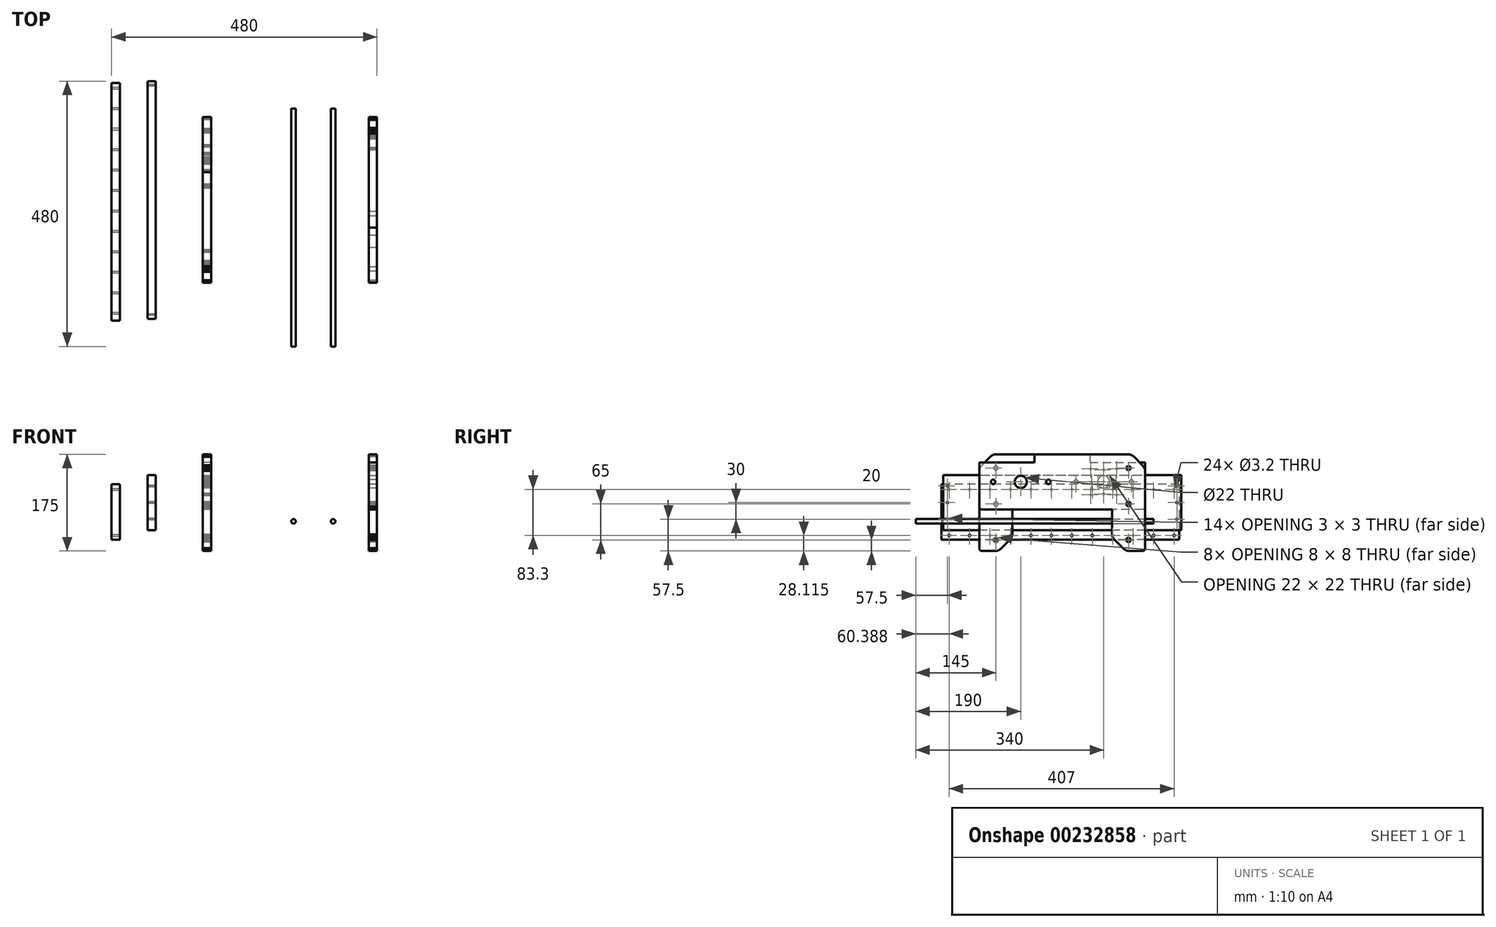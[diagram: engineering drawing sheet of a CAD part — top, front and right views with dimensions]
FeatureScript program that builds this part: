
annotation { "Feature Type Name" : "Feature", "Feature Type Description" : "" }
export const myFeature = defineFeature(function(context is Context, id is Id, definition is map)
    precondition{}
    {
        {
            var Q0;
            Q0=qCreatedBy(makeId("Right.planeOp"),FACE);
            var sketch = newSketch(context, id + "F0", { "sketchPlane" : qUnion([Q0])});
            skLineSegment(sketch, "E0", {"start": v(-140, 97.5) * mm, "end": v(-125, 97.5) * mm});
            skLineSegment(sketch, "E1", {"start": v(-125, 97.5) * mm, "end": v(-122.96, 97.12) * mm});
            skLineSegment(sketch, "E2", {"start": v(-122.96, 97.12) * mm, "end": v(-120.94, 96.66) * mm});
            skLineSegment(sketch, "E3", {"start": v(-120.94, 96.66) * mm, "end": v(-118.94, 96.1) * mm});
            skLineSegment(sketch, "E4", {"start": v(-118.94, 96.1) * mm, "end": v(-116.96, 95.47) * mm});
            skLineSegment(sketch, "E5", {"start": v(-116.96, 95.47) * mm, "end": v(-115.02, 94.75) * mm});
            skLineSegment(sketch, "E6", {"start": v(-115.02, 94.75) * mm, "end": v(-113.1, 93.95) * mm});
            skLineSegment(sketch, "E7", {"start": v(-113.1, 93.95) * mm, "end": v(-111.23, 93.07) * mm});
            skLineSegment(sketch, "E8", {"start": v(-111.23, 93.07) * mm, "end": v(-109.4, 92.1) * mm});
            skLineSegment(sketch, "E9", {"start": v(-109.4, 92.1) * mm, "end": v(-107.6, 91.07) * mm});
            skLineSegment(sketch, "E10", {"start": v(-107.6, 91.07) * mm, "end": v(-105.85, 89.95) * mm});
            skLineSegment(sketch, "E11", {"start": v(-105.85, 89.95) * mm, "end": v(-104.15, 88.76) * mm});
            skLineSegment(sketch, "E12", {"start": v(-104.15, 88.76) * mm, "end": v(-102.5, 87.5) * mm});
            skLineSegment(sketch, "E13", {"start": v(-102.5, 87.5) * mm, "end": v(-90, 77.5) * mm});
            skLineSegment(sketch, "E14", {"start": v(-90, 77.5) * mm, "end": v(50, 77.5) * mm});
            skLineSegment(sketch, "E15", {"start": v(50, 77.5) * mm, "end": v(50, 62.5) * mm});
            skLineSegment(sketch, "E16", {"start": v(50, 62.5) * mm, "end": v(150, 62.5) * mm});
            skLineSegment(sketch, "E17", {"start": v(150, 62.5) * mm, "end": v(150, -17.5) * mm});
            skLineSegment(sketch, "E18", {"start": v(150, -17.5) * mm, "end": v(149.96, -18.15) * mm});
            skLineSegment(sketch, "E19", {"start": v(149.96, -18.15) * mm, "end": v(149.83, -18.8) * mm});
            skLineSegment(sketch, "E20", {"start": v(149.83, -18.8) * mm, "end": v(149.62, -19.41) * mm});
            skLineSegment(sketch, "E21", {"start": v(149.62, -19.41) * mm, "end": v(149.33, -20) * mm});
            skLineSegment(sketch, "E22", {"start": v(149.33, -20) * mm, "end": v(148.97, -20.54) * mm});
            skLineSegment(sketch, "E23", {"start": v(148.97, -20.54) * mm, "end": v(148.54, -21.04) * mm});
            skLineSegment(sketch, "E24", {"start": v(148.54, -21.04) * mm, "end": v(148.04, -21.47) * mm});
            skLineSegment(sketch, "E25", {"start": v(148.04, -21.47) * mm, "end": v(147.5, -21.83) * mm});
            skLineSegment(sketch, "E26", {"start": v(147.5, -21.83) * mm, "end": v(146.91, -22.12) * mm});
            skLineSegment(sketch, "E27", {"start": v(146.91, -22.12) * mm, "end": v(146.3, -22.33) * mm});
            skLineSegment(sketch, "E28", {"start": v(146.3, -22.33) * mm, "end": v(145.65, -22.46) * mm});
            skLineSegment(sketch, "E29", {"start": v(145.65, -22.46) * mm, "end": v(145, -22.5) * mm});
            skLineSegment(sketch, "E30", {"start": v(145, -22.5) * mm, "end": v(-90, -22.5) * mm});
            skLineSegment(sketch, "E31", {"start": v(-90, -22.5) * mm, "end": v(-90, -67.5) * mm});
            skLineSegment(sketch, "E32", {"start": v(-90, -67.5) * mm, "end": v(-90.16, -68.43) * mm});
            skLineSegment(sketch, "E33", {"start": v(-90.16, -68.43) * mm, "end": v(-90.37, -69.36) * mm});
            skLineSegment(sketch, "E34", {"start": v(-90.37, -69.36) * mm, "end": v(-90.63, -70.27) * mm});
            skLineSegment(sketch, "E35", {"start": v(-90.63, -70.27) * mm, "end": v(-90.93, -71.17) * mm});
            skLineSegment(sketch, "E36", {"start": v(-90.93, -71.17) * mm, "end": v(-91.29, -72.05) * mm});
            skLineSegment(sketch, "E37", {"start": v(-91.29, -72.05) * mm, "end": v(-91.69, -72.9) * mm});
            skLineSegment(sketch, "E38", {"start": v(-91.69, -72.9) * mm, "end": v(-92.14, -73.74) * mm});
            skLineSegment(sketch, "E39", {"start": v(-92.14, -73.74) * mm, "end": v(-92.63, -74.55) * mm});
            skLineSegment(sketch, "E40", {"start": v(-92.63, -74.55) * mm, "end": v(-93.16, -75.34) * mm});
            skLineSegment(sketch, "E41", {"start": v(-93.16, -75.34) * mm, "end": v(-93.73, -76.1) * mm});
            skLineSegment(sketch, "E42", {"start": v(-93.73, -76.1) * mm, "end": v(-94.35, -76.81) * mm});
            skLineSegment(sketch, "E43", {"start": v(-94.35, -76.81) * mm, "end": v(-95, -77.5) * mm});
            skLineSegment(sketch, "E44", {"start": v(-95, -77.5) * mm, "end": v(-110, -92.5) * mm});
            skLineSegment(sketch, "E45", {"start": v(-110, -92.5) * mm, "end": v(-110.69, -93.15) * mm});
            skLineSegment(sketch, "E46", {"start": v(-110.69, -93.15) * mm, "end": v(-111.4, -93.77) * mm});
            skLineSegment(sketch, "E47", {"start": v(-111.4, -93.77) * mm, "end": v(-112.16, -94.34) * mm});
            skLineSegment(sketch, "E48", {"start": v(-112.16, -94.34) * mm, "end": v(-112.95, -94.87) * mm});
            skLineSegment(sketch, "E49", {"start": v(-112.95, -94.87) * mm, "end": v(-113.76, -95.36) * mm});
            skLineSegment(sketch, "E50", {"start": v(-113.76, -95.36) * mm, "end": v(-114.6, -95.81) * mm});
            skLineSegment(sketch, "E51", {"start": v(-114.6, -95.81) * mm, "end": v(-115.45, -96.21) * mm});
            skLineSegment(sketch, "E52", {"start": v(-115.45, -96.21) * mm, "end": v(-116.33, -96.57) * mm});
            skLineSegment(sketch, "E53", {"start": v(-116.33, -96.57) * mm, "end": v(-117.23, -96.87) * mm});
            skLineSegment(sketch, "E54", {"start": v(-117.23, -96.87) * mm, "end": v(-118.14, -97.13) * mm});
            skLineSegment(sketch, "E55", {"start": v(-118.14, -97.13) * mm, "end": v(-119.07, -97.34) * mm});
            skLineSegment(sketch, "E56", {"start": v(-119.07, -97.34) * mm, "end": v(-120, -97.5) * mm});
            skLineSegment(sketch, "E57", {"start": v(-120, -97.5) * mm, "end": v(-145, -97.5) * mm});
            skLineSegment(sketch, "E58", {"start": v(-145, -97.5) * mm, "end": v(-145.65, -97.46) * mm});
            skLineSegment(sketch, "E59", {"start": v(-145.65, -97.46) * mm, "end": v(-146.3, -97.33) * mm});
            skLineSegment(sketch, "E60", {"start": v(-146.3, -97.33) * mm, "end": v(-146.91, -97.12) * mm});
            skLineSegment(sketch, "E61", {"start": v(-146.91, -97.12) * mm, "end": v(-147.5, -96.83) * mm});
            skLineSegment(sketch, "E62", {"start": v(-147.5, -96.83) * mm, "end": v(-148.04, -96.47) * mm});
            skLineSegment(sketch, "E63", {"start": v(-148.04, -96.47) * mm, "end": v(-148.54, -96.04) * mm});
            skLineSegment(sketch, "E64", {"start": v(-148.54, -96.04) * mm, "end": v(-148.97, -95.54) * mm});
            skLineSegment(sketch, "E65", {"start": v(-148.97, -95.54) * mm, "end": v(-149.33, -95) * mm});
            skLineSegment(sketch, "E66", {"start": v(-149.33, -95) * mm, "end": v(-149.62, -94.41) * mm});
            skLineSegment(sketch, "E67", {"start": v(-149.62, -94.41) * mm, "end": v(-149.83, -93.8) * mm});
            skLineSegment(sketch, "E68", {"start": v(-149.83, -93.8) * mm, "end": v(-149.96, -93.15) * mm});
            skLineSegment(sketch, "E69", {"start": v(-149.96, -93.15) * mm, "end": v(-150, -92.5) * mm});
            skLineSegment(sketch, "E70", {"start": v(-150, -92.5) * mm, "end": v(-150, 87.5) * mm});
            skLineSegment(sketch, "E71", {"start": v(-150, 87.5) * mm, "end": v(-149.91, 88.8) * mm});
            skLineSegment(sketch, "E72", {"start": v(-149.91, 88.8) * mm, "end": v(-149.66, 90.09) * mm});
            skLineSegment(sketch, "E73", {"start": v(-149.66, 90.09) * mm, "end": v(-149.24, 91.33) * mm});
            skLineSegment(sketch, "E74", {"start": v(-149.24, 91.33) * mm, "end": v(-148.66, 92.5) * mm});
            skLineSegment(sketch, "E75", {"start": v(-148.66, 92.5) * mm, "end": v(-147.93, 93.59) * mm});
            skLineSegment(sketch, "E76", {"start": v(-147.93, 93.59) * mm, "end": v(-147.07, 94.57) * mm});
            skLineSegment(sketch, "E77", {"start": v(-147.07, 94.57) * mm, "end": v(-146.09, 95.43) * mm});
            skLineSegment(sketch, "E78", {"start": v(-146.09, 95.43) * mm, "end": v(-145, 96.16) * mm});
            skLineSegment(sketch, "E79", {"start": v(-145, 96.16) * mm, "end": v(-143.83, 96.74) * mm});
            skLineSegment(sketch, "E80", {"start": v(-143.83, 96.74) * mm, "end": v(-142.59, 97.16) * mm});
            skLineSegment(sketch, "E81", {"start": v(-142.59, 97.16) * mm, "end": v(-141.3, 97.41) * mm});
            skLineSegment(sketch, "E82", {"start": v(-141.3, 97.41) * mm, "end": v(-140, 97.5) * mm});
            skLineSegment(sketch, "E83", {"start": v(-122.83, -80.33) * mm, "end": v(-122, -80.96) * mm});
            skLineSegment(sketch, "E84", {"start": v(-122, -80.96) * mm, "end": v(-121.04, -81.36) * mm});
            skLineSegment(sketch, "E85", {"start": v(-121.04, -81.36) * mm, "end": v(-120, -81.5) * mm});
            skLineSegment(sketch, "E86", {"start": v(-120, -81.5) * mm, "end": v(-118.96, -81.36) * mm});
            skLineSegment(sketch, "E87", {"start": v(-118.96, -81.36) * mm, "end": v(-118, -80.96) * mm});
            skLineSegment(sketch, "E88", {"start": v(-118, -80.96) * mm, "end": v(-117.17, -80.33) * mm});
            skLineSegment(sketch, "E89", {"start": v(-117.17, -80.33) * mm, "end": v(-116.54, -79.5) * mm});
            skLineSegment(sketch, "E90", {"start": v(-116.54, -79.5) * mm, "end": v(-116.14, -78.54) * mm});
            skLineSegment(sketch, "E91", {"start": v(-116.14, -78.54) * mm, "end": v(-116, -77.5) * mm});
            skLineSegment(sketch, "E92", {"start": v(-116, -77.5) * mm, "end": v(-116.14, -76.46) * mm});
            skLineSegment(sketch, "E93", {"start": v(-116.14, -76.46) * mm, "end": v(-116.54, -75.5) * mm});
            skLineSegment(sketch, "E94", {"start": v(-116.54, -75.5) * mm, "end": v(-117.17, -74.67) * mm});
            skLineSegment(sketch, "E95", {"start": v(-117.17, -74.67) * mm, "end": v(-118, -74.04) * mm});
            skLineSegment(sketch, "E96", {"start": v(-118, -74.04) * mm, "end": v(-118.96, -73.64) * mm});
            skLineSegment(sketch, "E97", {"start": v(-118.96, -73.64) * mm, "end": v(-120, -73.5) * mm});
            skLineSegment(sketch, "E98", {"start": v(-120, -73.5) * mm, "end": v(-121.04, -73.64) * mm});
            skLineSegment(sketch, "E99", {"start": v(-121.04, -73.64) * mm, "end": v(-122, -74.04) * mm});
            skLineSegment(sketch, "E100", {"start": v(-122, -74.04) * mm, "end": v(-122.83, -74.67) * mm});
            skLineSegment(sketch, "E101", {"start": v(-122.83, -74.67) * mm, "end": v(-123.46, -75.5) * mm});
            skLineSegment(sketch, "E102", {"start": v(-123.46, -75.5) * mm, "end": v(-123.86, -76.46) * mm});
            skLineSegment(sketch, "E103", {"start": v(-123.86, -76.46) * mm, "end": v(-124, -77.5) * mm});
            skLineSegment(sketch, "E104", {"start": v(-124, -77.5) * mm, "end": v(-123.86, -78.54) * mm});
            skLineSegment(sketch, "E105", {"start": v(-123.86, -78.54) * mm, "end": v(-123.46, -79.5) * mm});
            skLineSegment(sketch, "E106", {"start": v(-123.46, -79.5) * mm, "end": v(-122.83, -80.33) * mm});
            skLineSegment(sketch, "E107", {"start": v(-117.17, -9.67) * mm, "end": v(-118, -9.04) * mm});
            skLineSegment(sketch, "E108", {"start": v(-118, -9.04) * mm, "end": v(-118.96, -8.64) * mm});
            skLineSegment(sketch, "E109", {"start": v(-118.96, -8.64) * mm, "end": v(-120, -8.5) * mm});
            skLineSegment(sketch, "E110", {"start": v(-120, -8.5) * mm, "end": v(-121.04, -8.64) * mm});
            skLineSegment(sketch, "E111", {"start": v(-121.04, -8.64) * mm, "end": v(-122, -9.04) * mm});
            skLineSegment(sketch, "E112", {"start": v(-122, -9.04) * mm, "end": v(-122.83, -9.67) * mm});
            skLineSegment(sketch, "E113", {"start": v(-122.83, -9.67) * mm, "end": v(-123.46, -10.5) * mm});
            skLineSegment(sketch, "E114", {"start": v(-123.46, -10.5) * mm, "end": v(-123.86, -11.46) * mm});
            skLineSegment(sketch, "E115", {"start": v(-123.86, -11.46) * mm, "end": v(-124, -12.5) * mm});
            skLineSegment(sketch, "E116", {"start": v(-124, -12.5) * mm, "end": v(-123.86, -13.54) * mm});
            skLineSegment(sketch, "E117", {"start": v(-123.86, -13.54) * mm, "end": v(-123.46, -14.5) * mm});
            skLineSegment(sketch, "E118", {"start": v(-123.46, -14.5) * mm, "end": v(-122.83, -15.33) * mm});
            skLineSegment(sketch, "E119", {"start": v(-122.83, -15.33) * mm, "end": v(-122, -15.96) * mm});
            skLineSegment(sketch, "E120", {"start": v(-122, -15.96) * mm, "end": v(-121.04, -16.36) * mm});
            skLineSegment(sketch, "E121", {"start": v(-121.04, -16.36) * mm, "end": v(-120, -16.5) * mm});
            skLineSegment(sketch, "E122", {"start": v(-120, -16.5) * mm, "end": v(-118.96, -16.36) * mm});
            skLineSegment(sketch, "E123", {"start": v(-118.96, -16.36) * mm, "end": v(-118, -15.96) * mm});
            skLineSegment(sketch, "E124", {"start": v(-118, -15.96) * mm, "end": v(-117.17, -15.33) * mm});
            skLineSegment(sketch, "E125", {"start": v(-117.17, -15.33) * mm, "end": v(-116.54, -14.5) * mm});
            skLineSegment(sketch, "E126", {"start": v(-116.54, -14.5) * mm, "end": v(-116.14, -13.54) * mm});
            skLineSegment(sketch, "E127", {"start": v(-116.14, -13.54) * mm, "end": v(-116, -12.5) * mm});
            skLineSegment(sketch, "E128", {"start": v(-116, -12.5) * mm, "end": v(-116.14, -11.46) * mm});
            skLineSegment(sketch, "E129", {"start": v(-116.14, -11.46) * mm, "end": v(-116.54, -10.5) * mm});
            skLineSegment(sketch, "E130", {"start": v(-116.54, -10.5) * mm, "end": v(-117.17, -9.67) * mm});
            skLineSegment(sketch, "E131", {"start": v(-118, 49.04) * mm, "end": v(-117.17, 49.67) * mm});
            skLineSegment(sketch, "E132", {"start": v(-117.17, 49.67) * mm, "end": v(-116.54, 50.5) * mm});
            skLineSegment(sketch, "E133", {"start": v(-116.54, 50.5) * mm, "end": v(-116.14, 51.46) * mm});
            skLineSegment(sketch, "E134", {"start": v(-116.14, 51.46) * mm, "end": v(-116, 52.5) * mm});
            skLineSegment(sketch, "E135", {"start": v(-116, 52.5) * mm, "end": v(-116.14, 53.54) * mm});
            skLineSegment(sketch, "E136", {"start": v(-116.14, 53.54) * mm, "end": v(-116.54, 54.5) * mm});
            skLineSegment(sketch, "E137", {"start": v(-116.54, 54.5) * mm, "end": v(-117.17, 55.33) * mm});
            skLineSegment(sketch, "E138", {"start": v(-117.17, 55.33) * mm, "end": v(-118, 55.96) * mm});
            skLineSegment(sketch, "E139", {"start": v(-118, 55.96) * mm, "end": v(-118.96, 56.36) * mm});
            skLineSegment(sketch, "E140", {"start": v(-118.96, 56.36) * mm, "end": v(-120, 56.5) * mm});
            skLineSegment(sketch, "E141", {"start": v(-120, 56.5) * mm, "end": v(-121.04, 56.36) * mm});
            skLineSegment(sketch, "E142", {"start": v(-121.04, 56.36) * mm, "end": v(-122, 55.96) * mm});
            skLineSegment(sketch, "E143", {"start": v(-122, 55.96) * mm, "end": v(-122.83, 55.33) * mm});
            skLineSegment(sketch, "E144", {"start": v(-122.83, 55.33) * mm, "end": v(-123.46, 54.5) * mm});
            skLineSegment(sketch, "E145", {"start": v(-123.46, 54.5) * mm, "end": v(-123.86, 53.54) * mm});
            skLineSegment(sketch, "E146", {"start": v(-123.86, 53.54) * mm, "end": v(-124, 52.5) * mm});
            skLineSegment(sketch, "E147", {"start": v(-124, 52.5) * mm, "end": v(-123.86, 51.46) * mm});
            skLineSegment(sketch, "E148", {"start": v(-123.86, 51.46) * mm, "end": v(-123.46, 50.5) * mm});
            skLineSegment(sketch, "E149", {"start": v(-123.46, 50.5) * mm, "end": v(-122.83, 49.67) * mm});
            skLineSegment(sketch, "E150", {"start": v(-122.83, 49.67) * mm, "end": v(-122, 49.04) * mm});
            skLineSegment(sketch, "E151", {"start": v(-122, 49.04) * mm, "end": v(-121.04, 48.64) * mm});
            skLineSegment(sketch, "E152", {"start": v(-121.04, 48.64) * mm, "end": v(-120, 48.5) * mm});
            skLineSegment(sketch, "E153", {"start": v(-120, 48.5) * mm, "end": v(-118.96, 48.64) * mm});
            skLineSegment(sketch, "E154", {"start": v(-118.96, 48.64) * mm, "end": v(-118, 49.04) * mm});
            skLineSegment(sketch, "E155", {"start": v(72.15, 38.13) * mm, "end": v(69.5, 37.03) * mm});
            skLineSegment(sketch, "E156", {"start": v(69.5, 37.03) * mm, "end": v(67.22, 35.28) * mm});
            skLineSegment(sketch, "E157", {"start": v(67.22, 35.28) * mm, "end": v(65.47, 33) * mm});
            skLineSegment(sketch, "E158", {"start": v(65.47, 33) * mm, "end": v(64.37, 30.35) * mm});
            skLineSegment(sketch, "E159", {"start": v(64.37, 30.35) * mm, "end": v(64, 27.5) * mm});
            skLineSegment(sketch, "E160", {"start": v(64, 27.5) * mm, "end": v(64.37, 24.65) * mm});
            skLineSegment(sketch, "E161", {"start": v(64.37, 24.65) * mm, "end": v(65.47, 22) * mm});
            skLineSegment(sketch, "E162", {"start": v(65.47, 22) * mm, "end": v(67.22, 19.72) * mm});
            skLineSegment(sketch, "E163", {"start": v(67.22, 19.72) * mm, "end": v(69.5, 17.97) * mm});
            skLineSegment(sketch, "E164", {"start": v(69.5, 17.97) * mm, "end": v(72.15, 16.87) * mm});
            skLineSegment(sketch, "E165", {"start": v(72.15, 16.87) * mm, "end": v(75, 16.5) * mm});
            skLineSegment(sketch, "E166", {"start": v(75, 16.5) * mm, "end": v(77.85, 16.87) * mm});
            skLineSegment(sketch, "E167", {"start": v(77.85, 16.87) * mm, "end": v(80.5, 17.97) * mm});
            skLineSegment(sketch, "E168", {"start": v(80.5, 17.97) * mm, "end": v(82.78, 19.72) * mm});
            skLineSegment(sketch, "E169", {"start": v(82.78, 19.72) * mm, "end": v(84.53, 22) * mm});
            skLineSegment(sketch, "E170", {"start": v(84.53, 22) * mm, "end": v(85.63, 24.65) * mm});
            skLineSegment(sketch, "E171", {"start": v(85.63, 24.65) * mm, "end": v(86, 27.5) * mm});
            skLineSegment(sketch, "E172", {"start": v(86, 27.5) * mm, "end": v(85.63, 30.35) * mm});
            skLineSegment(sketch, "E173", {"start": v(85.63, 30.35) * mm, "end": v(84.53, 33) * mm});
            skLineSegment(sketch, "E174", {"start": v(84.53, 33) * mm, "end": v(82.78, 35.28) * mm});
            skLineSegment(sketch, "E175", {"start": v(82.78, 35.28) * mm, "end": v(80.5, 37.03) * mm});
            skLineSegment(sketch, "E176", {"start": v(80.5, 37.03) * mm, "end": v(77.85, 38.13) * mm});
            skLineSegment(sketch, "E177", {"start": v(77.85, 38.13) * mm, "end": v(75, 38.5) * mm});
            skLineSegment(sketch, "E178", {"start": v(75, 38.5) * mm, "end": v(72.15, 38.13) * mm});
            skLineSegment(sketch, "E179", {"start": v(97.8, 5.25) * mm, "end": v(97.49, 5.01) * mm});
            skLineSegment(sketch, "E180", {"start": v(97.49, 5.01) * mm, "end": v(97.25, 4.7) * mm});
            skLineSegment(sketch, "E181", {"start": v(97.25, 4.7) * mm, "end": v(97.1, 4.34) * mm});
            skLineSegment(sketch, "E182", {"start": v(97.1, 4.34) * mm, "end": v(97.05, 3.95) * mm});
            skLineSegment(sketch, "E183", {"start": v(97.05, 3.95) * mm, "end": v(97.1, 3.56) * mm});
            skLineSegment(sketch, "E184", {"start": v(97.1, 3.56) * mm, "end": v(97.25, 3.2) * mm});
            skLineSegment(sketch, "E185", {"start": v(97.25, 3.2) * mm, "end": v(97.49, 2.89) * mm});
            skLineSegment(sketch, "E186", {"start": v(97.49, 2.89) * mm, "end": v(97.8, 2.65) * mm});
            skLineSegment(sketch, "E187", {"start": v(97.8, 2.65) * mm, "end": v(98.16, 2.5) * mm});
            skLineSegment(sketch, "E188", {"start": v(98.16, 2.5) * mm, "end": v(98.55, 2.45) * mm});
            skLineSegment(sketch, "E189", {"start": v(98.55, 2.45) * mm, "end": v(98.94, 2.5) * mm});
            skLineSegment(sketch, "E190", {"start": v(98.94, 2.5) * mm, "end": v(99.3, 2.65) * mm});
            skLineSegment(sketch, "E191", {"start": v(99.3, 2.65) * mm, "end": v(99.61, 2.89) * mm});
            skLineSegment(sketch, "E192", {"start": v(99.61, 2.89) * mm, "end": v(99.85, 3.2) * mm});
            skLineSegment(sketch, "E193", {"start": v(99.85, 3.2) * mm, "end": v(100, 3.56) * mm});
            skLineSegment(sketch, "E194", {"start": v(100, 3.56) * mm, "end": v(100.05, 3.95) * mm});
            skLineSegment(sketch, "E195", {"start": v(100.05, 3.95) * mm, "end": v(100, 4.34) * mm});
            skLineSegment(sketch, "E196", {"start": v(100, 4.34) * mm, "end": v(99.85, 4.7) * mm});
            skLineSegment(sketch, "E197", {"start": v(99.85, 4.7) * mm, "end": v(99.61, 5.01) * mm});
            skLineSegment(sketch, "E198", {"start": v(99.61, 5.01) * mm, "end": v(99.3, 5.25) * mm});
            skLineSegment(sketch, "E199", {"start": v(99.3, 5.25) * mm, "end": v(98.94, 5.4) * mm});
            skLineSegment(sketch, "E200", {"start": v(98.94, 5.4) * mm, "end": v(98.55, 5.45) * mm});
            skLineSegment(sketch, "E201", {"start": v(98.55, 5.45) * mm, "end": v(98.16, 5.4) * mm});
            skLineSegment(sketch, "E202", {"start": v(98.16, 5.4) * mm, "end": v(97.8, 5.25) * mm});
            skLineSegment(sketch, "E203", {"start": v(51.45, 5.45) * mm, "end": v(51.06, 5.4) * mm});
            skLineSegment(sketch, "E204", {"start": v(51.06, 5.4) * mm, "end": v(50.7, 5.25) * mm});
            skLineSegment(sketch, "E205", {"start": v(50.7, 5.25) * mm, "end": v(50.39, 5.01) * mm});
            skLineSegment(sketch, "E206", {"start": v(50.39, 5.01) * mm, "end": v(50.15, 4.7) * mm});
            skLineSegment(sketch, "E207", {"start": v(50.15, 4.7) * mm, "end": v(50, 4.34) * mm});
            skLineSegment(sketch, "E208", {"start": v(50, 4.34) * mm, "end": v(49.95, 3.95) * mm});
            skLineSegment(sketch, "E209", {"start": v(49.95, 3.95) * mm, "end": v(50, 3.56) * mm});
            skLineSegment(sketch, "E210", {"start": v(50, 3.56) * mm, "end": v(50.15, 3.2) * mm});
            skLineSegment(sketch, "E211", {"start": v(50.15, 3.2) * mm, "end": v(50.39, 2.89) * mm});
            skLineSegment(sketch, "E212", {"start": v(50.39, 2.89) * mm, "end": v(50.7, 2.65) * mm});
            skLineSegment(sketch, "E213", {"start": v(50.7, 2.65) * mm, "end": v(51.06, 2.5) * mm});
            skLineSegment(sketch, "E214", {"start": v(51.06, 2.5) * mm, "end": v(51.45, 2.45) * mm});
            skLineSegment(sketch, "E215", {"start": v(51.45, 2.45) * mm, "end": v(51.84, 2.5) * mm});
            skLineSegment(sketch, "E216", {"start": v(51.84, 2.5) * mm, "end": v(52.2, 2.65) * mm});
            skLineSegment(sketch, "E217", {"start": v(52.2, 2.65) * mm, "end": v(52.51, 2.89) * mm});
            skLineSegment(sketch, "E218", {"start": v(52.51, 2.89) * mm, "end": v(52.75, 3.2) * mm});
            skLineSegment(sketch, "E219", {"start": v(52.75, 3.2) * mm, "end": v(52.9, 3.56) * mm});
            skLineSegment(sketch, "E220", {"start": v(52.9, 3.56) * mm, "end": v(52.95, 3.95) * mm});
            skLineSegment(sketch, "E221", {"start": v(52.95, 3.95) * mm, "end": v(52.9, 4.34) * mm});
            skLineSegment(sketch, "E222", {"start": v(52.9, 4.34) * mm, "end": v(52.75, 4.7) * mm});
            skLineSegment(sketch, "E223", {"start": v(52.75, 4.7) * mm, "end": v(52.51, 5.01) * mm});
            skLineSegment(sketch, "E224", {"start": v(52.51, 5.01) * mm, "end": v(52.2, 5.25) * mm});
            skLineSegment(sketch, "E225", {"start": v(52.2, 5.25) * mm, "end": v(51.84, 5.4) * mm});
            skLineSegment(sketch, "E226", {"start": v(51.84, 5.4) * mm, "end": v(51.45, 5.45) * mm});
            skLineSegment(sketch, "E227", {"start": v(50, 51.44) * mm, "end": v(49.95, 51.05) * mm});
            skLineSegment(sketch, "E228", {"start": v(49.95, 51.05) * mm, "end": v(50, 50.66) * mm});
            skLineSegment(sketch, "E229", {"start": v(50, 50.66) * mm, "end": v(50.15, 50.3) * mm});
            skLineSegment(sketch, "E230", {"start": v(50.15, 50.3) * mm, "end": v(50.39, 49.99) * mm});
            skLineSegment(sketch, "E231", {"start": v(50.39, 49.99) * mm, "end": v(50.7, 49.75) * mm});
            skLineSegment(sketch, "E232", {"start": v(50.7, 49.75) * mm, "end": v(51.06, 49.6) * mm});
            skLineSegment(sketch, "E233", {"start": v(51.06, 49.6) * mm, "end": v(51.45, 49.55) * mm});
            skLineSegment(sketch, "E234", {"start": v(51.45, 49.55) * mm, "end": v(51.84, 49.6) * mm});
            skLineSegment(sketch, "E235", {"start": v(51.84, 49.6) * mm, "end": v(52.2, 49.75) * mm});
            skLineSegment(sketch, "E236", {"start": v(52.2, 49.75) * mm, "end": v(52.51, 49.99) * mm});
            skLineSegment(sketch, "E237", {"start": v(52.51, 49.99) * mm, "end": v(52.75, 50.3) * mm});
            skLineSegment(sketch, "E238", {"start": v(52.75, 50.3) * mm, "end": v(52.9, 50.66) * mm});
            skLineSegment(sketch, "E239", {"start": v(52.9, 50.66) * mm, "end": v(52.95, 51.05) * mm});
            skLineSegment(sketch, "E240", {"start": v(52.95, 51.05) * mm, "end": v(52.9, 51.44) * mm});
            skLineSegment(sketch, "E241", {"start": v(52.9, 51.44) * mm, "end": v(52.75, 51.8) * mm});
            skLineSegment(sketch, "E242", {"start": v(52.75, 51.8) * mm, "end": v(52.51, 52.11) * mm});
            skLineSegment(sketch, "E243", {"start": v(52.51, 52.11) * mm, "end": v(52.2, 52.35) * mm});
            skLineSegment(sketch, "E244", {"start": v(52.2, 52.35) * mm, "end": v(51.84, 52.5) * mm});
            skLineSegment(sketch, "E245", {"start": v(51.84, 52.5) * mm, "end": v(51.45, 52.55) * mm});
            skLineSegment(sketch, "E246", {"start": v(51.45, 52.55) * mm, "end": v(51.06, 52.5) * mm});
            skLineSegment(sketch, "E247", {"start": v(51.06, 52.5) * mm, "end": v(50.7, 52.35) * mm});
            skLineSegment(sketch, "E248", {"start": v(50.7, 52.35) * mm, "end": v(50.39, 52.11) * mm});
            skLineSegment(sketch, "E249", {"start": v(50.39, 52.11) * mm, "end": v(50.15, 51.8) * mm});
            skLineSegment(sketch, "E250", {"start": v(50.15, 51.8) * mm, "end": v(50, 51.44) * mm});
            skLineSegment(sketch, "E251", {"start": v(98.16, 49.6) * mm, "end": v(98.55, 49.55) * mm});
            skLineSegment(sketch, "E252", {"start": v(98.55, 49.55) * mm, "end": v(98.94, 49.6) * mm});
            skLineSegment(sketch, "E253", {"start": v(98.94, 49.6) * mm, "end": v(99.3, 49.75) * mm});
            skLineSegment(sketch, "E254", {"start": v(99.3, 49.75) * mm, "end": v(99.61, 49.99) * mm});
            skLineSegment(sketch, "E255", {"start": v(99.61, 49.99) * mm, "end": v(99.85, 50.3) * mm});
            skLineSegment(sketch, "E256", {"start": v(99.85, 50.3) * mm, "end": v(100, 50.66) * mm});
            skLineSegment(sketch, "E257", {"start": v(100, 50.66) * mm, "end": v(100.05, 51.05) * mm});
            skLineSegment(sketch, "E258", {"start": v(100.05, 51.05) * mm, "end": v(100, 51.44) * mm});
            skLineSegment(sketch, "E259", {"start": v(100, 51.44) * mm, "end": v(99.85, 51.8) * mm});
            skLineSegment(sketch, "E260", {"start": v(99.85, 51.8) * mm, "end": v(99.61, 52.11) * mm});
            skLineSegment(sketch, "E261", {"start": v(99.61, 52.11) * mm, "end": v(99.3, 52.35) * mm});
            skLineSegment(sketch, "E262", {"start": v(99.3, 52.35) * mm, "end": v(98.94, 52.5) * mm});
            skLineSegment(sketch, "E263", {"start": v(98.94, 52.5) * mm, "end": v(98.55, 52.55) * mm});
            skLineSegment(sketch, "E264", {"start": v(98.55, 52.55) * mm, "end": v(98.16, 52.5) * mm});
            skLineSegment(sketch, "E265", {"start": v(98.16, 52.5) * mm, "end": v(97.8, 52.35) * mm});
            skLineSegment(sketch, "E266", {"start": v(97.8, 52.35) * mm, "end": v(97.49, 52.11) * mm});
            skLineSegment(sketch, "E267", {"start": v(97.49, 52.11) * mm, "end": v(97.25, 51.8) * mm});
            skLineSegment(sketch, "E268", {"start": v(97.25, 51.8) * mm, "end": v(97.1, 51.44) * mm});
            skLineSegment(sketch, "E269", {"start": v(97.1, 51.44) * mm, "end": v(97.05, 51.05) * mm});
            skLineSegment(sketch, "E270", {"start": v(97.05, 51.05) * mm, "end": v(97.1, 50.66) * mm});
            skLineSegment(sketch, "E271", {"start": v(97.1, 50.66) * mm, "end": v(97.25, 50.3) * mm});
            skLineSegment(sketch, "E272", {"start": v(97.25, 50.3) * mm, "end": v(97.49, 49.99) * mm});
            skLineSegment(sketch, "E273", {"start": v(97.49, 49.99) * mm, "end": v(97.8, 49.75) * mm});
            skLineSegment(sketch, "E274", {"start": v(97.8, 49.75) * mm, "end": v(98.16, 49.6) * mm});
            skLineSegment(sketch, "E275", {"start": v(51.63, 27.89) * mm, "end": v(51.58, 27.5) * mm});
            skLineSegment(sketch, "E276", {"start": v(51.58, 27.5) * mm, "end": v(51.63, 27.11) * mm});
            skLineSegment(sketch, "E277", {"start": v(51.63, 27.11) * mm, "end": v(51.78, 26.75) * mm});
            skLineSegment(sketch, "E278", {"start": v(51.78, 26.75) * mm, "end": v(52.02, 26.44) * mm});
            skLineSegment(sketch, "E279", {"start": v(52.02, 26.44) * mm, "end": v(52.33, 26.2) * mm});
            skLineSegment(sketch, "E280", {"start": v(52.33, 26.2) * mm, "end": v(52.7, 26.05) * mm});
            skLineSegment(sketch, "E281", {"start": v(52.7, 26.05) * mm, "end": v(53.08, 26) * mm});
            skLineSegment(sketch, "E282", {"start": v(53.08, 26) * mm, "end": v(53.47, 26.05) * mm});
            skLineSegment(sketch, "E283", {"start": v(53.47, 26.05) * mm, "end": v(53.83, 26.2) * mm});
            skLineSegment(sketch, "E284", {"start": v(53.83, 26.2) * mm, "end": v(54.14, 26.44) * mm});
            skLineSegment(sketch, "E285", {"start": v(54.14, 26.44) * mm, "end": v(54.38, 26.75) * mm});
            skLineSegment(sketch, "E286", {"start": v(54.38, 26.75) * mm, "end": v(54.53, 27.11) * mm});
            skLineSegment(sketch, "E287", {"start": v(54.53, 27.11) * mm, "end": v(54.58, 27.5) * mm});
            skLineSegment(sketch, "E288", {"start": v(54.58, 27.5) * mm, "end": v(54.53, 27.89) * mm});
            skLineSegment(sketch, "E289", {"start": v(54.53, 27.89) * mm, "end": v(54.38, 28.25) * mm});
            skLineSegment(sketch, "E290", {"start": v(54.38, 28.25) * mm, "end": v(54.14, 28.56) * mm});
            skLineSegment(sketch, "E291", {"start": v(54.14, 28.56) * mm, "end": v(53.83, 28.8) * mm});
            skLineSegment(sketch, "E292", {"start": v(53.83, 28.8) * mm, "end": v(53.47, 28.95) * mm});
            skLineSegment(sketch, "E293", {"start": v(53.47, 28.95) * mm, "end": v(53.08, 29) * mm});
            skLineSegment(sketch, "E294", {"start": v(53.08, 29) * mm, "end": v(52.7, 28.95) * mm});
            skLineSegment(sketch, "E295", {"start": v(52.7, 28.95) * mm, "end": v(52.33, 28.8) * mm});
            skLineSegment(sketch, "E296", {"start": v(52.33, 28.8) * mm, "end": v(52.02, 28.56) * mm});
            skLineSegment(sketch, "E297", {"start": v(52.02, 28.56) * mm, "end": v(51.78, 28.25) * mm});
            skLineSegment(sketch, "E298", {"start": v(51.78, 28.25) * mm, "end": v(51.63, 27.89) * mm});
            skLineSegment(sketch, "E299", {"start": v(73.94, 4.52) * mm, "end": v(74.25, 4.28) * mm});
            skLineSegment(sketch, "E300", {"start": v(74.25, 4.28) * mm, "end": v(74.61, 4.13) * mm});
            skLineSegment(sketch, "E301", {"start": v(74.61, 4.13) * mm, "end": v(75, 4.08) * mm});
            skLineSegment(sketch, "E302", {"start": v(75, 4.08) * mm, "end": v(75.39, 4.13) * mm});
            skLineSegment(sketch, "E303", {"start": v(75.39, 4.13) * mm, "end": v(75.75, 4.28) * mm});
            skLineSegment(sketch, "E304", {"start": v(75.75, 4.28) * mm, "end": v(76.06, 4.52) * mm});
            skLineSegment(sketch, "E305", {"start": v(76.06, 4.52) * mm, "end": v(76.3, 4.83) * mm});
            skLineSegment(sketch, "E306", {"start": v(76.3, 4.83) * mm, "end": v(76.45, 5.2) * mm});
            skLineSegment(sketch, "E307", {"start": v(76.45, 5.2) * mm, "end": v(76.5, 5.58) * mm});
            skLineSegment(sketch, "E308", {"start": v(76.5, 5.58) * mm, "end": v(76.45, 5.97) * mm});
            skLineSegment(sketch, "E309", {"start": v(76.45, 5.97) * mm, "end": v(76.3, 6.33) * mm});
            skLineSegment(sketch, "E310", {"start": v(76.3, 6.33) * mm, "end": v(76.06, 6.64) * mm});
            skLineSegment(sketch, "E311", {"start": v(76.06, 6.64) * mm, "end": v(75.75, 6.88) * mm});
            skLineSegment(sketch, "E312", {"start": v(75.75, 6.88) * mm, "end": v(75.39, 7.03) * mm});
            skLineSegment(sketch, "E313", {"start": v(75.39, 7.03) * mm, "end": v(75, 7.08) * mm});
            skLineSegment(sketch, "E314", {"start": v(75, 7.08) * mm, "end": v(74.61, 7.03) * mm});
            skLineSegment(sketch, "E315", {"start": v(74.61, 7.03) * mm, "end": v(74.25, 6.88) * mm});
            skLineSegment(sketch, "E316", {"start": v(74.25, 6.88) * mm, "end": v(73.94, 6.64) * mm});
            skLineSegment(sketch, "E317", {"start": v(73.94, 6.64) * mm, "end": v(73.7, 6.33) * mm});
            skLineSegment(sketch, "E318", {"start": v(73.7, 6.33) * mm, "end": v(73.55, 5.97) * mm});
            skLineSegment(sketch, "E319", {"start": v(73.55, 5.97) * mm, "end": v(73.5, 5.58) * mm});
            skLineSegment(sketch, "E320", {"start": v(73.5, 5.58) * mm, "end": v(73.55, 5.2) * mm});
            skLineSegment(sketch, "E321", {"start": v(73.55, 5.2) * mm, "end": v(73.7, 4.83) * mm});
            skLineSegment(sketch, "E322", {"start": v(73.7, 4.83) * mm, "end": v(73.94, 4.52) * mm});
            skLineSegment(sketch, "E323", {"start": v(96.53, 28.95) * mm, "end": v(96.17, 28.8) * mm});
            skLineSegment(sketch, "E324", {"start": v(96.17, 28.8) * mm, "end": v(95.86, 28.56) * mm});
            skLineSegment(sketch, "E325", {"start": v(95.86, 28.56) * mm, "end": v(95.62, 28.25) * mm});
            skLineSegment(sketch, "E326", {"start": v(95.62, 28.25) * mm, "end": v(95.47, 27.89) * mm});
            skLineSegment(sketch, "E327", {"start": v(95.47, 27.89) * mm, "end": v(95.42, 27.5) * mm});
            skLineSegment(sketch, "E328", {"start": v(95.42, 27.5) * mm, "end": v(95.47, 27.11) * mm});
            skLineSegment(sketch, "E329", {"start": v(95.47, 27.11) * mm, "end": v(95.62, 26.75) * mm});
            skLineSegment(sketch, "E330", {"start": v(95.62, 26.75) * mm, "end": v(95.86, 26.44) * mm});
            skLineSegment(sketch, "E331", {"start": v(95.86, 26.44) * mm, "end": v(96.17, 26.2) * mm});
            skLineSegment(sketch, "E332", {"start": v(96.17, 26.2) * mm, "end": v(96.53, 26.05) * mm});
            skLineSegment(sketch, "E333", {"start": v(96.53, 26.05) * mm, "end": v(96.92, 26) * mm});
            skLineSegment(sketch, "E334", {"start": v(96.92, 26) * mm, "end": v(97.3, 26.05) * mm});
            skLineSegment(sketch, "E335", {"start": v(97.3, 26.05) * mm, "end": v(97.67, 26.2) * mm});
            skLineSegment(sketch, "E336", {"start": v(97.67, 26.2) * mm, "end": v(97.98, 26.44) * mm});
            skLineSegment(sketch, "E337", {"start": v(97.98, 26.44) * mm, "end": v(98.22, 26.75) * mm});
            skLineSegment(sketch, "E338", {"start": v(98.22, 26.75) * mm, "end": v(98.37, 27.11) * mm});
            skLineSegment(sketch, "E339", {"start": v(98.37, 27.11) * mm, "end": v(98.42, 27.5) * mm});
            skLineSegment(sketch, "E340", {"start": v(98.42, 27.5) * mm, "end": v(98.37, 27.89) * mm});
            skLineSegment(sketch, "E341", {"start": v(98.37, 27.89) * mm, "end": v(98.22, 28.25) * mm});
            skLineSegment(sketch, "E342", {"start": v(98.22, 28.25) * mm, "end": v(97.98, 28.56) * mm});
            skLineSegment(sketch, "E343", {"start": v(97.98, 28.56) * mm, "end": v(97.67, 28.8) * mm});
            skLineSegment(sketch, "E344", {"start": v(97.67, 28.8) * mm, "end": v(97.3, 28.95) * mm});
            skLineSegment(sketch, "E345", {"start": v(97.3, 28.95) * mm, "end": v(96.92, 29) * mm});
            skLineSegment(sketch, "E346", {"start": v(96.92, 29) * mm, "end": v(96.53, 28.95) * mm});
            skLineSegment(sketch, "E347", {"start": v(74.61, 50.87) * mm, "end": v(74.25, 50.72) * mm});
            skLineSegment(sketch, "E348", {"start": v(74.25, 50.72) * mm, "end": v(73.94, 50.48) * mm});
            skLineSegment(sketch, "E349", {"start": v(73.94, 50.48) * mm, "end": v(73.7, 50.17) * mm});
            skLineSegment(sketch, "E350", {"start": v(73.7, 50.17) * mm, "end": v(73.55, 49.8) * mm});
            skLineSegment(sketch, "E351", {"start": v(73.55, 49.8) * mm, "end": v(73.5, 49.42) * mm});
            skLineSegment(sketch, "E352", {"start": v(73.5, 49.42) * mm, "end": v(73.55, 49.03) * mm});
            skLineSegment(sketch, "E353", {"start": v(73.55, 49.03) * mm, "end": v(73.7, 48.67) * mm});
            skLineSegment(sketch, "E354", {"start": v(73.7, 48.67) * mm, "end": v(73.94, 48.36) * mm});
            skLineSegment(sketch, "E355", {"start": v(73.94, 48.36) * mm, "end": v(74.25, 48.12) * mm});
            skLineSegment(sketch, "E356", {"start": v(74.25, 48.12) * mm, "end": v(74.61, 47.97) * mm});
            skLineSegment(sketch, "E357", {"start": v(74.61, 47.97) * mm, "end": v(75, 47.92) * mm});
            skLineSegment(sketch, "E358", {"start": v(75, 47.92) * mm, "end": v(75.39, 47.97) * mm});
            skLineSegment(sketch, "E359", {"start": v(75.39, 47.97) * mm, "end": v(75.75, 48.12) * mm});
            skLineSegment(sketch, "E360", {"start": v(75.75, 48.12) * mm, "end": v(76.06, 48.36) * mm});
            skLineSegment(sketch, "E361", {"start": v(76.06, 48.36) * mm, "end": v(76.3, 48.67) * mm});
            skLineSegment(sketch, "E362", {"start": v(76.3, 48.67) * mm, "end": v(76.45, 49.03) * mm});
            skLineSegment(sketch, "E363", {"start": v(76.45, 49.03) * mm, "end": v(76.5, 49.42) * mm});
            skLineSegment(sketch, "E364", {"start": v(76.5, 49.42) * mm, "end": v(76.45, 49.8) * mm});
            skLineSegment(sketch, "E365", {"start": v(76.45, 49.8) * mm, "end": v(76.3, 50.17) * mm});
            skLineSegment(sketch, "E366", {"start": v(76.3, 50.17) * mm, "end": v(76.06, 50.48) * mm});
            skLineSegment(sketch, "E367", {"start": v(76.06, 50.48) * mm, "end": v(75.75, 50.72) * mm});
            skLineSegment(sketch, "E368", {"start": v(75.75, 50.72) * mm, "end": v(75.39, 50.87) * mm});
            skLineSegment(sketch, "E369", {"start": v(75.39, 50.87) * mm, "end": v(75, 50.92) * mm});
            skLineSegment(sketch, "E370", {"start": v(75, 50.92) * mm, "end": v(74.61, 50.87) * mm});
            skLineSegment(sketch, "E371", {"start": v(127, 30.96) * mm, "end": v(126.04, 31.36) * mm});
            skLineSegment(sketch, "E372", {"start": v(126.04, 31.36) * mm, "end": v(125, 31.5) * mm});
            skLineSegment(sketch, "E373", {"start": v(125, 31.5) * mm, "end": v(123.96, 31.36) * mm});
            skLineSegment(sketch, "E374", {"start": v(123.96, 31.36) * mm, "end": v(123, 30.96) * mm});
            skLineSegment(sketch, "E375", {"start": v(123, 30.96) * mm, "end": v(122.17, 30.33) * mm});
            skLineSegment(sketch, "E376", {"start": v(122.17, 30.33) * mm, "end": v(121.54, 29.5) * mm});
            skLineSegment(sketch, "E377", {"start": v(121.54, 29.5) * mm, "end": v(121.14, 28.54) * mm});
            skLineSegment(sketch, "E378", {"start": v(121.14, 28.54) * mm, "end": v(121, 27.5) * mm});
            skLineSegment(sketch, "E379", {"start": v(121, 27.5) * mm, "end": v(121.14, 26.46) * mm});
            skLineSegment(sketch, "E380", {"start": v(121.14, 26.46) * mm, "end": v(121.54, 25.5) * mm});
            skLineSegment(sketch, "E381", {"start": v(121.54, 25.5) * mm, "end": v(122.17, 24.67) * mm});
            skLineSegment(sketch, "E382", {"start": v(122.17, 24.67) * mm, "end": v(123, 24.04) * mm});
            skLineSegment(sketch, "E383", {"start": v(123, 24.04) * mm, "end": v(123.96, 23.64) * mm});
            skLineSegment(sketch, "E384", {"start": v(123.96, 23.64) * mm, "end": v(125, 23.5) * mm});
            skLineSegment(sketch, "E385", {"start": v(125, 23.5) * mm, "end": v(126.04, 23.64) * mm});
            skLineSegment(sketch, "E386", {"start": v(126.04, 23.64) * mm, "end": v(127, 24.04) * mm});
            skLineSegment(sketch, "E387", {"start": v(127, 24.04) * mm, "end": v(127.83, 24.67) * mm});
            skLineSegment(sketch, "E388", {"start": v(127.83, 24.67) * mm, "end": v(128.46, 25.5) * mm});
            skLineSegment(sketch, "E389", {"start": v(128.46, 25.5) * mm, "end": v(128.86, 26.46) * mm});
            skLineSegment(sketch, "E390", {"start": v(128.86, 26.46) * mm, "end": v(129, 27.5) * mm});
            skLineSegment(sketch, "E391", {"start": v(129, 27.5) * mm, "end": v(128.86, 28.54) * mm});
            skLineSegment(sketch, "E392", {"start": v(128.86, 28.54) * mm, "end": v(128.46, 29.5) * mm});
            skLineSegment(sketch, "E393", {"start": v(128.46, 29.5) * mm, "end": v(127.83, 30.33) * mm});
            skLineSegment(sketch, "E394", {"start": v(127.83, 30.33) * mm, "end": v(127, 30.96) * mm});
            skLineSegment(sketch, "E395", {"start": v(28.86, 28.54) * mm, "end": v(28.46, 29.5) * mm});
            skLineSegment(sketch, "E396", {"start": v(28.46, 29.5) * mm, "end": v(27.83, 30.33) * mm});
            skLineSegment(sketch, "E397", {"start": v(27.83, 30.33) * mm, "end": v(27, 30.96) * mm});
            skLineSegment(sketch, "E398", {"start": v(27, 30.96) * mm, "end": v(26.04, 31.36) * mm});
            skLineSegment(sketch, "E399", {"start": v(26.04, 31.36) * mm, "end": v(25, 31.5) * mm});
            skLineSegment(sketch, "E400", {"start": v(25, 31.5) * mm, "end": v(23.96, 31.36) * mm});
            skLineSegment(sketch, "E401", {"start": v(23.96, 31.36) * mm, "end": v(23, 30.96) * mm});
            skLineSegment(sketch, "E402", {"start": v(23, 30.96) * mm, "end": v(22.17, 30.33) * mm});
            skLineSegment(sketch, "E403", {"start": v(22.17, 30.33) * mm, "end": v(21.54, 29.5) * mm});
            skLineSegment(sketch, "E404", {"start": v(21.54, 29.5) * mm, "end": v(21.14, 28.54) * mm});
            skLineSegment(sketch, "E405", {"start": v(21.14, 28.54) * mm, "end": v(21, 27.5) * mm});
            skLineSegment(sketch, "E406", {"start": v(21, 27.5) * mm, "end": v(21.14, 26.46) * mm});
            skLineSegment(sketch, "E407", {"start": v(21.14, 26.46) * mm, "end": v(21.54, 25.5) * mm});
            skLineSegment(sketch, "E408", {"start": v(21.54, 25.5) * mm, "end": v(22.17, 24.67) * mm});
            skLineSegment(sketch, "E409", {"start": v(22.17, 24.67) * mm, "end": v(23, 24.04) * mm});
            skLineSegment(sketch, "E410", {"start": v(23, 24.04) * mm, "end": v(23.96, 23.64) * mm});
            skLineSegment(sketch, "E411", {"start": v(23.96, 23.64) * mm, "end": v(25, 23.5) * mm});
            skLineSegment(sketch, "E412", {"start": v(25, 23.5) * mm, "end": v(26.04, 23.64) * mm});
            skLineSegment(sketch, "E413", {"start": v(26.04, 23.64) * mm, "end": v(27, 24.04) * mm});
            skLineSegment(sketch, "E414", {"start": v(27, 24.04) * mm, "end": v(27.83, 24.67) * mm});
            skLineSegment(sketch, "E415", {"start": v(27.83, 24.67) * mm, "end": v(28.46, 25.5) * mm});
            skLineSegment(sketch, "E416", {"start": v(28.46, 25.5) * mm, "end": v(28.86, 26.46) * mm});
            skLineSegment(sketch, "E417", {"start": v(28.86, 26.46) * mm, "end": v(29, 27.5) * mm});
            skLineSegment(sketch, "E418", {"start": v(29, 27.5) * mm, "end": v(28.86, 28.54) * mm});
            skSolve(sketch);
        }
        {
            var Q0;
            Q0=qCreatedBy(makeId("Right.planeOp"),FACE);
            cPlane(context, id + "F1", {"entities" : qUnion([Q0]), "cplaneType" : CPlaneType.OFFSET, "offset" : 100 * mm, "width" : 150 * mm, "height" : 150 * mm});
        }
        {
            var Q0;
            Q0=qCreatedBy(id+"F1.planeOp",FACE);
            var sketch = newSketch(context, id + "F2", { "sketchPlane" : qUnion([Q0])});
            skLineSegment(sketch, "E419", {"start": v(90, -12.5) * mm, "end": v(-145, -12.5) * mm});
            skLineSegment(sketch, "E420", {"start": v(-145, -12.5) * mm, "end": v(-145.65, -12.46) * mm});
            skLineSegment(sketch, "E421", {"start": v(-145.65, -12.46) * mm, "end": v(-146.3, -12.33) * mm});
            skLineSegment(sketch, "E422", {"start": v(-146.3, -12.33) * mm, "end": v(-146.91, -12.12) * mm});
            skLineSegment(sketch, "E423", {"start": v(-146.91, -12.12) * mm, "end": v(-147.5, -11.83) * mm});
            skLineSegment(sketch, "E424", {"start": v(-147.5, -11.83) * mm, "end": v(-148.04, -11.47) * mm});
            skLineSegment(sketch, "E425", {"start": v(-148.04, -11.47) * mm, "end": v(-148.54, -11.04) * mm});
            skLineSegment(sketch, "E426", {"start": v(-148.54, -11.04) * mm, "end": v(-148.97, -10.54) * mm});
            skLineSegment(sketch, "E427", {"start": v(-148.97, -10.54) * mm, "end": v(-149.33, -10) * mm});
            skLineSegment(sketch, "E428", {"start": v(-149.33, -10) * mm, "end": v(-149.62, -9.41) * mm});
            skLineSegment(sketch, "E429", {"start": v(-149.62, -9.41) * mm, "end": v(-149.83, -8.8) * mm});
            skLineSegment(sketch, "E430", {"start": v(-149.83, -8.8) * mm, "end": v(-149.96, -8.15) * mm});
            skLineSegment(sketch, "E431", {"start": v(-149.96, -8.15) * mm, "end": v(-150, -7.5) * mm});
            skLineSegment(sketch, "E432", {"start": v(-150, -7.5) * mm, "end": v(-150, 72.5) * mm});
            skLineSegment(sketch, "E433", {"start": v(-150, 72.5) * mm, "end": v(-50, 72.5) * mm});
            skLineSegment(sketch, "E434", {"start": v(-50, 72.5) * mm, "end": v(-50, 87.5) * mm});
            skLineSegment(sketch, "E435", {"start": v(-50, 87.5) * mm, "end": v(120, 87.5) * mm});
            skLineSegment(sketch, "E436", {"start": v(120, 87.5) * mm, "end": v(120.93, 87.34) * mm});
            skLineSegment(sketch, "E437", {"start": v(120.93, 87.34) * mm, "end": v(121.86, 87.13) * mm});
            skLineSegment(sketch, "E438", {"start": v(121.86, 87.13) * mm, "end": v(122.77, 86.87) * mm});
            skLineSegment(sketch, "E439", {"start": v(122.77, 86.87) * mm, "end": v(123.67, 86.57) * mm});
            skLineSegment(sketch, "E440", {"start": v(123.67, 86.57) * mm, "end": v(124.55, 86.21) * mm});
            skLineSegment(sketch, "E441", {"start": v(124.55, 86.21) * mm, "end": v(125.4, 85.81) * mm});
            skLineSegment(sketch, "E442", {"start": v(125.4, 85.81) * mm, "end": v(126.24, 85.36) * mm});
            skLineSegment(sketch, "E443", {"start": v(126.24, 85.36) * mm, "end": v(127.05, 84.87) * mm});
            skLineSegment(sketch, "E444", {"start": v(127.05, 84.87) * mm, "end": v(127.84, 84.34) * mm});
            skLineSegment(sketch, "E445", {"start": v(127.84, 84.34) * mm, "end": v(128.6, 83.77) * mm});
            skLineSegment(sketch, "E446", {"start": v(128.6, 83.77) * mm, "end": v(129.31, 83.15) * mm});
            skLineSegment(sketch, "E447", {"start": v(129.31, 83.15) * mm, "end": v(130, 82.5) * mm});
            skLineSegment(sketch, "E448", {"start": v(130, 82.5) * mm, "end": v(145, 67.5) * mm});
            skLineSegment(sketch, "E449", {"start": v(145, 67.5) * mm, "end": v(145.65, 66.81) * mm});
            skLineSegment(sketch, "E450", {"start": v(145.65, 66.81) * mm, "end": v(146.27, 66.1) * mm});
            skLineSegment(sketch, "E451", {"start": v(146.27, 66.1) * mm, "end": v(146.84, 65.34) * mm});
            skLineSegment(sketch, "E452", {"start": v(146.84, 65.34) * mm, "end": v(147.37, 64.55) * mm});
            skLineSegment(sketch, "E453", {"start": v(147.37, 64.55) * mm, "end": v(147.86, 63.74) * mm});
            skLineSegment(sketch, "E454", {"start": v(147.86, 63.74) * mm, "end": v(148.31, 62.9) * mm});
            skLineSegment(sketch, "E455", {"start": v(148.31, 62.9) * mm, "end": v(148.71, 62.05) * mm});
            skLineSegment(sketch, "E456", {"start": v(148.71, 62.05) * mm, "end": v(149.07, 61.17) * mm});
            skLineSegment(sketch, "E457", {"start": v(149.07, 61.17) * mm, "end": v(149.37, 60.27) * mm});
            skLineSegment(sketch, "E458", {"start": v(149.37, 60.27) * mm, "end": v(149.63, 59.36) * mm});
            skLineSegment(sketch, "E459", {"start": v(149.63, 59.36) * mm, "end": v(149.84, 58.43) * mm});
            skLineSegment(sketch, "E460", {"start": v(149.84, 58.43) * mm, "end": v(150, 57.5) * mm});
            skLineSegment(sketch, "E461", {"start": v(150, 57.5) * mm, "end": v(150, -82.5) * mm});
            skLineSegment(sketch, "E462", {"start": v(150, -82.5) * mm, "end": v(149.96, -83.15) * mm});
            skLineSegment(sketch, "E463", {"start": v(149.96, -83.15) * mm, "end": v(149.83, -83.8) * mm});
            skLineSegment(sketch, "E464", {"start": v(149.83, -83.8) * mm, "end": v(149.62, -84.41) * mm});
            skLineSegment(sketch, "E465", {"start": v(149.62, -84.41) * mm, "end": v(149.33, -85) * mm});
            skLineSegment(sketch, "E466", {"start": v(149.33, -85) * mm, "end": v(148.97, -85.54) * mm});
            skLineSegment(sketch, "E467", {"start": v(148.97, -85.54) * mm, "end": v(148.54, -86.04) * mm});
            skLineSegment(sketch, "E468", {"start": v(148.54, -86.04) * mm, "end": v(148.04, -86.47) * mm});
            skLineSegment(sketch, "E469", {"start": v(148.04, -86.47) * mm, "end": v(147.5, -86.83) * mm});
            skLineSegment(sketch, "E470", {"start": v(147.5, -86.83) * mm, "end": v(146.91, -87.12) * mm});
            skLineSegment(sketch, "E471", {"start": v(146.91, -87.12) * mm, "end": v(146.3, -87.33) * mm});
            skLineSegment(sketch, "E472", {"start": v(146.3, -87.33) * mm, "end": v(145.65, -87.46) * mm});
            skLineSegment(sketch, "E473", {"start": v(145.65, -87.46) * mm, "end": v(145, -87.5) * mm});
            skLineSegment(sketch, "E474", {"start": v(145, -87.5) * mm, "end": v(120, -87.5) * mm});
            skLineSegment(sketch, "E475", {"start": v(120, -87.5) * mm, "end": v(119.07, -87.34) * mm});
            skLineSegment(sketch, "E476", {"start": v(119.07, -87.34) * mm, "end": v(118.14, -87.13) * mm});
            skLineSegment(sketch, "E477", {"start": v(118.14, -87.13) * mm, "end": v(117.23, -86.87) * mm});
            skLineSegment(sketch, "E478", {"start": v(117.23, -86.87) * mm, "end": v(116.33, -86.57) * mm});
            skLineSegment(sketch, "E479", {"start": v(116.33, -86.57) * mm, "end": v(115.45, -86.21) * mm});
            skLineSegment(sketch, "E480", {"start": v(115.45, -86.21) * mm, "end": v(114.6, -85.81) * mm});
            skLineSegment(sketch, "E481", {"start": v(114.6, -85.81) * mm, "end": v(113.76, -85.36) * mm});
            skLineSegment(sketch, "E482", {"start": v(113.76, -85.36) * mm, "end": v(112.95, -84.87) * mm});
            skLineSegment(sketch, "E483", {"start": v(112.95, -84.87) * mm, "end": v(112.16, -84.34) * mm});
            skLineSegment(sketch, "E484", {"start": v(112.16, -84.34) * mm, "end": v(111.4, -83.77) * mm});
            skLineSegment(sketch, "E485", {"start": v(111.4, -83.77) * mm, "end": v(110.69, -83.15) * mm});
            skLineSegment(sketch, "E486", {"start": v(110.69, -83.15) * mm, "end": v(110, -82.5) * mm});
            skLineSegment(sketch, "E487", {"start": v(110, -82.5) * mm, "end": v(95, -67.5) * mm});
            skLineSegment(sketch, "E488", {"start": v(95, -67.5) * mm, "end": v(94.35, -66.81) * mm});
            skLineSegment(sketch, "E489", {"start": v(94.35, -66.81) * mm, "end": v(93.73, -66.1) * mm});
            skLineSegment(sketch, "E490", {"start": v(93.73, -66.1) * mm, "end": v(93.16, -65.34) * mm});
            skLineSegment(sketch, "E491", {"start": v(93.16, -65.34) * mm, "end": v(92.63, -64.55) * mm});
            skLineSegment(sketch, "E492", {"start": v(92.63, -64.55) * mm, "end": v(92.14, -63.74) * mm});
            skLineSegment(sketch, "E493", {"start": v(92.14, -63.74) * mm, "end": v(91.69, -62.9) * mm});
            skLineSegment(sketch, "E494", {"start": v(91.69, -62.9) * mm, "end": v(91.29, -62.05) * mm});
            skLineSegment(sketch, "E495", {"start": v(91.29, -62.05) * mm, "end": v(90.93, -61.17) * mm});
            skLineSegment(sketch, "E496", {"start": v(90.93, -61.17) * mm, "end": v(90.63, -60.27) * mm});
            skLineSegment(sketch, "E497", {"start": v(90.63, -60.27) * mm, "end": v(90.37, -59.36) * mm});
            skLineSegment(sketch, "E498", {"start": v(90.37, -59.36) * mm, "end": v(90.16, -58.43) * mm});
            skLineSegment(sketch, "E499", {"start": v(90.16, -58.43) * mm, "end": v(90, -57.5) * mm});
            skLineSegment(sketch, "E500", {"start": v(90, -57.5) * mm, "end": v(90, -12.5) * mm});
            skLineSegment(sketch, "E501", {"start": v(118, 0.96) * mm, "end": v(117.17, 0.33) * mm});
            skLineSegment(sketch, "E502", {"start": v(117.17, 0.33) * mm, "end": v(116.54, -0.5) * mm});
            skLineSegment(sketch, "E503", {"start": v(116.54, -0.5) * mm, "end": v(116.14, -1.46) * mm});
            skLineSegment(sketch, "E504", {"start": v(116.14, -1.46) * mm, "end": v(116, -2.5) * mm});
            skLineSegment(sketch, "E505", {"start": v(116, -2.5) * mm, "end": v(116.14, -3.54) * mm});
            skLineSegment(sketch, "E506", {"start": v(116.14, -3.54) * mm, "end": v(116.54, -4.5) * mm});
            skLineSegment(sketch, "E507", {"start": v(116.54, -4.5) * mm, "end": v(117.17, -5.33) * mm});
            skLineSegment(sketch, "E508", {"start": v(117.17, -5.33) * mm, "end": v(118, -5.96) * mm});
            skLineSegment(sketch, "E509", {"start": v(118, -5.96) * mm, "end": v(118.96, -6.36) * mm});
            skLineSegment(sketch, "E510", {"start": v(118.96, -6.36) * mm, "end": v(120, -6.5) * mm});
            skLineSegment(sketch, "E511", {"start": v(120, -6.5) * mm, "end": v(121.04, -6.36) * mm});
            skLineSegment(sketch, "E512", {"start": v(121.04, -6.36) * mm, "end": v(122, -5.96) * mm});
            skLineSegment(sketch, "E513", {"start": v(122, -5.96) * mm, "end": v(122.83, -5.33) * mm});
            skLineSegment(sketch, "E514", {"start": v(122.83, -5.33) * mm, "end": v(123.46, -4.5) * mm});
            skLineSegment(sketch, "E515", {"start": v(123.46, -4.5) * mm, "end": v(123.86, -3.54) * mm});
            skLineSegment(sketch, "E516", {"start": v(123.86, -3.54) * mm, "end": v(124, -2.5) * mm});
            skLineSegment(sketch, "E517", {"start": v(124, -2.5) * mm, "end": v(123.86, -1.46) * mm});
            skLineSegment(sketch, "E518", {"start": v(123.86, -1.46) * mm, "end": v(123.46, -0.5) * mm});
            skLineSegment(sketch, "E519", {"start": v(123.46, -0.5) * mm, "end": v(122.83, 0.33) * mm});
            skLineSegment(sketch, "E520", {"start": v(122.83, 0.33) * mm, "end": v(122, 0.96) * mm});
            skLineSegment(sketch, "E521", {"start": v(122, 0.96) * mm, "end": v(121.04, 1.36) * mm});
            skLineSegment(sketch, "E522", {"start": v(121.04, 1.36) * mm, "end": v(120, 1.5) * mm});
            skLineSegment(sketch, "E523", {"start": v(120, 1.5) * mm, "end": v(118.96, 1.36) * mm});
            skLineSegment(sketch, "E524", {"start": v(118.96, 1.36) * mm, "end": v(118, 0.96) * mm});
            skLineSegment(sketch, "E525", {"start": v(122, -70.96) * mm, "end": v(122.83, -70.33) * mm});
            skLineSegment(sketch, "E526", {"start": v(122.83, -70.33) * mm, "end": v(123.46, -69.5) * mm});
            skLineSegment(sketch, "E527", {"start": v(123.46, -69.5) * mm, "end": v(123.86, -68.54) * mm});
            skLineSegment(sketch, "E528", {"start": v(123.86, -68.54) * mm, "end": v(124, -67.5) * mm});
            skLineSegment(sketch, "E529", {"start": v(124, -67.5) * mm, "end": v(123.86, -66.46) * mm});
            skLineSegment(sketch, "E530", {"start": v(123.86, -66.46) * mm, "end": v(123.46, -65.5) * mm});
            skLineSegment(sketch, "E531", {"start": v(123.46, -65.5) * mm, "end": v(122.83, -64.67) * mm});
            skLineSegment(sketch, "E532", {"start": v(122.83, -64.67) * mm, "end": v(122, -64.04) * mm});
            skLineSegment(sketch, "E533", {"start": v(122, -64.04) * mm, "end": v(121.04, -63.64) * mm});
            skLineSegment(sketch, "E534", {"start": v(121.04, -63.64) * mm, "end": v(120, -63.5) * mm});
            skLineSegment(sketch, "E535", {"start": v(120, -63.5) * mm, "end": v(118.96, -63.64) * mm});
            skLineSegment(sketch, "E536", {"start": v(118.96, -63.64) * mm, "end": v(118, -64.04) * mm});
            skLineSegment(sketch, "E537", {"start": v(118, -64.04) * mm, "end": v(117.17, -64.67) * mm});
            skLineSegment(sketch, "E538", {"start": v(117.17, -64.67) * mm, "end": v(116.54, -65.5) * mm});
            skLineSegment(sketch, "E539", {"start": v(116.54, -65.5) * mm, "end": v(116.14, -66.46) * mm});
            skLineSegment(sketch, "E540", {"start": v(116.14, -66.46) * mm, "end": v(116, -67.5) * mm});
            skLineSegment(sketch, "E541", {"start": v(116, -67.5) * mm, "end": v(116.14, -68.54) * mm});
            skLineSegment(sketch, "E542", {"start": v(116.14, -68.54) * mm, "end": v(116.54, -69.5) * mm});
            skLineSegment(sketch, "E543", {"start": v(116.54, -69.5) * mm, "end": v(117.17, -70.33) * mm});
            skLineSegment(sketch, "E544", {"start": v(117.17, -70.33) * mm, "end": v(118, -70.96) * mm});
            skLineSegment(sketch, "E545", {"start": v(118, -70.96) * mm, "end": v(118.96, -71.36) * mm});
            skLineSegment(sketch, "E546", {"start": v(118.96, -71.36) * mm, "end": v(120, -71.5) * mm});
            skLineSegment(sketch, "E547", {"start": v(120, -71.5) * mm, "end": v(121.04, -71.36) * mm});
            skLineSegment(sketch, "E548", {"start": v(121.04, -71.36) * mm, "end": v(122, -70.96) * mm});
            skLineSegment(sketch, "E549", {"start": v(117.17, 59.67) * mm, "end": v(118, 59.04) * mm});
            skLineSegment(sketch, "E550", {"start": v(118, 59.04) * mm, "end": v(118.96, 58.64) * mm});
            skLineSegment(sketch, "E551", {"start": v(118.96, 58.64) * mm, "end": v(120, 58.5) * mm});
            skLineSegment(sketch, "E552", {"start": v(120, 58.5) * mm, "end": v(121.04, 58.64) * mm});
            skLineSegment(sketch, "E553", {"start": v(121.04, 58.64) * mm, "end": v(122, 59.04) * mm});
            skLineSegment(sketch, "E554", {"start": v(122, 59.04) * mm, "end": v(122.83, 59.67) * mm});
            skLineSegment(sketch, "E555", {"start": v(122.83, 59.67) * mm, "end": v(123.46, 60.5) * mm});
            skLineSegment(sketch, "E556", {"start": v(123.46, 60.5) * mm, "end": v(123.86, 61.46) * mm});
            skLineSegment(sketch, "E557", {"start": v(123.86, 61.46) * mm, "end": v(124, 62.5) * mm});
            skLineSegment(sketch, "E558", {"start": v(124, 62.5) * mm, "end": v(123.86, 63.54) * mm});
            skLineSegment(sketch, "E559", {"start": v(123.86, 63.54) * mm, "end": v(123.46, 64.5) * mm});
            skLineSegment(sketch, "E560", {"start": v(123.46, 64.5) * mm, "end": v(122.83, 65.33) * mm});
            skLineSegment(sketch, "E561", {"start": v(122.83, 65.33) * mm, "end": v(122, 65.96) * mm});
            skLineSegment(sketch, "E562", {"start": v(122, 65.96) * mm, "end": v(121.04, 66.36) * mm});
            skLineSegment(sketch, "E563", {"start": v(121.04, 66.36) * mm, "end": v(120, 66.5) * mm});
            skLineSegment(sketch, "E564", {"start": v(120, 66.5) * mm, "end": v(118.96, 66.36) * mm});
            skLineSegment(sketch, "E565", {"start": v(118.96, 66.36) * mm, "end": v(118, 65.96) * mm});
            skLineSegment(sketch, "E566", {"start": v(118, 65.96) * mm, "end": v(117.17, 65.33) * mm});
            skLineSegment(sketch, "E567", {"start": v(117.17, 65.33) * mm, "end": v(116.54, 64.5) * mm});
            skLineSegment(sketch, "E568", {"start": v(116.54, 64.5) * mm, "end": v(116.14, 63.54) * mm});
            skLineSegment(sketch, "E569", {"start": v(116.14, 63.54) * mm, "end": v(116, 62.5) * mm});
            skLineSegment(sketch, "E570", {"start": v(116, 62.5) * mm, "end": v(116.14, 61.46) * mm});
            skLineSegment(sketch, "E571", {"start": v(116.14, 61.46) * mm, "end": v(116.54, 60.5) * mm});
            skLineSegment(sketch, "E572", {"start": v(116.54, 60.5) * mm, "end": v(117.17, 59.67) * mm});
            skCircle(sketch, "E573", {"center": v(-125, 37.5) * mm, "radius": 4 * mm});
            skCircle(sketch, "E574", {"center": v(-25, 37.5) * mm, "radius": 4 * mm});
            skCircle(sketch, "E575", {"center": v(-75, 37.5) * mm, "radius": 11 * mm});
            skSolve(sketch);
        }
        {
            var Q0;
            Q0=qCreatedBy(makeId("Right.planeOp"),FACE);
            cPlane(context, id + "F3", {"entities" : qUnion([Q0]), "cplaneType" : CPlaneType.OFFSET, "offset" : 100 * mm, "oppositeDirection" : true, "width" : 150 * mm, "height" : 150 * mm});
        }
        {
            var Q0;
            Q0=qCreatedBy(id+"F3.planeOp",FACE);
            var sketch = newSketch(context, id + "F4", { "sketchPlane" : qUnion([Q0])});
            skLineSegment(sketch, "E576", {"start": v(-30, 23) * mm, "end": v(-30, 32) * mm});
            skLineSegment(sketch, "E577", {"start": v(-30, 32) * mm, "end": v(-29.96, 32.65) * mm});
            skLineSegment(sketch, "E578", {"start": v(-29.96, 32.65) * mm, "end": v(-29.83, 33.3) * mm});
            skLineSegment(sketch, "E579", {"start": v(-29.83, 33.3) * mm, "end": v(-29.62, 33.91) * mm});
            skLineSegment(sketch, "E580", {"start": v(-29.62, 33.91) * mm, "end": v(-29.33, 34.5) * mm});
            skLineSegment(sketch, "E581", {"start": v(-29.33, 34.5) * mm, "end": v(-28.97, 35.04) * mm});
            skLineSegment(sketch, "E582", {"start": v(-28.97, 35.04) * mm, "end": v(-28.54, 35.54) * mm});
            skLineSegment(sketch, "E583", {"start": v(-28.54, 35.54) * mm, "end": v(-28.04, 35.97) * mm});
            skLineSegment(sketch, "E584", {"start": v(-28.04, 35.97) * mm, "end": v(-27.5, 36.33) * mm});
            skLineSegment(sketch, "E585", {"start": v(-27.5, 36.33) * mm, "end": v(-26.91, 36.62) * mm});
            skLineSegment(sketch, "E586", {"start": v(-26.91, 36.62) * mm, "end": v(-26.3, 36.83) * mm});
            skLineSegment(sketch, "E587", {"start": v(-26.3, 36.83) * mm, "end": v(-25.65, 36.96) * mm});
            skLineSegment(sketch, "E588", {"start": v(-25.65, 36.96) * mm, "end": v(-25, 37) * mm});
            skLineSegment(sketch, "E589", {"start": v(-25, 37) * mm, "end": v(25, 37) * mm});
            skLineSegment(sketch, "E590", {"start": v(25, 37) * mm, "end": v(25.65, 36.96) * mm});
            skLineSegment(sketch, "E591", {"start": v(25.65, 36.96) * mm, "end": v(26.3, 36.83) * mm});
            skLineSegment(sketch, "E592", {"start": v(26.3, 36.83) * mm, "end": v(26.91, 36.62) * mm});
            skLineSegment(sketch, "E593", {"start": v(26.91, 36.62) * mm, "end": v(27.5, 36.33) * mm});
            skLineSegment(sketch, "E594", {"start": v(27.5, 36.33) * mm, "end": v(28.04, 35.97) * mm});
            skLineSegment(sketch, "E595", {"start": v(28.04, 35.97) * mm, "end": v(28.54, 35.54) * mm});
            skLineSegment(sketch, "E596", {"start": v(28.54, 35.54) * mm, "end": v(28.97, 35.04) * mm});
            skLineSegment(sketch, "E597", {"start": v(28.97, 35.04) * mm, "end": v(29.33, 34.5) * mm});
            skLineSegment(sketch, "E598", {"start": v(29.33, 34.5) * mm, "end": v(29.62, 33.91) * mm});
            skLineSegment(sketch, "E599", {"start": v(29.62, 33.91) * mm, "end": v(29.83, 33.3) * mm});
            skLineSegment(sketch, "E600", {"start": v(29.83, 33.3) * mm, "end": v(29.96, 32.65) * mm});
            skLineSegment(sketch, "E601", {"start": v(29.96, 32.65) * mm, "end": v(30, 32) * mm});
            skLineSegment(sketch, "E602", {"start": v(30, 32) * mm, "end": v(30, 23) * mm});
            skLineSegment(sketch, "E603", {"start": v(30, 23) * mm, "end": v(200, 23) * mm});
            skLineSegment(sketch, "E604", {"start": v(200, 23) * mm, "end": v(200, -37) * mm});
            skLineSegment(sketch, "E605", {"start": v(200, -37) * mm, "end": v(-200, -37) * mm});
            skLineSegment(sketch, "E606", {"start": v(-200, -37) * mm, "end": v(-200, 23) * mm});
            skLineSegment(sketch, "E607", {"start": v(-200, 23) * mm, "end": v(-30, 23) * mm});
            skLineSegment(sketch, "E608", {"start": v(-0.39, -12.47) * mm, "end": v(-0.75, -12.62) * mm});
            skLineSegment(sketch, "E609", {"start": v(-0.75, -12.62) * mm, "end": v(-1.06, -12.86) * mm});
            skLineSegment(sketch, "E610", {"start": v(-1.06, -12.86) * mm, "end": v(-1.3, -13.17) * mm});
            skLineSegment(sketch, "E611", {"start": v(-1.3, -13.17) * mm, "end": v(-1.45, -13.53) * mm});
            skLineSegment(sketch, "E612", {"start": v(-1.45, -13.53) * mm, "end": v(-1.5, -13.92) * mm});
            skLineSegment(sketch, "E613", {"start": v(-1.5, -13.92) * mm, "end": v(-1.45, -14.3) * mm});
            skLineSegment(sketch, "E614", {"start": v(-1.45, -14.3) * mm, "end": v(-1.3, -14.67) * mm});
            skLineSegment(sketch, "E615", {"start": v(-1.3, -14.67) * mm, "end": v(-1.06, -14.98) * mm});
            skLineSegment(sketch, "E616", {"start": v(-1.06, -14.98) * mm, "end": v(-0.75, -15.22) * mm});
            skLineSegment(sketch, "E617", {"start": v(-0.75, -15.22) * mm, "end": v(-0.39, -15.37) * mm});
            skLineSegment(sketch, "E618", {"start": v(-0.39, -15.37) * mm, "end": v(0, -15.42) * mm});
            skLineSegment(sketch, "E619", {"start": v(0, -15.42) * mm, "end": v(0.39, -15.37) * mm});
            skLineSegment(sketch, "E620", {"start": v(0.39, -15.37) * mm, "end": v(0.75, -15.22) * mm});
            skLineSegment(sketch, "E621", {"start": v(0.75, -15.22) * mm, "end": v(1.06, -14.98) * mm});
            skLineSegment(sketch, "E622", {"start": v(1.06, -14.98) * mm, "end": v(1.3, -14.67) * mm});
            skLineSegment(sketch, "E623", {"start": v(1.3, -14.67) * mm, "end": v(1.45, -14.3) * mm});
            skLineSegment(sketch, "E624", {"start": v(1.45, -14.3) * mm, "end": v(1.5, -13.92) * mm});
            skLineSegment(sketch, "E625", {"start": v(1.5, -13.92) * mm, "end": v(1.45, -13.53) * mm});
            skLineSegment(sketch, "E626", {"start": v(1.45, -13.53) * mm, "end": v(1.3, -13.17) * mm});
            skLineSegment(sketch, "E627", {"start": v(1.3, -13.17) * mm, "end": v(1.06, -12.86) * mm});
            skLineSegment(sketch, "E628", {"start": v(1.06, -12.86) * mm, "end": v(0.75, -12.62) * mm});
            skLineSegment(sketch, "E629", {"start": v(0.75, -12.62) * mm, "end": v(0.39, -12.47) * mm});
            skLineSegment(sketch, "E630", {"start": v(0.39, -12.47) * mm, "end": v(0, -12.42) * mm});
            skLineSegment(sketch, "E631", {"start": v(0, -12.42) * mm, "end": v(-0.39, -12.47) * mm});
            skLineSegment(sketch, "E632", {"start": v(21.17, 9.3) * mm, "end": v(20.86, 9.06) * mm});
            skLineSegment(sketch, "E633", {"start": v(20.86, 9.06) * mm, "end": v(20.62, 8.75) * mm});
            skLineSegment(sketch, "E634", {"start": v(20.62, 8.75) * mm, "end": v(20.47, 8.39) * mm});
            skLineSegment(sketch, "E635", {"start": v(20.47, 8.39) * mm, "end": v(20.42, 8) * mm});
            skLineSegment(sketch, "E636", {"start": v(20.42, 8) * mm, "end": v(20.47, 7.61) * mm});
            skLineSegment(sketch, "E637", {"start": v(20.47, 7.61) * mm, "end": v(20.62, 7.25) * mm});
            skLineSegment(sketch, "E638", {"start": v(20.62, 7.25) * mm, "end": v(20.86, 6.94) * mm});
            skLineSegment(sketch, "E639", {"start": v(20.86, 6.94) * mm, "end": v(21.17, 6.7) * mm});
            skLineSegment(sketch, "E640", {"start": v(21.17, 6.7) * mm, "end": v(21.53, 6.55) * mm});
            skLineSegment(sketch, "E641", {"start": v(21.53, 6.55) * mm, "end": v(21.92, 6.5) * mm});
            skLineSegment(sketch, "E642", {"start": v(21.92, 6.5) * mm, "end": v(22.3, 6.55) * mm});
            skLineSegment(sketch, "E643", {"start": v(22.3, 6.55) * mm, "end": v(22.67, 6.7) * mm});
            skLineSegment(sketch, "E644", {"start": v(22.67, 6.7) * mm, "end": v(22.98, 6.94) * mm});
            skLineSegment(sketch, "E645", {"start": v(22.98, 6.94) * mm, "end": v(23.22, 7.25) * mm});
            skLineSegment(sketch, "E646", {"start": v(23.22, 7.25) * mm, "end": v(23.37, 7.61) * mm});
            skLineSegment(sketch, "E647", {"start": v(23.37, 7.61) * mm, "end": v(23.42, 8) * mm});
            skLineSegment(sketch, "E648", {"start": v(23.42, 8) * mm, "end": v(23.37, 8.39) * mm});
            skLineSegment(sketch, "E649", {"start": v(23.37, 8.39) * mm, "end": v(23.22, 8.75) * mm});
            skLineSegment(sketch, "E650", {"start": v(23.22, 8.75) * mm, "end": v(22.98, 9.06) * mm});
            skLineSegment(sketch, "E651", {"start": v(22.98, 9.06) * mm, "end": v(22.67, 9.3) * mm});
            skLineSegment(sketch, "E652", {"start": v(22.67, 9.3) * mm, "end": v(22.3, 9.45) * mm});
            skLineSegment(sketch, "E653", {"start": v(22.3, 9.45) * mm, "end": v(21.92, 9.5) * mm});
            skLineSegment(sketch, "E654", {"start": v(21.92, 9.5) * mm, "end": v(21.53, 9.45) * mm});
            skLineSegment(sketch, "E655", {"start": v(21.53, 9.45) * mm, "end": v(21.17, 9.3) * mm});
            skLineSegment(sketch, "E656", {"start": v(-22.98, 9.06) * mm, "end": v(-23.22, 8.75) * mm});
            skLineSegment(sketch, "E657", {"start": v(-23.22, 8.75) * mm, "end": v(-23.37, 8.39) * mm});
            skLineSegment(sketch, "E658", {"start": v(-23.37, 8.39) * mm, "end": v(-23.42, 8) * mm});
            skLineSegment(sketch, "E659", {"start": v(-23.42, 8) * mm, "end": v(-23.37, 7.61) * mm});
            skLineSegment(sketch, "E660", {"start": v(-23.37, 7.61) * mm, "end": v(-23.22, 7.25) * mm});
            skLineSegment(sketch, "E661", {"start": v(-23.22, 7.25) * mm, "end": v(-22.98, 6.94) * mm});
            skLineSegment(sketch, "E662", {"start": v(-22.98, 6.94) * mm, "end": v(-22.67, 6.7) * mm});
            skLineSegment(sketch, "E663", {"start": v(-22.67, 6.7) * mm, "end": v(-22.3, 6.55) * mm});
            skLineSegment(sketch, "E664", {"start": v(-22.3, 6.55) * mm, "end": v(-21.92, 6.5) * mm});
            skLineSegment(sketch, "E665", {"start": v(-21.92, 6.5) * mm, "end": v(-21.53, 6.55) * mm});
            skLineSegment(sketch, "E666", {"start": v(-21.53, 6.55) * mm, "end": v(-21.17, 6.7) * mm});
            skLineSegment(sketch, "E667", {"start": v(-21.17, 6.7) * mm, "end": v(-20.86, 6.94) * mm});
            skLineSegment(sketch, "E668", {"start": v(-20.86, 6.94) * mm, "end": v(-20.62, 7.25) * mm});
            skLineSegment(sketch, "E669", {"start": v(-20.62, 7.25) * mm, "end": v(-20.47, 7.61) * mm});
            skLineSegment(sketch, "E670", {"start": v(-20.47, 7.61) * mm, "end": v(-20.42, 8) * mm});
            skLineSegment(sketch, "E671", {"start": v(-20.42, 8) * mm, "end": v(-20.47, 8.39) * mm});
            skLineSegment(sketch, "E672", {"start": v(-20.47, 8.39) * mm, "end": v(-20.62, 8.75) * mm});
            skLineSegment(sketch, "E673", {"start": v(-20.62, 8.75) * mm, "end": v(-20.86, 9.06) * mm});
            skLineSegment(sketch, "E674", {"start": v(-20.86, 9.06) * mm, "end": v(-21.17, 9.3) * mm});
            skLineSegment(sketch, "E675", {"start": v(-21.17, 9.3) * mm, "end": v(-21.53, 9.45) * mm});
            skLineSegment(sketch, "E676", {"start": v(-21.53, 9.45) * mm, "end": v(-21.92, 9.5) * mm});
            skLineSegment(sketch, "E677", {"start": v(-21.92, 9.5) * mm, "end": v(-22.3, 9.45) * mm});
            skLineSegment(sketch, "E678", {"start": v(-22.3, 9.45) * mm, "end": v(-22.67, 9.3) * mm});
            skLineSegment(sketch, "E679", {"start": v(-22.67, 9.3) * mm, "end": v(-22.98, 9.06) * mm});
            skLineSegment(sketch, "E680", {"start": v(-1.3, 29.17) * mm, "end": v(-1.06, 28.86) * mm});
            skLineSegment(sketch, "E681", {"start": v(-1.06, 28.86) * mm, "end": v(-0.75, 28.62) * mm});
            skLineSegment(sketch, "E682", {"start": v(-0.75, 28.62) * mm, "end": v(-0.39, 28.47) * mm});
            skLineSegment(sketch, "E683", {"start": v(-0.39, 28.47) * mm, "end": v(0, 28.42) * mm});
            skLineSegment(sketch, "E684", {"start": v(0, 28.42) * mm, "end": v(0.39, 28.47) * mm});
            skLineSegment(sketch, "E685", {"start": v(0.39, 28.47) * mm, "end": v(0.75, 28.62) * mm});
            skLineSegment(sketch, "E686", {"start": v(0.75, 28.62) * mm, "end": v(1.06, 28.86) * mm});
            skLineSegment(sketch, "E687", {"start": v(1.06, 28.86) * mm, "end": v(1.3, 29.17) * mm});
            skLineSegment(sketch, "E688", {"start": v(1.3, 29.17) * mm, "end": v(1.45, 29.53) * mm});
            skLineSegment(sketch, "E689", {"start": v(1.45, 29.53) * mm, "end": v(1.5, 29.92) * mm});
            skLineSegment(sketch, "E690", {"start": v(1.5, 29.92) * mm, "end": v(1.45, 30.3) * mm});
            skLineSegment(sketch, "E691", {"start": v(1.45, 30.3) * mm, "end": v(1.3, 30.67) * mm});
            skLineSegment(sketch, "E692", {"start": v(1.3, 30.67) * mm, "end": v(1.06, 30.98) * mm});
            skLineSegment(sketch, "E693", {"start": v(1.06, 30.98) * mm, "end": v(0.75, 31.22) * mm});
            skLineSegment(sketch, "E694", {"start": v(0.75, 31.22) * mm, "end": v(0.39, 31.37) * mm});
            skLineSegment(sketch, "E695", {"start": v(0.39, 31.37) * mm, "end": v(0, 31.42) * mm});
            skLineSegment(sketch, "E696", {"start": v(0, 31.42) * mm, "end": v(-0.39, 31.37) * mm});
            skLineSegment(sketch, "E697", {"start": v(-0.39, 31.37) * mm, "end": v(-0.75, 31.22) * mm});
            skLineSegment(sketch, "E698", {"start": v(-0.75, 31.22) * mm, "end": v(-1.06, 30.98) * mm});
            skLineSegment(sketch, "E699", {"start": v(-1.06, 30.98) * mm, "end": v(-1.3, 30.67) * mm});
            skLineSegment(sketch, "E700", {"start": v(-1.3, 30.67) * mm, "end": v(-1.45, 30.3) * mm});
            skLineSegment(sketch, "E701", {"start": v(-1.45, 30.3) * mm, "end": v(-1.5, 29.92) * mm});
            skLineSegment(sketch, "E702", {"start": v(-1.5, 29.92) * mm, "end": v(-1.45, 29.53) * mm});
            skLineSegment(sketch, "E703", {"start": v(-1.45, 29.53) * mm, "end": v(-1.3, 29.17) * mm});
            skLineSegment(sketch, "E704", {"start": v(-8.49, 16.49) * mm, "end": v(-10.4, 14) * mm});
            skLineSegment(sketch, "E705", {"start": v(-10.4, 14) * mm, "end": v(-11.6, 11.1) * mm});
            skLineSegment(sketch, "E706", {"start": v(-11.6, 11.1) * mm, "end": v(-12, 8) * mm});
            skLineSegment(sketch, "E707", {"start": v(-12, 8) * mm, "end": v(-11.6, 4.9) * mm});
            skLineSegment(sketch, "E708", {"start": v(-11.6, 4.9) * mm, "end": v(-10.4, 2) * mm});
            skLineSegment(sketch, "E709", {"start": v(-10.4, 2) * mm, "end": v(-8.49, -0.49) * mm});
            skLineSegment(sketch, "E710", {"start": v(-8.49, -0.49) * mm, "end": v(-6, -2.4) * mm});
            skLineSegment(sketch, "E711", {"start": v(-6, -2.4) * mm, "end": v(-3.1, -3.6) * mm});
            skLineSegment(sketch, "E712", {"start": v(-3.1, -3.6) * mm, "end": v(0, -4) * mm});
            skLineSegment(sketch, "E713", {"start": v(0, -4) * mm, "end": v(3.1, -3.6) * mm});
            skLineSegment(sketch, "E714", {"start": v(3.1, -3.6) * mm, "end": v(6, -2.4) * mm});
            skLineSegment(sketch, "E715", {"start": v(6, -2.4) * mm, "end": v(8.49, -0.49) * mm});
            skLineSegment(sketch, "E716", {"start": v(8.49, -0.49) * mm, "end": v(10.4, 2) * mm});
            skLineSegment(sketch, "E717", {"start": v(10.4, 2) * mm, "end": v(11.6, 4.9) * mm});
            skLineSegment(sketch, "E718", {"start": v(11.6, 4.9) * mm, "end": v(12, 8) * mm});
            skLineSegment(sketch, "E719", {"start": v(12, 8) * mm, "end": v(11.6, 11.1) * mm});
            skLineSegment(sketch, "E720", {"start": v(11.6, 11.1) * mm, "end": v(10.4, 14) * mm});
            skLineSegment(sketch, "E721", {"start": v(10.4, 14) * mm, "end": v(8.49, 16.49) * mm});
            skLineSegment(sketch, "E722", {"start": v(8.49, 16.49) * mm, "end": v(6, 18.4) * mm});
            skLineSegment(sketch, "E723", {"start": v(6, 18.4) * mm, "end": v(3.1, 19.6) * mm});
            skLineSegment(sketch, "E724", {"start": v(3.1, 19.6) * mm, "end": v(0, 20) * mm});
            skLineSegment(sketch, "E725", {"start": v(0, 20) * mm, "end": v(-3.1, 19.6) * mm});
            skLineSegment(sketch, "E726", {"start": v(-3.1, 19.6) * mm, "end": v(-6, 18.4) * mm});
            skLineSegment(sketch, "E727", {"start": v(-6, 18.4) * mm, "end": v(-8.49, 16.49) * mm});
            skLineSegment(sketch, "E728", {"start": v(23.94, -14.1) * mm, "end": v(23.55, -14.05) * mm});
            skLineSegment(sketch, "E729", {"start": v(23.55, -14.05) * mm, "end": v(23.16, -14.1) * mm});
            skLineSegment(sketch, "E730", {"start": v(23.16, -14.1) * mm, "end": v(22.8, -14.25) * mm});
            skLineSegment(sketch, "E731", {"start": v(22.8, -14.25) * mm, "end": v(22.49, -14.49) * mm});
            skLineSegment(sketch, "E732", {"start": v(22.49, -14.49) * mm, "end": v(22.25, -14.8) * mm});
            skLineSegment(sketch, "E733", {"start": v(22.25, -14.8) * mm, "end": v(22.1, -15.16) * mm});
            skLineSegment(sketch, "E734", {"start": v(22.1, -15.16) * mm, "end": v(22.05, -15.55) * mm});
            skLineSegment(sketch, "E735", {"start": v(22.05, -15.55) * mm, "end": v(22.1, -15.94) * mm});
            skLineSegment(sketch, "E736", {"start": v(22.1, -15.94) * mm, "end": v(22.25, -16.3) * mm});
            skLineSegment(sketch, "E737", {"start": v(22.25, -16.3) * mm, "end": v(22.49, -16.61) * mm});
            skLineSegment(sketch, "E738", {"start": v(22.49, -16.61) * mm, "end": v(22.8, -16.85) * mm});
            skLineSegment(sketch, "E739", {"start": v(22.8, -16.85) * mm, "end": v(23.16, -17) * mm});
            skLineSegment(sketch, "E740", {"start": v(23.16, -17) * mm, "end": v(23.55, -17.05) * mm});
            skLineSegment(sketch, "E741", {"start": v(23.55, -17.05) * mm, "end": v(23.94, -17) * mm});
            skLineSegment(sketch, "E742", {"start": v(23.94, -17) * mm, "end": v(24.3, -16.85) * mm});
            skLineSegment(sketch, "E743", {"start": v(24.3, -16.85) * mm, "end": v(24.61, -16.61) * mm});
            skLineSegment(sketch, "E744", {"start": v(24.61, -16.61) * mm, "end": v(24.85, -16.3) * mm});
            skLineSegment(sketch, "E745", {"start": v(24.85, -16.3) * mm, "end": v(25, -15.94) * mm});
            skLineSegment(sketch, "E746", {"start": v(25, -15.94) * mm, "end": v(25.05, -15.55) * mm});
            skLineSegment(sketch, "E747", {"start": v(25.05, -15.55) * mm, "end": v(25, -15.16) * mm});
            skLineSegment(sketch, "E748", {"start": v(25, -15.16) * mm, "end": v(24.85, -14.8) * mm});
            skLineSegment(sketch, "E749", {"start": v(24.85, -14.8) * mm, "end": v(24.61, -14.49) * mm});
            skLineSegment(sketch, "E750", {"start": v(24.61, -14.49) * mm, "end": v(24.3, -14.25) * mm});
            skLineSegment(sketch, "E751", {"start": v(24.3, -14.25) * mm, "end": v(23.94, -14.1) * mm});
            skLineSegment(sketch, "E752", {"start": v(-25, -15.94) * mm, "end": v(-24.85, -16.3) * mm});
            skLineSegment(sketch, "E753", {"start": v(-24.85, -16.3) * mm, "end": v(-24.61, -16.61) * mm});
            skLineSegment(sketch, "E754", {"start": v(-24.61, -16.61) * mm, "end": v(-24.3, -16.85) * mm});
            skLineSegment(sketch, "E755", {"start": v(-24.3, -16.85) * mm, "end": v(-23.94, -17) * mm});
            skLineSegment(sketch, "E756", {"start": v(-23.94, -17) * mm, "end": v(-23.55, -17.05) * mm});
            skLineSegment(sketch, "E757", {"start": v(-23.55, -17.05) * mm, "end": v(-23.16, -17) * mm});
            skLineSegment(sketch, "E758", {"start": v(-23.16, -17) * mm, "end": v(-22.8, -16.85) * mm});
            skLineSegment(sketch, "E759", {"start": v(-22.8, -16.85) * mm, "end": v(-22.49, -16.61) * mm});
            skLineSegment(sketch, "E760", {"start": v(-22.49, -16.61) * mm, "end": v(-22.25, -16.3) * mm});
            skLineSegment(sketch, "E761", {"start": v(-22.25, -16.3) * mm, "end": v(-22.1, -15.94) * mm});
            skLineSegment(sketch, "E762", {"start": v(-22.1, -15.94) * mm, "end": v(-22.05, -15.55) * mm});
            skLineSegment(sketch, "E763", {"start": v(-22.05, -15.55) * mm, "end": v(-22.1, -15.16) * mm});
            skLineSegment(sketch, "E764", {"start": v(-22.1, -15.16) * mm, "end": v(-22.25, -14.8) * mm});
            skLineSegment(sketch, "E765", {"start": v(-22.25, -14.8) * mm, "end": v(-22.49, -14.49) * mm});
            skLineSegment(sketch, "E766", {"start": v(-22.49, -14.49) * mm, "end": v(-22.8, -14.25) * mm});
            skLineSegment(sketch, "E767", {"start": v(-22.8, -14.25) * mm, "end": v(-23.16, -14.1) * mm});
            skLineSegment(sketch, "E768", {"start": v(-23.16, -14.1) * mm, "end": v(-23.55, -14.05) * mm});
            skLineSegment(sketch, "E769", {"start": v(-23.55, -14.05) * mm, "end": v(-23.94, -14.1) * mm});
            skLineSegment(sketch, "E770", {"start": v(-23.94, -14.1) * mm, "end": v(-24.3, -14.25) * mm});
            skLineSegment(sketch, "E771", {"start": v(-24.3, -14.25) * mm, "end": v(-24.61, -14.49) * mm});
            skLineSegment(sketch, "E772", {"start": v(-24.61, -14.49) * mm, "end": v(-24.85, -14.8) * mm});
            skLineSegment(sketch, "E773", {"start": v(-24.85, -14.8) * mm, "end": v(-25, -15.16) * mm});
            skLineSegment(sketch, "E774", {"start": v(-25, -15.16) * mm, "end": v(-25.05, -15.55) * mm});
            skLineSegment(sketch, "E775", {"start": v(-25.05, -15.55) * mm, "end": v(-25, -15.94) * mm});
            skLineSegment(sketch, "E776", {"start": v(-22.1, 31.16) * mm, "end": v(-22.05, 31.55) * mm});
            skLineSegment(sketch, "E777", {"start": v(-22.05, 31.55) * mm, "end": v(-22.1, 31.94) * mm});
            skLineSegment(sketch, "E778", {"start": v(-22.1, 31.94) * mm, "end": v(-22.25, 32.3) * mm});
            skLineSegment(sketch, "E779", {"start": v(-22.25, 32.3) * mm, "end": v(-22.49, 32.61) * mm});
            skLineSegment(sketch, "E780", {"start": v(-22.49, 32.61) * mm, "end": v(-22.8, 32.85) * mm});
            skLineSegment(sketch, "E781", {"start": v(-22.8, 32.85) * mm, "end": v(-23.16, 33) * mm});
            skLineSegment(sketch, "E782", {"start": v(-23.16, 33) * mm, "end": v(-23.55, 33.05) * mm});
            skLineSegment(sketch, "E783", {"start": v(-23.55, 33.05) * mm, "end": v(-23.94, 33) * mm});
            skLineSegment(sketch, "E784", {"start": v(-23.94, 33) * mm, "end": v(-24.3, 32.85) * mm});
            skLineSegment(sketch, "E785", {"start": v(-24.3, 32.85) * mm, "end": v(-24.61, 32.61) * mm});
            skLineSegment(sketch, "E786", {"start": v(-24.61, 32.61) * mm, "end": v(-24.85, 32.3) * mm});
            skLineSegment(sketch, "E787", {"start": v(-24.85, 32.3) * mm, "end": v(-25, 31.94) * mm});
            skLineSegment(sketch, "E788", {"start": v(-25, 31.94) * mm, "end": v(-25.05, 31.55) * mm});
            skLineSegment(sketch, "E789", {"start": v(-25.05, 31.55) * mm, "end": v(-25, 31.16) * mm});
            skLineSegment(sketch, "E790", {"start": v(-25, 31.16) * mm, "end": v(-24.85, 30.8) * mm});
            skLineSegment(sketch, "E791", {"start": v(-24.85, 30.8) * mm, "end": v(-24.61, 30.49) * mm});
            skLineSegment(sketch, "E792", {"start": v(-24.61, 30.49) * mm, "end": v(-24.3, 30.25) * mm});
            skLineSegment(sketch, "E793", {"start": v(-24.3, 30.25) * mm, "end": v(-23.94, 30.1) * mm});
            skLineSegment(sketch, "E794", {"start": v(-23.94, 30.1) * mm, "end": v(-23.55, 30.05) * mm});
            skLineSegment(sketch, "E795", {"start": v(-23.55, 30.05) * mm, "end": v(-23.16, 30.1) * mm});
            skLineSegment(sketch, "E796", {"start": v(-23.16, 30.1) * mm, "end": v(-22.8, 30.25) * mm});
            skLineSegment(sketch, "E797", {"start": v(-22.8, 30.25) * mm, "end": v(-22.49, 30.49) * mm});
            skLineSegment(sketch, "E798", {"start": v(-22.49, 30.49) * mm, "end": v(-22.25, 30.8) * mm});
            skLineSegment(sketch, "E799", {"start": v(-22.25, 30.8) * mm, "end": v(-22.1, 31.16) * mm});
            skLineSegment(sketch, "E800", {"start": v(24.3, 30.25) * mm, "end": v(24.61, 30.49) * mm});
            skLineSegment(sketch, "E801", {"start": v(24.61, 30.49) * mm, "end": v(24.85, 30.8) * mm});
            skLineSegment(sketch, "E802", {"start": v(24.85, 30.8) * mm, "end": v(25, 31.16) * mm});
            skLineSegment(sketch, "E803", {"start": v(25, 31.16) * mm, "end": v(25.05, 31.55) * mm});
            skLineSegment(sketch, "E804", {"start": v(25.05, 31.55) * mm, "end": v(25, 31.94) * mm});
            skLineSegment(sketch, "E805", {"start": v(25, 31.94) * mm, "end": v(24.85, 32.3) * mm});
            skLineSegment(sketch, "E806", {"start": v(24.85, 32.3) * mm, "end": v(24.61, 32.61) * mm});
            skLineSegment(sketch, "E807", {"start": v(24.61, 32.61) * mm, "end": v(24.3, 32.85) * mm});
            skLineSegment(sketch, "E808", {"start": v(24.3, 32.85) * mm, "end": v(23.94, 33) * mm});
            skLineSegment(sketch, "E809", {"start": v(23.94, 33) * mm, "end": v(23.55, 33.05) * mm});
            skLineSegment(sketch, "E810", {"start": v(23.55, 33.05) * mm, "end": v(23.16, 33) * mm});
            skLineSegment(sketch, "E811", {"start": v(23.16, 33) * mm, "end": v(22.8, 32.85) * mm});
            skLineSegment(sketch, "E812", {"start": v(22.8, 32.85) * mm, "end": v(22.49, 32.61) * mm});
            skLineSegment(sketch, "E813", {"start": v(22.49, 32.61) * mm, "end": v(22.25, 32.3) * mm});
            skLineSegment(sketch, "E814", {"start": v(22.25, 32.3) * mm, "end": v(22.1, 31.94) * mm});
            skLineSegment(sketch, "E815", {"start": v(22.1, 31.94) * mm, "end": v(22.05, 31.55) * mm});
            skLineSegment(sketch, "E816", {"start": v(22.05, 31.55) * mm, "end": v(22.1, 31.16) * mm});
            skLineSegment(sketch, "E817", {"start": v(22.1, 31.16) * mm, "end": v(22.25, 30.8) * mm});
            skLineSegment(sketch, "E818", {"start": v(22.25, 30.8) * mm, "end": v(22.49, 30.49) * mm});
            skLineSegment(sketch, "E819", {"start": v(22.49, 30.49) * mm, "end": v(22.8, 30.25) * mm});
            skLineSegment(sketch, "E820", {"start": v(22.8, 30.25) * mm, "end": v(23.16, 30.1) * mm});
            skLineSegment(sketch, "E821", {"start": v(23.16, 30.1) * mm, "end": v(23.55, 30.05) * mm});
            skLineSegment(sketch, "E822", {"start": v(23.55, 30.05) * mm, "end": v(23.94, 30.1) * mm});
            skLineSegment(sketch, "E823", {"start": v(23.94, 30.1) * mm, "end": v(24.3, 30.25) * mm});
            skLineSegment(sketch, "E824", {"start": v(192.11, 14.45) * mm, "end": v(191.75, 14.3) * mm});
            skLineSegment(sketch, "E825", {"start": v(191.75, 14.3) * mm, "end": v(191.44, 14.06) * mm});
            skLineSegment(sketch, "E826", {"start": v(191.44, 14.06) * mm, "end": v(191.2, 13.75) * mm});
            skLineSegment(sketch, "E827", {"start": v(191.2, 13.75) * mm, "end": v(191.05, 13.39) * mm});
            skLineSegment(sketch, "E828", {"start": v(191.05, 13.39) * mm, "end": v(191, 13) * mm});
            skLineSegment(sketch, "E829", {"start": v(191, 13) * mm, "end": v(191.05, 12.61) * mm});
            skLineSegment(sketch, "E830", {"start": v(191.05, 12.61) * mm, "end": v(191.2, 12.25) * mm});
            skLineSegment(sketch, "E831", {"start": v(191.2, 12.25) * mm, "end": v(191.44, 11.94) * mm});
            skLineSegment(sketch, "E832", {"start": v(191.44, 11.94) * mm, "end": v(191.75, 11.7) * mm});
            skLineSegment(sketch, "E833", {"start": v(191.75, 11.7) * mm, "end": v(192.11, 11.55) * mm});
            skLineSegment(sketch, "E834", {"start": v(192.11, 11.55) * mm, "end": v(192.5, 11.5) * mm});
            skLineSegment(sketch, "E835", {"start": v(192.5, 11.5) * mm, "end": v(192.89, 11.55) * mm});
            skLineSegment(sketch, "E836", {"start": v(192.89, 11.55) * mm, "end": v(193.25, 11.7) * mm});
            skLineSegment(sketch, "E837", {"start": v(193.25, 11.7) * mm, "end": v(193.56, 11.94) * mm});
            skLineSegment(sketch, "E838", {"start": v(193.56, 11.94) * mm, "end": v(193.8, 12.25) * mm});
            skLineSegment(sketch, "E839", {"start": v(193.8, 12.25) * mm, "end": v(193.95, 12.61) * mm});
            skLineSegment(sketch, "E840", {"start": v(193.95, 12.61) * mm, "end": v(194, 13) * mm});
            skLineSegment(sketch, "E841", {"start": v(194, 13) * mm, "end": v(193.95, 13.39) * mm});
            skLineSegment(sketch, "E842", {"start": v(193.95, 13.39) * mm, "end": v(193.8, 13.75) * mm});
            skLineSegment(sketch, "E843", {"start": v(193.8, 13.75) * mm, "end": v(193.56, 14.06) * mm});
            skLineSegment(sketch, "E844", {"start": v(193.56, 14.06) * mm, "end": v(193.25, 14.3) * mm});
            skLineSegment(sketch, "E845", {"start": v(193.25, 14.3) * mm, "end": v(192.89, 14.45) * mm});
            skLineSegment(sketch, "E846", {"start": v(192.89, 14.45) * mm, "end": v(192.5, 14.5) * mm});
            skLineSegment(sketch, "E847", {"start": v(192.5, 14.5) * mm, "end": v(192.11, 14.45) * mm});
            skLineSegment(sketch, "E848", {"start": v(191.05, -7.39) * mm, "end": v(191.2, -7.75) * mm});
            skLineSegment(sketch, "E849", {"start": v(191.2, -7.75) * mm, "end": v(191.44, -8.06) * mm});
            skLineSegment(sketch, "E850", {"start": v(191.44, -8.06) * mm, "end": v(191.75, -8.3) * mm});
            skLineSegment(sketch, "E851", {"start": v(191.75, -8.3) * mm, "end": v(192.11, -8.45) * mm});
            skLineSegment(sketch, "E852", {"start": v(192.11, -8.45) * mm, "end": v(192.5, -8.5) * mm});
            skLineSegment(sketch, "E853", {"start": v(192.5, -8.5) * mm, "end": v(192.89, -8.45) * mm});
            skLineSegment(sketch, "E854", {"start": v(192.89, -8.45) * mm, "end": v(193.25, -8.3) * mm});
            skLineSegment(sketch, "E855", {"start": v(193.25, -8.3) * mm, "end": v(193.56, -8.06) * mm});
            skLineSegment(sketch, "E856", {"start": v(193.56, -8.06) * mm, "end": v(193.8, -7.75) * mm});
            skLineSegment(sketch, "E857", {"start": v(193.8, -7.75) * mm, "end": v(193.95, -7.39) * mm});
            skLineSegment(sketch, "E858", {"start": v(193.95, -7.39) * mm, "end": v(194, -7) * mm});
            skLineSegment(sketch, "E859", {"start": v(194, -7) * mm, "end": v(193.95, -6.61) * mm});
            skLineSegment(sketch, "E860", {"start": v(193.95, -6.61) * mm, "end": v(193.8, -6.25) * mm});
            skLineSegment(sketch, "E861", {"start": v(193.8, -6.25) * mm, "end": v(193.56, -5.94) * mm});
            skLineSegment(sketch, "E862", {"start": v(193.56, -5.94) * mm, "end": v(193.25, -5.7) * mm});
            skLineSegment(sketch, "E863", {"start": v(193.25, -5.7) * mm, "end": v(192.89, -5.55) * mm});
            skLineSegment(sketch, "E864", {"start": v(192.89, -5.55) * mm, "end": v(192.5, -5.5) * mm});
            skLineSegment(sketch, "E865", {"start": v(192.5, -5.5) * mm, "end": v(192.11, -5.55) * mm});
            skLineSegment(sketch, "E866", {"start": v(192.11, -5.55) * mm, "end": v(191.75, -5.7) * mm});
            skLineSegment(sketch, "E867", {"start": v(191.75, -5.7) * mm, "end": v(191.44, -5.94) * mm});
            skLineSegment(sketch, "E868", {"start": v(191.44, -5.94) * mm, "end": v(191.2, -6.25) * mm});
            skLineSegment(sketch, "E869", {"start": v(191.2, -6.25) * mm, "end": v(191.05, -6.61) * mm});
            skLineSegment(sketch, "E870", {"start": v(191.05, -6.61) * mm, "end": v(191, -7) * mm});
            skLineSegment(sketch, "E871", {"start": v(191, -7) * mm, "end": v(191.05, -7.39) * mm});
            skLineSegment(sketch, "E872", {"start": v(191, -27) * mm, "end": v(191.05, -27.39) * mm});
            skLineSegment(sketch, "E873", {"start": v(191.05, -27.39) * mm, "end": v(191.2, -27.75) * mm});
            skLineSegment(sketch, "E874", {"start": v(191.2, -27.75) * mm, "end": v(191.44, -28.06) * mm});
            skLineSegment(sketch, "E875", {"start": v(191.44, -28.06) * mm, "end": v(191.75, -28.3) * mm});
            skLineSegment(sketch, "E876", {"start": v(191.75, -28.3) * mm, "end": v(192.11, -28.45) * mm});
            skLineSegment(sketch, "E877", {"start": v(192.11, -28.45) * mm, "end": v(192.5, -28.5) * mm});
            skLineSegment(sketch, "E878", {"start": v(192.5, -28.5) * mm, "end": v(192.89, -28.45) * mm});
            skLineSegment(sketch, "E879", {"start": v(192.89, -28.45) * mm, "end": v(193.25, -28.3) * mm});
            skLineSegment(sketch, "E880", {"start": v(193.25, -28.3) * mm, "end": v(193.56, -28.06) * mm});
            skLineSegment(sketch, "E881", {"start": v(193.56, -28.06) * mm, "end": v(193.8, -27.75) * mm});
            skLineSegment(sketch, "E882", {"start": v(193.8, -27.75) * mm, "end": v(193.95, -27.39) * mm});
            skLineSegment(sketch, "E883", {"start": v(193.95, -27.39) * mm, "end": v(194, -27) * mm});
            skLineSegment(sketch, "E884", {"start": v(194, -27) * mm, "end": v(193.95, -26.61) * mm});
            skLineSegment(sketch, "E885", {"start": v(193.95, -26.61) * mm, "end": v(193.8, -26.25) * mm});
            skLineSegment(sketch, "E886", {"start": v(193.8, -26.25) * mm, "end": v(193.56, -25.94) * mm});
            skLineSegment(sketch, "E887", {"start": v(193.56, -25.94) * mm, "end": v(193.25, -25.7) * mm});
            skLineSegment(sketch, "E888", {"start": v(193.25, -25.7) * mm, "end": v(192.89, -25.55) * mm});
            skLineSegment(sketch, "E889", {"start": v(192.89, -25.55) * mm, "end": v(192.5, -25.5) * mm});
            skLineSegment(sketch, "E890", {"start": v(192.5, -25.5) * mm, "end": v(192.11, -25.55) * mm});
            skLineSegment(sketch, "E891", {"start": v(192.11, -25.55) * mm, "end": v(191.75, -25.7) * mm});
            skLineSegment(sketch, "E892", {"start": v(191.75, -25.7) * mm, "end": v(191.44, -25.94) * mm});
            skLineSegment(sketch, "E893", {"start": v(191.44, -25.94) * mm, "end": v(191.2, -26.25) * mm});
            skLineSegment(sketch, "E894", {"start": v(191.2, -26.25) * mm, "end": v(191.05, -26.61) * mm});
            skLineSegment(sketch, "E895", {"start": v(191.05, -26.61) * mm, "end": v(191, -27) * mm});
            skLineSegment(sketch, "E896", {"start": v(-191.44, 11.94) * mm, "end": v(-191.2, 12.25) * mm});
            skLineSegment(sketch, "E897", {"start": v(-191.2, 12.25) * mm, "end": v(-191.05, 12.61) * mm});
            skLineSegment(sketch, "E898", {"start": v(-191.05, 12.61) * mm, "end": v(-191, 13) * mm});
            skLineSegment(sketch, "E899", {"start": v(-191, 13) * mm, "end": v(-191.05, 13.39) * mm});
            skLineSegment(sketch, "E900", {"start": v(-191.05, 13.39) * mm, "end": v(-191.2, 13.75) * mm});
            skLineSegment(sketch, "E901", {"start": v(-191.2, 13.75) * mm, "end": v(-191.44, 14.06) * mm});
            skLineSegment(sketch, "E902", {"start": v(-191.44, 14.06) * mm, "end": v(-191.75, 14.3) * mm});
            skLineSegment(sketch, "E903", {"start": v(-191.75, 14.3) * mm, "end": v(-192.11, 14.45) * mm});
            skLineSegment(sketch, "E904", {"start": v(-192.11, 14.45) * mm, "end": v(-192.5, 14.5) * mm});
            skLineSegment(sketch, "E905", {"start": v(-192.5, 14.5) * mm, "end": v(-192.89, 14.45) * mm});
            skLineSegment(sketch, "E906", {"start": v(-192.89, 14.45) * mm, "end": v(-193.25, 14.3) * mm});
            skLineSegment(sketch, "E907", {"start": v(-193.25, 14.3) * mm, "end": v(-193.56, 14.06) * mm});
            skLineSegment(sketch, "E908", {"start": v(-193.56, 14.06) * mm, "end": v(-193.8, 13.75) * mm});
            skLineSegment(sketch, "E909", {"start": v(-193.8, 13.75) * mm, "end": v(-193.95, 13.39) * mm});
            skLineSegment(sketch, "E910", {"start": v(-193.95, 13.39) * mm, "end": v(-194, 13) * mm});
            skLineSegment(sketch, "E911", {"start": v(-194, 13) * mm, "end": v(-193.95, 12.61) * mm});
            skLineSegment(sketch, "E912", {"start": v(-193.95, 12.61) * mm, "end": v(-193.8, 12.25) * mm});
            skLineSegment(sketch, "E913", {"start": v(-193.8, 12.25) * mm, "end": v(-193.56, 11.94) * mm});
            skLineSegment(sketch, "E914", {"start": v(-193.56, 11.94) * mm, "end": v(-193.25, 11.7) * mm});
            skLineSegment(sketch, "E915", {"start": v(-193.25, 11.7) * mm, "end": v(-192.89, 11.55) * mm});
            skLineSegment(sketch, "E916", {"start": v(-192.89, 11.55) * mm, "end": v(-192.5, 11.5) * mm});
            skLineSegment(sketch, "E917", {"start": v(-192.5, 11.5) * mm, "end": v(-192.11, 11.55) * mm});
            skLineSegment(sketch, "E918", {"start": v(-192.11, 11.55) * mm, "end": v(-191.75, 11.7) * mm});
            skLineSegment(sketch, "E919", {"start": v(-191.75, 11.7) * mm, "end": v(-191.44, 11.94) * mm});
            skLineSegment(sketch, "E920", {"start": v(-193.25, -5.7) * mm, "end": v(-193.56, -5.94) * mm});
            skLineSegment(sketch, "E921", {"start": v(-193.56, -5.94) * mm, "end": v(-193.8, -6.25) * mm});
            skLineSegment(sketch, "E922", {"start": v(-193.8, -6.25) * mm, "end": v(-193.95, -6.61) * mm});
            skLineSegment(sketch, "E923", {"start": v(-193.95, -6.61) * mm, "end": v(-194, -7) * mm});
            skLineSegment(sketch, "E924", {"start": v(-194, -7) * mm, "end": v(-193.95, -7.39) * mm});
            skLineSegment(sketch, "E925", {"start": v(-193.95, -7.39) * mm, "end": v(-193.8, -7.75) * mm});
            skLineSegment(sketch, "E926", {"start": v(-193.8, -7.75) * mm, "end": v(-193.56, -8.06) * mm});
            skLineSegment(sketch, "E927", {"start": v(-193.56, -8.06) * mm, "end": v(-193.25, -8.3) * mm});
            skLineSegment(sketch, "E928", {"start": v(-193.25, -8.3) * mm, "end": v(-192.89, -8.45) * mm});
            skLineSegment(sketch, "E929", {"start": v(-192.89, -8.45) * mm, "end": v(-192.5, -8.5) * mm});
            skLineSegment(sketch, "E930", {"start": v(-192.5, -8.5) * mm, "end": v(-192.11, -8.45) * mm});
            skLineSegment(sketch, "E931", {"start": v(-192.11, -8.45) * mm, "end": v(-191.75, -8.3) * mm});
            skLineSegment(sketch, "E932", {"start": v(-191.75, -8.3) * mm, "end": v(-191.44, -8.06) * mm});
            skLineSegment(sketch, "E933", {"start": v(-191.44, -8.06) * mm, "end": v(-191.2, -7.75) * mm});
            skLineSegment(sketch, "E934", {"start": v(-191.2, -7.75) * mm, "end": v(-191.05, -7.39) * mm});
            skLineSegment(sketch, "E935", {"start": v(-191.05, -7.39) * mm, "end": v(-191, -7) * mm});
            skLineSegment(sketch, "E936", {"start": v(-191, -7) * mm, "end": v(-191.05, -6.61) * mm});
            skLineSegment(sketch, "E937", {"start": v(-191.05, -6.61) * mm, "end": v(-191.2, -6.25) * mm});
            skLineSegment(sketch, "E938", {"start": v(-191.2, -6.25) * mm, "end": v(-191.44, -5.94) * mm});
            skLineSegment(sketch, "E939", {"start": v(-191.44, -5.94) * mm, "end": v(-191.75, -5.7) * mm});
            skLineSegment(sketch, "E940", {"start": v(-191.75, -5.7) * mm, "end": v(-192.11, -5.55) * mm});
            skLineSegment(sketch, "E941", {"start": v(-192.11, -5.55) * mm, "end": v(-192.5, -5.5) * mm});
            skLineSegment(sketch, "E942", {"start": v(-192.5, -5.5) * mm, "end": v(-192.89, -5.55) * mm});
            skLineSegment(sketch, "E943", {"start": v(-192.89, -5.55) * mm, "end": v(-193.25, -5.7) * mm});
            skLineSegment(sketch, "E944", {"start": v(-193.56, -25.94) * mm, "end": v(-193.8, -26.25) * mm});
            skLineSegment(sketch, "E945", {"start": v(-193.8, -26.25) * mm, "end": v(-193.95, -26.61) * mm});
            skLineSegment(sketch, "E946", {"start": v(-193.95, -26.61) * mm, "end": v(-194, -27) * mm});
            skLineSegment(sketch, "E947", {"start": v(-194, -27) * mm, "end": v(-193.95, -27.39) * mm});
            skLineSegment(sketch, "E948", {"start": v(-193.95, -27.39) * mm, "end": v(-193.8, -27.75) * mm});
            skLineSegment(sketch, "E949", {"start": v(-193.8, -27.75) * mm, "end": v(-193.56, -28.06) * mm});
            skLineSegment(sketch, "E950", {"start": v(-193.56, -28.06) * mm, "end": v(-193.25, -28.3) * mm});
            skLineSegment(sketch, "E951", {"start": v(-193.25, -28.3) * mm, "end": v(-192.89, -28.45) * mm});
            skLineSegment(sketch, "E952", {"start": v(-192.89, -28.45) * mm, "end": v(-192.5, -28.5) * mm});
            skLineSegment(sketch, "E953", {"start": v(-192.5, -28.5) * mm, "end": v(-192.11, -28.45) * mm});
            skLineSegment(sketch, "E954", {"start": v(-192.11, -28.45) * mm, "end": v(-191.75, -28.3) * mm});
            skLineSegment(sketch, "E955", {"start": v(-191.75, -28.3) * mm, "end": v(-191.44, -28.06) * mm});
            skLineSegment(sketch, "E956", {"start": v(-191.44, -28.06) * mm, "end": v(-191.2, -27.75) * mm});
            skLineSegment(sketch, "E957", {"start": v(-191.2, -27.75) * mm, "end": v(-191.05, -27.39) * mm});
            skLineSegment(sketch, "E958", {"start": v(-191.05, -27.39) * mm, "end": v(-191, -27) * mm});
            skLineSegment(sketch, "E959", {"start": v(-191, -27) * mm, "end": v(-191.05, -26.61) * mm});
            skLineSegment(sketch, "E960", {"start": v(-191.05, -26.61) * mm, "end": v(-191.2, -26.25) * mm});
            skLineSegment(sketch, "E961", {"start": v(-191.2, -26.25) * mm, "end": v(-191.44, -25.94) * mm});
            skLineSegment(sketch, "E962", {"start": v(-191.44, -25.94) * mm, "end": v(-191.75, -25.7) * mm});
            skLineSegment(sketch, "E963", {"start": v(-191.75, -25.7) * mm, "end": v(-192.11, -25.55) * mm});
            skLineSegment(sketch, "E964", {"start": v(-192.11, -25.55) * mm, "end": v(-192.5, -25.5) * mm});
            skLineSegment(sketch, "E965", {"start": v(-192.5, -25.5) * mm, "end": v(-192.89, -25.55) * mm});
            skLineSegment(sketch, "E966", {"start": v(-192.89, -25.55) * mm, "end": v(-193.25, -25.7) * mm});
            skLineSegment(sketch, "E967", {"start": v(-193.25, -25.7) * mm, "end": v(-193.56, -25.94) * mm});
            skLineSegment(sketch, "E968", {"start": v(101.5, 8) * mm, "end": v(101.45, 8.39) * mm});
            skLineSegment(sketch, "E969", {"start": v(101.45, 8.39) * mm, "end": v(101.3, 8.75) * mm});
            skLineSegment(sketch, "E970", {"start": v(101.3, 8.75) * mm, "end": v(101.06, 9.06) * mm});
            skLineSegment(sketch, "E971", {"start": v(101.06, 9.06) * mm, "end": v(100.75, 9.3) * mm});
            skLineSegment(sketch, "E972", {"start": v(100.75, 9.3) * mm, "end": v(100.39, 9.45) * mm});
            skLineSegment(sketch, "E973", {"start": v(100.39, 9.45) * mm, "end": v(100, 9.5) * mm});
            skLineSegment(sketch, "E974", {"start": v(100, 9.5) * mm, "end": v(99.61, 9.45) * mm});
            skLineSegment(sketch, "E975", {"start": v(99.61, 9.45) * mm, "end": v(99.25, 9.3) * mm});
            skLineSegment(sketch, "E976", {"start": v(99.25, 9.3) * mm, "end": v(98.94, 9.06) * mm});
            skLineSegment(sketch, "E977", {"start": v(98.94, 9.06) * mm, "end": v(98.7, 8.75) * mm});
            skLineSegment(sketch, "E978", {"start": v(98.7, 8.75) * mm, "end": v(98.55, 8.39) * mm});
            skLineSegment(sketch, "E979", {"start": v(98.55, 8.39) * mm, "end": v(98.5, 8) * mm});
            skLineSegment(sketch, "E980", {"start": v(98.5, 8) * mm, "end": v(98.55, 7.61) * mm});
            skLineSegment(sketch, "E981", {"start": v(98.55, 7.61) * mm, "end": v(98.7, 7.25) * mm});
            skLineSegment(sketch, "E982", {"start": v(98.7, 7.25) * mm, "end": v(98.94, 6.94) * mm});
            skLineSegment(sketch, "E983", {"start": v(98.94, 6.94) * mm, "end": v(99.25, 6.7) * mm});
            skLineSegment(sketch, "E984", {"start": v(99.25, 6.7) * mm, "end": v(99.61, 6.55) * mm});
            skLineSegment(sketch, "E985", {"start": v(99.61, 6.55) * mm, "end": v(100, 6.5) * mm});
            skLineSegment(sketch, "E986", {"start": v(100, 6.5) * mm, "end": v(100.39, 6.55) * mm});
            skLineSegment(sketch, "E987", {"start": v(100.39, 6.55) * mm, "end": v(100.75, 6.7) * mm});
            skLineSegment(sketch, "E988", {"start": v(100.75, 6.7) * mm, "end": v(101.06, 6.94) * mm});
            skLineSegment(sketch, "E989", {"start": v(101.06, 6.94) * mm, "end": v(101.3, 7.25) * mm});
            skLineSegment(sketch, "E990", {"start": v(101.3, 7.25) * mm, "end": v(101.45, 7.61) * mm});
            skLineSegment(sketch, "E991", {"start": v(101.45, 7.61) * mm, "end": v(101.5, 8) * mm});
            skLineSegment(sketch, "E992", {"start": v(70.39, 6.55) * mm, "end": v(70.75, 6.7) * mm});
            skLineSegment(sketch, "E993", {"start": v(70.75, 6.7) * mm, "end": v(71.06, 6.94) * mm});
            skLineSegment(sketch, "E994", {"start": v(71.06, 6.94) * mm, "end": v(71.3, 7.25) * mm});
            skLineSegment(sketch, "E995", {"start": v(71.3, 7.25) * mm, "end": v(71.45, 7.61) * mm});
            skLineSegment(sketch, "E996", {"start": v(71.45, 7.61) * mm, "end": v(71.5, 8) * mm});
            skLineSegment(sketch, "E997", {"start": v(71.5, 8) * mm, "end": v(71.45, 8.39) * mm});
            skLineSegment(sketch, "E998", {"start": v(71.45, 8.39) * mm, "end": v(71.3, 8.75) * mm});
            skLineSegment(sketch, "E999", {"start": v(71.3, 8.75) * mm, "end": v(71.06, 9.06) * mm});
            skLineSegment(sketch, "E1000", {"start": v(71.06, 9.06) * mm, "end": v(70.75, 9.3) * mm});
            skLineSegment(sketch, "E1001", {"start": v(70.75, 9.3) * mm, "end": v(70.39, 9.45) * mm});
            skLineSegment(sketch, "E1002", {"start": v(70.39, 9.45) * mm, "end": v(70, 9.5) * mm});
            skLineSegment(sketch, "E1003", {"start": v(70, 9.5) * mm, "end": v(69.61, 9.45) * mm});
            skLineSegment(sketch, "E1004", {"start": v(69.61, 9.45) * mm, "end": v(69.25, 9.3) * mm});
            skLineSegment(sketch, "E1005", {"start": v(69.25, 9.3) * mm, "end": v(68.94, 9.06) * mm});
            skLineSegment(sketch, "E1006", {"start": v(68.94, 9.06) * mm, "end": v(68.7, 8.75) * mm});
            skLineSegment(sketch, "E1007", {"start": v(68.7, 8.75) * mm, "end": v(68.55, 8.39) * mm});
            skLineSegment(sketch, "E1008", {"start": v(68.55, 8.39) * mm, "end": v(68.5, 8) * mm});
            skLineSegment(sketch, "E1009", {"start": v(68.5, 8) * mm, "end": v(68.55, 7.61) * mm});
            skLineSegment(sketch, "E1010", {"start": v(68.55, 7.61) * mm, "end": v(68.7, 7.25) * mm});
            skLineSegment(sketch, "E1011", {"start": v(68.7, 7.25) * mm, "end": v(68.94, 6.94) * mm});
            skLineSegment(sketch, "E1012", {"start": v(68.94, 6.94) * mm, "end": v(69.25, 6.7) * mm});
            skLineSegment(sketch, "E1013", {"start": v(69.25, 6.7) * mm, "end": v(69.61, 6.55) * mm});
            skLineSegment(sketch, "E1014", {"start": v(69.61, 6.55) * mm, "end": v(70, 6.5) * mm});
            skLineSegment(sketch, "E1015", {"start": v(70, 6.5) * mm, "end": v(70.39, 6.55) * mm});
            skLineSegment(sketch, "E1016", {"start": v(-71.5, 8) * mm, "end": v(-71.45, 7.61) * mm});
            skLineSegment(sketch, "E1017", {"start": v(-71.45, 7.61) * mm, "end": v(-71.3, 7.25) * mm});
            skLineSegment(sketch, "E1018", {"start": v(-71.3, 7.25) * mm, "end": v(-71.06, 6.94) * mm});
            skLineSegment(sketch, "E1019", {"start": v(-71.06, 6.94) * mm, "end": v(-70.75, 6.7) * mm});
            skLineSegment(sketch, "E1020", {"start": v(-70.75, 6.7) * mm, "end": v(-70.39, 6.55) * mm});
            skLineSegment(sketch, "E1021", {"start": v(-70.39, 6.55) * mm, "end": v(-70, 6.5) * mm});
            skLineSegment(sketch, "E1022", {"start": v(-70, 6.5) * mm, "end": v(-69.61, 6.55) * mm});
            skLineSegment(sketch, "E1023", {"start": v(-69.61, 6.55) * mm, "end": v(-69.25, 6.7) * mm});
            skLineSegment(sketch, "E1024", {"start": v(-69.25, 6.7) * mm, "end": v(-68.94, 6.94) * mm});
            skLineSegment(sketch, "E1025", {"start": v(-68.94, 6.94) * mm, "end": v(-68.7, 7.25) * mm});
            skLineSegment(sketch, "E1026", {"start": v(-68.7, 7.25) * mm, "end": v(-68.55, 7.61) * mm});
            skLineSegment(sketch, "E1027", {"start": v(-68.55, 7.61) * mm, "end": v(-68.5, 8) * mm});
            skLineSegment(sketch, "E1028", {"start": v(-68.5, 8) * mm, "end": v(-68.55, 8.39) * mm});
            skLineSegment(sketch, "E1029", {"start": v(-68.55, 8.39) * mm, "end": v(-68.7, 8.75) * mm});
            skLineSegment(sketch, "E1030", {"start": v(-68.7, 8.75) * mm, "end": v(-68.94, 9.06) * mm});
            skLineSegment(sketch, "E1031", {"start": v(-68.94, 9.06) * mm, "end": v(-69.25, 9.3) * mm});
            skLineSegment(sketch, "E1032", {"start": v(-69.25, 9.3) * mm, "end": v(-69.61, 9.45) * mm});
            skLineSegment(sketch, "E1033", {"start": v(-69.61, 9.45) * mm, "end": v(-70, 9.5) * mm});
            skLineSegment(sketch, "E1034", {"start": v(-70, 9.5) * mm, "end": v(-70.39, 9.45) * mm});
            skLineSegment(sketch, "E1035", {"start": v(-70.39, 9.45) * mm, "end": v(-70.75, 9.3) * mm});
            skLineSegment(sketch, "E1036", {"start": v(-70.75, 9.3) * mm, "end": v(-71.06, 9.06) * mm});
            skLineSegment(sketch, "E1037", {"start": v(-71.06, 9.06) * mm, "end": v(-71.3, 8.75) * mm});
            skLineSegment(sketch, "E1038", {"start": v(-71.3, 8.75) * mm, "end": v(-71.45, 8.39) * mm});
            skLineSegment(sketch, "E1039", {"start": v(-71.45, 8.39) * mm, "end": v(-71.5, 8) * mm});
            skLineSegment(sketch, "E1040", {"start": v(-101.3, 8.75) * mm, "end": v(-101.45, 8.39) * mm});
            skLineSegment(sketch, "E1041", {"start": v(-101.45, 8.39) * mm, "end": v(-101.5, 8) * mm});
            skLineSegment(sketch, "E1042", {"start": v(-101.5, 8) * mm, "end": v(-101.45, 7.61) * mm});
            skLineSegment(sketch, "E1043", {"start": v(-101.45, 7.61) * mm, "end": v(-101.3, 7.25) * mm});
            skLineSegment(sketch, "E1044", {"start": v(-101.3, 7.25) * mm, "end": v(-101.06, 6.94) * mm});
            skLineSegment(sketch, "E1045", {"start": v(-101.06, 6.94) * mm, "end": v(-100.75, 6.7) * mm});
            skLineSegment(sketch, "E1046", {"start": v(-100.75, 6.7) * mm, "end": v(-100.39, 6.55) * mm});
            skLineSegment(sketch, "E1047", {"start": v(-100.39, 6.55) * mm, "end": v(-100, 6.5) * mm});
            skLineSegment(sketch, "E1048", {"start": v(-100, 6.5) * mm, "end": v(-99.61, 6.55) * mm});
            skLineSegment(sketch, "E1049", {"start": v(-99.61, 6.55) * mm, "end": v(-99.25, 6.7) * mm});
            skLineSegment(sketch, "E1050", {"start": v(-99.25, 6.7) * mm, "end": v(-98.94, 6.94) * mm});
            skLineSegment(sketch, "E1051", {"start": v(-98.94, 6.94) * mm, "end": v(-98.7, 7.25) * mm});
            skLineSegment(sketch, "E1052", {"start": v(-98.7, 7.25) * mm, "end": v(-98.55, 7.61) * mm});
            skLineSegment(sketch, "E1053", {"start": v(-98.55, 7.61) * mm, "end": v(-98.5, 8) * mm});
            skLineSegment(sketch, "E1054", {"start": v(-98.5, 8) * mm, "end": v(-98.55, 8.39) * mm});
            skLineSegment(sketch, "E1055", {"start": v(-98.55, 8.39) * mm, "end": v(-98.7, 8.75) * mm});
            skLineSegment(sketch, "E1056", {"start": v(-98.7, 8.75) * mm, "end": v(-98.94, 9.06) * mm});
            skLineSegment(sketch, "E1057", {"start": v(-98.94, 9.06) * mm, "end": v(-99.25, 9.3) * mm});
            skLineSegment(sketch, "E1058", {"start": v(-99.25, 9.3) * mm, "end": v(-99.61, 9.45) * mm});
            skLineSegment(sketch, "E1059", {"start": v(-99.61, 9.45) * mm, "end": v(-100, 9.5) * mm});
            skLineSegment(sketch, "E1060", {"start": v(-100, 9.5) * mm, "end": v(-100.39, 9.45) * mm});
            skLineSegment(sketch, "E1061", {"start": v(-100.39, 9.45) * mm, "end": v(-100.75, 9.3) * mm});
            skLineSegment(sketch, "E1062", {"start": v(-100.75, 9.3) * mm, "end": v(-101.06, 9.06) * mm});
            skLineSegment(sketch, "E1063", {"start": v(-101.06, 9.06) * mm, "end": v(-101.3, 8.75) * mm});
            skLineSegment(sketch, "E1064", {"start": v(81, 8) * mm, "end": v(81.14, 6.96) * mm});
            skLineSegment(sketch, "E1065", {"start": v(81.14, 6.96) * mm, "end": v(81.54, 6) * mm});
            skLineSegment(sketch, "E1066", {"start": v(81.54, 6) * mm, "end": v(82.17, 5.17) * mm});
            skLineSegment(sketch, "E1067", {"start": v(82.17, 5.17) * mm, "end": v(83, 4.54) * mm});
            skLineSegment(sketch, "E1068", {"start": v(83, 4.54) * mm, "end": v(83.96, 4.14) * mm});
            skLineSegment(sketch, "E1069", {"start": v(83.96, 4.14) * mm, "end": v(85, 4) * mm});
            skLineSegment(sketch, "E1070", {"start": v(85, 4) * mm, "end": v(86.04, 4.14) * mm});
            skLineSegment(sketch, "E1071", {"start": v(86.04, 4.14) * mm, "end": v(87, 4.54) * mm});
            skLineSegment(sketch, "E1072", {"start": v(87, 4.54) * mm, "end": v(87.83, 5.17) * mm});
            skLineSegment(sketch, "E1073", {"start": v(87.83, 5.17) * mm, "end": v(88.46, 6) * mm});
            skLineSegment(sketch, "E1074", {"start": v(88.46, 6) * mm, "end": v(88.86, 6.96) * mm});
            skLineSegment(sketch, "E1075", {"start": v(88.86, 6.96) * mm, "end": v(89, 8) * mm});
            skLineSegment(sketch, "E1076", {"start": v(89, 8) * mm, "end": v(88.86, 9.04) * mm});
            skLineSegment(sketch, "E1077", {"start": v(88.86, 9.04) * mm, "end": v(88.46, 10) * mm});
            skLineSegment(sketch, "E1078", {"start": v(88.46, 10) * mm, "end": v(87.83, 10.83) * mm});
            skLineSegment(sketch, "E1079", {"start": v(87.83, 10.83) * mm, "end": v(87, 11.46) * mm});
            skLineSegment(sketch, "E1080", {"start": v(87, 11.46) * mm, "end": v(86.04, 11.86) * mm});
            skLineSegment(sketch, "E1081", {"start": v(86.04, 11.86) * mm, "end": v(85, 12) * mm});
            skLineSegment(sketch, "E1082", {"start": v(85, 12) * mm, "end": v(83.96, 11.86) * mm});
            skLineSegment(sketch, "E1083", {"start": v(83.96, 11.86) * mm, "end": v(83, 11.46) * mm});
            skLineSegment(sketch, "E1084", {"start": v(83, 11.46) * mm, "end": v(82.17, 10.83) * mm});
            skLineSegment(sketch, "E1085", {"start": v(82.17, 10.83) * mm, "end": v(81.54, 10) * mm});
            skLineSegment(sketch, "E1086", {"start": v(81.54, 10) * mm, "end": v(81.14, 9.04) * mm});
            skLineSegment(sketch, "E1087", {"start": v(81.14, 9.04) * mm, "end": v(81, 8) * mm});
            skLineSegment(sketch, "E1088", {"start": v(-87.83, 10.83) * mm, "end": v(-88.46, 10) * mm});
            skLineSegment(sketch, "E1089", {"start": v(-88.46, 10) * mm, "end": v(-88.86, 9.04) * mm});
            skLineSegment(sketch, "E1090", {"start": v(-88.86, 9.04) * mm, "end": v(-89, 8) * mm});
            skLineSegment(sketch, "E1091", {"start": v(-89, 8) * mm, "end": v(-88.86, 6.96) * mm});
            skLineSegment(sketch, "E1092", {"start": v(-88.86, 6.96) * mm, "end": v(-88.46, 6) * mm});
            skLineSegment(sketch, "E1093", {"start": v(-88.46, 6) * mm, "end": v(-87.83, 5.17) * mm});
            skLineSegment(sketch, "E1094", {"start": v(-87.83, 5.17) * mm, "end": v(-87, 4.54) * mm});
            skLineSegment(sketch, "E1095", {"start": v(-87, 4.54) * mm, "end": v(-86.04, 4.14) * mm});
            skLineSegment(sketch, "E1096", {"start": v(-86.04, 4.14) * mm, "end": v(-85, 4) * mm});
            skLineSegment(sketch, "E1097", {"start": v(-85, 4) * mm, "end": v(-83.96, 4.14) * mm});
            skLineSegment(sketch, "E1098", {"start": v(-83.96, 4.14) * mm, "end": v(-83, 4.54) * mm});
            skLineSegment(sketch, "E1099", {"start": v(-83, 4.54) * mm, "end": v(-82.17, 5.17) * mm});
            skLineSegment(sketch, "E1100", {"start": v(-82.17, 5.17) * mm, "end": v(-81.54, 6) * mm});
            skLineSegment(sketch, "E1101", {"start": v(-81.54, 6) * mm, "end": v(-81.14, 6.96) * mm});
            skLineSegment(sketch, "E1102", {"start": v(-81.14, 6.96) * mm, "end": v(-81, 8) * mm});
            skLineSegment(sketch, "E1103", {"start": v(-81, 8) * mm, "end": v(-81.14, 9.04) * mm});
            skLineSegment(sketch, "E1104", {"start": v(-81.14, 9.04) * mm, "end": v(-81.54, 10) * mm});
            skLineSegment(sketch, "E1105", {"start": v(-81.54, 10) * mm, "end": v(-82.17, 10.83) * mm});
            skLineSegment(sketch, "E1106", {"start": v(-82.17, 10.83) * mm, "end": v(-83, 11.46) * mm});
            skLineSegment(sketch, "E1107", {"start": v(-83, 11.46) * mm, "end": v(-83.96, 11.86) * mm});
            skLineSegment(sketch, "E1108", {"start": v(-83.96, 11.86) * mm, "end": v(-85, 12) * mm});
            skLineSegment(sketch, "E1109", {"start": v(-85, 12) * mm, "end": v(-86.04, 11.86) * mm});
            skLineSegment(sketch, "E1110", {"start": v(-86.04, 11.86) * mm, "end": v(-87, 11.46) * mm});
            skLineSegment(sketch, "E1111", {"start": v(-87, 11.46) * mm, "end": v(-87.83, 10.83) * mm});
            skSolve(sketch);
        }
        {
            var Q0;
            Q0=makeQuery(id+"F4.imprint","IMPRINT",FACE,{"disambiguationData":[TD([[makeQuery(id+"F4.imprint","IMPRINT",EDGE,{"derivedFrom":sQuery(id+"F4.wireOp",EDGE,"E576")}),-1.0]])]});
            var Q1;
            Q1=makeQuery(id+"F0.imprint","IMPRINT",FACE,{"disambiguationData":[TD([[makeQuery(id+"F0.imprint","IMPRINT",EDGE,{"derivedFrom":sQuery(id+"F0.wireOp",EDGE,"E0")}),-1.0]])]});
            extrude(context, id + "F5", {"entities" : qUnion([Q0, Q1]), "depth" : 15 * mm});
        }
        {
            var Q0;
            Q0=makeQuery(id+"F0.imprint","IMPRINT",FACE,{"disambiguationData":[TD([[makeQuery(id+"F0.imprint","IMPRINT",EDGE,{"derivedFrom":sQuery(id+"F0.wireOp",EDGE,"E0")}),-1.0]])]});
            extrude(context, id + "F6", {"entities" : qUnion([Q0]), "operationType" : NewBodyOperationType.ADD, "depth" : 15 * mm});
        }
        {
            var Q0;
            Q0=makeQuery(id+"F2.imprint","IMPRINT",FACE,{"disambiguationData":[TD([[makeQuery(id+"F2.imprint","IMPRINT",EDGE,{"derivedFrom":sQuery(id+"F2.wireOp",EDGE,"E419")}),-1.0]])]});
            extrude(context, id + "F7", {"entities" : qUnion([Q0]), "depth" : 15 * mm});
        }
        {
            var Q0;
            Q0=qCreatedBy(id+"F3.planeOp",FACE);
            cPlane(context, id + "F8", {"entities" : qUnion([Q0]), "cplaneType" : CPlaneType.OFFSET, "offset" : 200 * mm, "oppositeDirection" : true, "width" : 150 * mm, "height" : 150 * mm});
        }
        {
            var Q0;
            Q0=qCreatedBy(id+"F8.planeOp",FACE);
            var sketch = newSketch(context, id + "F9", { "sketchPlane" : qUnion([Q0])});
            skLineSegment(sketch, "E1112", {"start": v(215, 50) * mm, "end": v(215, -50) * mm});
            skLineSegment(sketch, "E1113", {"start": v(215, -50) * mm, "end": v(-215, -50) * mm});
            skLineSegment(sketch, "E1114", {"start": v(-215, -50) * mm, "end": v(-215, 50) * mm});
            skLineSegment(sketch, "E1115", {"start": v(-215, 50) * mm, "end": v(215, 50) * mm});
            skLineSegment(sketch, "E1116", {"start": v(208.25, 28.7) * mm, "end": v(208.56, 28.94) * mm});
            skLineSegment(sketch, "E1117", {"start": v(208.56, 28.94) * mm, "end": v(208.8, 29.25) * mm});
            skLineSegment(sketch, "E1118", {"start": v(208.8, 29.25) * mm, "end": v(208.95, 29.61) * mm});
            skLineSegment(sketch, "E1119", {"start": v(208.95, 29.61) * mm, "end": v(209, 30) * mm});
            skLineSegment(sketch, "E1120", {"start": v(209, 30) * mm, "end": v(208.95, 30.39) * mm});
            skLineSegment(sketch, "E1121", {"start": v(208.95, 30.39) * mm, "end": v(208.8, 30.75) * mm});
            skLineSegment(sketch, "E1122", {"start": v(208.8, 30.75) * mm, "end": v(208.56, 31.06) * mm});
            skLineSegment(sketch, "E1123", {"start": v(208.56, 31.06) * mm, "end": v(208.25, 31.3) * mm});
            skLineSegment(sketch, "E1124", {"start": v(208.25, 31.3) * mm, "end": v(207.89, 31.45) * mm});
            skLineSegment(sketch, "E1125", {"start": v(207.89, 31.45) * mm, "end": v(207.5, 31.5) * mm});
            skLineSegment(sketch, "E1126", {"start": v(207.5, 31.5) * mm, "end": v(207.11, 31.45) * mm});
            skLineSegment(sketch, "E1127", {"start": v(207.11, 31.45) * mm, "end": v(206.75, 31.3) * mm});
            skLineSegment(sketch, "E1128", {"start": v(206.75, 31.3) * mm, "end": v(206.44, 31.06) * mm});
            skLineSegment(sketch, "E1129", {"start": v(206.44, 31.06) * mm, "end": v(206.2, 30.75) * mm});
            skLineSegment(sketch, "E1130", {"start": v(206.2, 30.75) * mm, "end": v(206.05, 30.39) * mm});
            skLineSegment(sketch, "E1131", {"start": v(206.05, 30.39) * mm, "end": v(206, 30) * mm});
            skLineSegment(sketch, "E1132", {"start": v(206, 30) * mm, "end": v(206.05, 29.61) * mm});
            skLineSegment(sketch, "E1133", {"start": v(206.05, 29.61) * mm, "end": v(206.2, 29.25) * mm});
            skLineSegment(sketch, "E1134", {"start": v(206.2, 29.25) * mm, "end": v(206.44, 28.94) * mm});
            skLineSegment(sketch, "E1135", {"start": v(206.44, 28.94) * mm, "end": v(206.75, 28.7) * mm});
            skLineSegment(sketch, "E1136", {"start": v(206.75, 28.7) * mm, "end": v(207.11, 28.55) * mm});
            skLineSegment(sketch, "E1137", {"start": v(207.11, 28.55) * mm, "end": v(207.5, 28.5) * mm});
            skLineSegment(sketch, "E1138", {"start": v(207.5, 28.5) * mm, "end": v(207.89, 28.55) * mm});
            skLineSegment(sketch, "E1139", {"start": v(207.89, 28.55) * mm, "end": v(208.25, 28.7) * mm});
            skLineSegment(sketch, "E1140", {"start": v(207.89, 1.45) * mm, "end": v(207.5, 1.5) * mm});
            skLineSegment(sketch, "E1141", {"start": v(207.5, 1.5) * mm, "end": v(207.11, 1.45) * mm});
            skLineSegment(sketch, "E1142", {"start": v(207.11, 1.45) * mm, "end": v(206.75, 1.3) * mm});
            skLineSegment(sketch, "E1143", {"start": v(206.75, 1.3) * mm, "end": v(206.44, 1.06) * mm});
            skLineSegment(sketch, "E1144", {"start": v(206.44, 1.06) * mm, "end": v(206.2, 0.75) * mm});
            skLineSegment(sketch, "E1145", {"start": v(206.2, 0.75) * mm, "end": v(206.05, 0.39) * mm});
            skLineSegment(sketch, "E1146", {"start": v(206.05, 0.39) * mm, "end": v(206, 0) * mm});
            skLineSegment(sketch, "E1147", {"start": v(206, 0) * mm, "end": v(206.05, -0.39) * mm});
            skLineSegment(sketch, "E1148", {"start": v(206.05, -0.39) * mm, "end": v(206.2, -0.75) * mm});
            skLineSegment(sketch, "E1149", {"start": v(206.2, -0.75) * mm, "end": v(206.44, -1.06) * mm});
            skLineSegment(sketch, "E1150", {"start": v(206.44, -1.06) * mm, "end": v(206.75, -1.3) * mm});
            skLineSegment(sketch, "E1151", {"start": v(206.75, -1.3) * mm, "end": v(207.11, -1.45) * mm});
            skLineSegment(sketch, "E1152", {"start": v(207.11, -1.45) * mm, "end": v(207.5, -1.5) * mm});
            skLineSegment(sketch, "E1153", {"start": v(207.5, -1.5) * mm, "end": v(207.89, -1.45) * mm});
            skLineSegment(sketch, "E1154", {"start": v(207.89, -1.45) * mm, "end": v(208.25, -1.3) * mm});
            skLineSegment(sketch, "E1155", {"start": v(208.25, -1.3) * mm, "end": v(208.56, -1.06) * mm});
            skLineSegment(sketch, "E1156", {"start": v(208.56, -1.06) * mm, "end": v(208.8, -0.75) * mm});
            skLineSegment(sketch, "E1157", {"start": v(208.8, -0.75) * mm, "end": v(208.95, -0.39) * mm});
            skLineSegment(sketch, "E1158", {"start": v(208.95, -0.39) * mm, "end": v(209, 0) * mm});
            skLineSegment(sketch, "E1159", {"start": v(209, 0) * mm, "end": v(208.95, 0.39) * mm});
            skLineSegment(sketch, "E1160", {"start": v(208.95, 0.39) * mm, "end": v(208.8, 0.75) * mm});
            skLineSegment(sketch, "E1161", {"start": v(208.8, 0.75) * mm, "end": v(208.56, 1.06) * mm});
            skLineSegment(sketch, "E1162", {"start": v(208.56, 1.06) * mm, "end": v(208.25, 1.3) * mm});
            skLineSegment(sketch, "E1163", {"start": v(208.25, 1.3) * mm, "end": v(207.89, 1.45) * mm});
            skLineSegment(sketch, "E1164", {"start": v(207.11, -28.55) * mm, "end": v(206.75, -28.7) * mm});
            skLineSegment(sketch, "E1165", {"start": v(206.75, -28.7) * mm, "end": v(206.44, -28.94) * mm});
            skLineSegment(sketch, "E1166", {"start": v(206.44, -28.94) * mm, "end": v(206.2, -29.25) * mm});
            skLineSegment(sketch, "E1167", {"start": v(206.2, -29.25) * mm, "end": v(206.05, -29.61) * mm});
            skLineSegment(sketch, "E1168", {"start": v(206.05, -29.61) * mm, "end": v(206, -30) * mm});
            skLineSegment(sketch, "E1169", {"start": v(206, -30) * mm, "end": v(206.05, -30.39) * mm});
            skLineSegment(sketch, "E1170", {"start": v(206.05, -30.39) * mm, "end": v(206.2, -30.75) * mm});
            skLineSegment(sketch, "E1171", {"start": v(206.2, -30.75) * mm, "end": v(206.44, -31.06) * mm});
            skLineSegment(sketch, "E1172", {"start": v(206.44, -31.06) * mm, "end": v(206.75, -31.3) * mm});
            skLineSegment(sketch, "E1173", {"start": v(206.75, -31.3) * mm, "end": v(207.11, -31.45) * mm});
            skLineSegment(sketch, "E1174", {"start": v(207.11, -31.45) * mm, "end": v(207.5, -31.5) * mm});
            skLineSegment(sketch, "E1175", {"start": v(207.5, -31.5) * mm, "end": v(207.89, -31.45) * mm});
            skLineSegment(sketch, "E1176", {"start": v(207.89, -31.45) * mm, "end": v(208.25, -31.3) * mm});
            skLineSegment(sketch, "E1177", {"start": v(208.25, -31.3) * mm, "end": v(208.56, -31.06) * mm});
            skLineSegment(sketch, "E1178", {"start": v(208.56, -31.06) * mm, "end": v(208.8, -30.75) * mm});
            skLineSegment(sketch, "E1179", {"start": v(208.8, -30.75) * mm, "end": v(208.95, -30.39) * mm});
            skLineSegment(sketch, "E1180", {"start": v(208.95, -30.39) * mm, "end": v(209, -30) * mm});
            skLineSegment(sketch, "E1181", {"start": v(209, -30) * mm, "end": v(208.95, -29.61) * mm});
            skLineSegment(sketch, "E1182", {"start": v(208.95, -29.61) * mm, "end": v(208.8, -29.25) * mm});
            skLineSegment(sketch, "E1183", {"start": v(208.8, -29.25) * mm, "end": v(208.56, -28.94) * mm});
            skLineSegment(sketch, "E1184", {"start": v(208.56, -28.94) * mm, "end": v(208.25, -28.7) * mm});
            skLineSegment(sketch, "E1185", {"start": v(208.25, -28.7) * mm, "end": v(207.89, -28.55) * mm});
            skLineSegment(sketch, "E1186", {"start": v(207.89, -28.55) * mm, "end": v(207.5, -28.5) * mm});
            skLineSegment(sketch, "E1187", {"start": v(207.5, -28.5) * mm, "end": v(207.11, -28.55) * mm});
            skLineSegment(sketch, "E1188", {"start": v(-206, 30) * mm, "end": v(-206.05, 30.39) * mm});
            skLineSegment(sketch, "E1189", {"start": v(-206.05, 30.39) * mm, "end": v(-206.2, 30.75) * mm});
            skLineSegment(sketch, "E1190", {"start": v(-206.2, 30.75) * mm, "end": v(-206.44, 31.06) * mm});
            skLineSegment(sketch, "E1191", {"start": v(-206.44, 31.06) * mm, "end": v(-206.75, 31.3) * mm});
            skLineSegment(sketch, "E1192", {"start": v(-206.75, 31.3) * mm, "end": v(-207.11, 31.45) * mm});
            skLineSegment(sketch, "E1193", {"start": v(-207.11, 31.45) * mm, "end": v(-207.5, 31.5) * mm});
            skLineSegment(sketch, "E1194", {"start": v(-207.5, 31.5) * mm, "end": v(-207.89, 31.45) * mm});
            skLineSegment(sketch, "E1195", {"start": v(-207.89, 31.45) * mm, "end": v(-208.25, 31.3) * mm});
            skLineSegment(sketch, "E1196", {"start": v(-208.25, 31.3) * mm, "end": v(-208.56, 31.06) * mm});
            skLineSegment(sketch, "E1197", {"start": v(-208.56, 31.06) * mm, "end": v(-208.8, 30.75) * mm});
            skLineSegment(sketch, "E1198", {"start": v(-208.8, 30.75) * mm, "end": v(-208.95, 30.39) * mm});
            skLineSegment(sketch, "E1199", {"start": v(-208.95, 30.39) * mm, "end": v(-209, 30) * mm});
            skLineSegment(sketch, "E1200", {"start": v(-209, 30) * mm, "end": v(-208.95, 29.61) * mm});
            skLineSegment(sketch, "E1201", {"start": v(-208.95, 29.61) * mm, "end": v(-208.8, 29.25) * mm});
            skLineSegment(sketch, "E1202", {"start": v(-208.8, 29.25) * mm, "end": v(-208.56, 28.94) * mm});
            skLineSegment(sketch, "E1203", {"start": v(-208.56, 28.94) * mm, "end": v(-208.25, 28.7) * mm});
            skLineSegment(sketch, "E1204", {"start": v(-208.25, 28.7) * mm, "end": v(-207.89, 28.55) * mm});
            skLineSegment(sketch, "E1205", {"start": v(-207.89, 28.55) * mm, "end": v(-207.5, 28.5) * mm});
            skLineSegment(sketch, "E1206", {"start": v(-207.5, 28.5) * mm, "end": v(-207.11, 28.55) * mm});
            skLineSegment(sketch, "E1207", {"start": v(-207.11, 28.55) * mm, "end": v(-206.75, 28.7) * mm});
            skLineSegment(sketch, "E1208", {"start": v(-206.75, 28.7) * mm, "end": v(-206.44, 28.94) * mm});
            skLineSegment(sketch, "E1209", {"start": v(-206.44, 28.94) * mm, "end": v(-206.2, 29.25) * mm});
            skLineSegment(sketch, "E1210", {"start": v(-206.2, 29.25) * mm, "end": v(-206.05, 29.61) * mm});
            skLineSegment(sketch, "E1211", {"start": v(-206.05, 29.61) * mm, "end": v(-206, 30) * mm});
            skLineSegment(sketch, "E1212", {"start": v(-208.95, -0.39) * mm, "end": v(-208.8, -0.75) * mm});
            skLineSegment(sketch, "E1213", {"start": v(-208.8, -0.75) * mm, "end": v(-208.56, -1.06) * mm});
            skLineSegment(sketch, "E1214", {"start": v(-208.56, -1.06) * mm, "end": v(-208.25, -1.3) * mm});
            skLineSegment(sketch, "E1215", {"start": v(-208.25, -1.3) * mm, "end": v(-207.89, -1.45) * mm});
            skLineSegment(sketch, "E1216", {"start": v(-207.89, -1.45) * mm, "end": v(-207.5, -1.5) * mm});
            skLineSegment(sketch, "E1217", {"start": v(-207.5, -1.5) * mm, "end": v(-207.11, -1.45) * mm});
            skLineSegment(sketch, "E1218", {"start": v(-207.11, -1.45) * mm, "end": v(-206.75, -1.3) * mm});
            skLineSegment(sketch, "E1219", {"start": v(-206.75, -1.3) * mm, "end": v(-206.44, -1.06) * mm});
            skLineSegment(sketch, "E1220", {"start": v(-206.44, -1.06) * mm, "end": v(-206.2, -0.75) * mm});
            skLineSegment(sketch, "E1221", {"start": v(-206.2, -0.75) * mm, "end": v(-206.05, -0.39) * mm});
            skLineSegment(sketch, "E1222", {"start": v(-206.05, -0.39) * mm, "end": v(-206, 0) * mm});
            skLineSegment(sketch, "E1223", {"start": v(-206, 0) * mm, "end": v(-206.05, 0.39) * mm});
            skLineSegment(sketch, "E1224", {"start": v(-206.05, 0.39) * mm, "end": v(-206.2, 0.75) * mm});
            skLineSegment(sketch, "E1225", {"start": v(-206.2, 0.75) * mm, "end": v(-206.44, 1.06) * mm});
            skLineSegment(sketch, "E1226", {"start": v(-206.44, 1.06) * mm, "end": v(-206.75, 1.3) * mm});
            skLineSegment(sketch, "E1227", {"start": v(-206.75, 1.3) * mm, "end": v(-207.11, 1.45) * mm});
            skLineSegment(sketch, "E1228", {"start": v(-207.11, 1.45) * mm, "end": v(-207.5, 1.5) * mm});
            skLineSegment(sketch, "E1229", {"start": v(-207.5, 1.5) * mm, "end": v(-207.89, 1.45) * mm});
            skLineSegment(sketch, "E1230", {"start": v(-207.89, 1.45) * mm, "end": v(-208.25, 1.3) * mm});
            skLineSegment(sketch, "E1231", {"start": v(-208.25, 1.3) * mm, "end": v(-208.56, 1.06) * mm});
            skLineSegment(sketch, "E1232", {"start": v(-208.56, 1.06) * mm, "end": v(-208.8, 0.75) * mm});
            skLineSegment(sketch, "E1233", {"start": v(-208.8, 0.75) * mm, "end": v(-208.95, 0.39) * mm});
            skLineSegment(sketch, "E1234", {"start": v(-208.95, 0.39) * mm, "end": v(-209, 0) * mm});
            skLineSegment(sketch, "E1235", {"start": v(-209, 0) * mm, "end": v(-208.95, -0.39) * mm});
            skLineSegment(sketch, "E1236", {"start": v(-206.2, -30.75) * mm, "end": v(-206.05, -30.39) * mm});
            skLineSegment(sketch, "E1237", {"start": v(-206.05, -30.39) * mm, "end": v(-206, -30) * mm});
            skLineSegment(sketch, "E1238", {"start": v(-206, -30) * mm, "end": v(-206.05, -29.61) * mm});
            skLineSegment(sketch, "E1239", {"start": v(-206.05, -29.61) * mm, "end": v(-206.2, -29.25) * mm});
            skLineSegment(sketch, "E1240", {"start": v(-206.2, -29.25) * mm, "end": v(-206.44, -28.94) * mm});
            skLineSegment(sketch, "E1241", {"start": v(-206.44, -28.94) * mm, "end": v(-206.75, -28.7) * mm});
            skLineSegment(sketch, "E1242", {"start": v(-206.75, -28.7) * mm, "end": v(-207.11, -28.55) * mm});
            skLineSegment(sketch, "E1243", {"start": v(-207.11, -28.55) * mm, "end": v(-207.5, -28.5) * mm});
            skLineSegment(sketch, "E1244", {"start": v(-207.5, -28.5) * mm, "end": v(-207.89, -28.55) * mm});
            skLineSegment(sketch, "E1245", {"start": v(-207.89, -28.55) * mm, "end": v(-208.25, -28.7) * mm});
            skLineSegment(sketch, "E1246", {"start": v(-208.25, -28.7) * mm, "end": v(-208.56, -28.94) * mm});
            skLineSegment(sketch, "E1247", {"start": v(-208.56, -28.94) * mm, "end": v(-208.8, -29.25) * mm});
            skLineSegment(sketch, "E1248", {"start": v(-208.8, -29.25) * mm, "end": v(-208.95, -29.61) * mm});
            skLineSegment(sketch, "E1249", {"start": v(-208.95, -29.61) * mm, "end": v(-209, -30) * mm});
            skLineSegment(sketch, "E1250", {"start": v(-209, -30) * mm, "end": v(-208.95, -30.39) * mm});
            skLineSegment(sketch, "E1251", {"start": v(-208.95, -30.39) * mm, "end": v(-208.8, -30.75) * mm});
            skLineSegment(sketch, "E1252", {"start": v(-208.8, -30.75) * mm, "end": v(-208.56, -31.06) * mm});
            skLineSegment(sketch, "E1253", {"start": v(-208.56, -31.06) * mm, "end": v(-208.25, -31.3) * mm});
            skLineSegment(sketch, "E1254", {"start": v(-208.25, -31.3) * mm, "end": v(-207.89, -31.45) * mm});
            skLineSegment(sketch, "E1255", {"start": v(-207.89, -31.45) * mm, "end": v(-207.5, -31.5) * mm});
            skLineSegment(sketch, "E1256", {"start": v(-207.5, -31.5) * mm, "end": v(-207.11, -31.45) * mm});
            skLineSegment(sketch, "E1257", {"start": v(-207.11, -31.45) * mm, "end": v(-206.75, -31.3) * mm});
            skLineSegment(sketch, "E1258", {"start": v(-206.75, -31.3) * mm, "end": v(-206.44, -31.06) * mm});
            skLineSegment(sketch, "E1259", {"start": v(-206.44, -31.06) * mm, "end": v(-206.2, -30.75) * mm});
            skSolve(sketch);
        }
        {
            var Q0;
            Q0=makeQuery(id+"F9.imprint","IMPRINT",FACE,{"disambiguationData":[TD([[makeQuery(id+"F9.imprint","IMPRINT",EDGE,{"derivedFrom":sQuery(id+"F9.wireOp",EDGE,"E1112")}),-1.0]])]});
            extrude(context, id + "F10", {"entities" : qUnion([Q0]), "depth" : 15 * mm});
        }
        {
            var Q0;
            Q0=qCreatedBy(id+"F3.planeOp",FACE);
            cPlane(context, id + "F11", {"entities" : qUnion([Q0]), "cplaneType" : CPlaneType.OFFSET, "offset" : 100 * mm, "oppositeDirection" : true, "width" : 150 * mm, "height" : 150 * mm});
        }
        {
            var Q0;
            Q0=qCreatedBy(id+"F11.planeOp",FACE);
            var sketch = newSketch(context, id + "F12", { "sketchPlane" : qUnion([Q0])});
            skLineSegment(sketch, "E1260", {"start": v(-150, -82.5) * mm, "end": v(-150, 57.5) * mm});
            skLineSegment(sketch, "E1261", {"start": v(-150, 57.5) * mm, "end": v(-149.84, 58.43) * mm});
            skLineSegment(sketch, "E1262", {"start": v(-149.84, 58.43) * mm, "end": v(-149.63, 59.36) * mm});
            skLineSegment(sketch, "E1263", {"start": v(-149.63, 59.36) * mm, "end": v(-149.37, 60.27) * mm});
            skLineSegment(sketch, "E1264", {"start": v(-149.37, 60.27) * mm, "end": v(-149.07, 61.17) * mm});
            skLineSegment(sketch, "E1265", {"start": v(-149.07, 61.17) * mm, "end": v(-148.71, 62.05) * mm});
            skLineSegment(sketch, "E1266", {"start": v(-148.71, 62.05) * mm, "end": v(-148.31, 62.9) * mm});
            skLineSegment(sketch, "E1267", {"start": v(-148.31, 62.9) * mm, "end": v(-147.86, 63.74) * mm});
            skLineSegment(sketch, "E1268", {"start": v(-147.86, 63.74) * mm, "end": v(-147.37, 64.55) * mm});
            skLineSegment(sketch, "E1269", {"start": v(-147.37, 64.55) * mm, "end": v(-146.84, 65.34) * mm});
            skLineSegment(sketch, "E1270", {"start": v(-146.84, 65.34) * mm, "end": v(-146.27, 66.1) * mm});
            skLineSegment(sketch, "E1271", {"start": v(-146.27, 66.1) * mm, "end": v(-145.65, 66.81) * mm});
            skLineSegment(sketch, "E1272", {"start": v(-145.65, 66.81) * mm, "end": v(-145, 67.5) * mm});
            skLineSegment(sketch, "E1273", {"start": v(-145, 67.5) * mm, "end": v(-130, 82.5) * mm});
            skLineSegment(sketch, "E1274", {"start": v(-130, 82.5) * mm, "end": v(-129.4, 83.25) * mm});
            skLineSegment(sketch, "E1275", {"start": v(-129.4, 83.25) * mm, "end": v(-128.73, 83.95) * mm});
            skLineSegment(sketch, "E1276", {"start": v(-128.73, 83.95) * mm, "end": v(-128, 84.6) * mm});
            skLineSegment(sketch, "E1277", {"start": v(-128, 84.6) * mm, "end": v(-127.24, 85.19) * mm});
            skLineSegment(sketch, "E1278", {"start": v(-127.24, 85.19) * mm, "end": v(-126.44, 85.72) * mm});
            skLineSegment(sketch, "E1279", {"start": v(-126.44, 85.72) * mm, "end": v(-125.6, 86.18) * mm});
            skLineSegment(sketch, "E1280", {"start": v(-125.6, 86.18) * mm, "end": v(-124.71, 86.58) * mm});
            skLineSegment(sketch, "E1281", {"start": v(-124.71, 86.58) * mm, "end": v(-123.8, 86.9) * mm});
            skLineSegment(sketch, "E1282", {"start": v(-123.8, 86.9) * mm, "end": v(-122.87, 87.17) * mm});
            skLineSegment(sketch, "E1283", {"start": v(-122.87, 87.17) * mm, "end": v(-121.92, 87.35) * mm});
            skLineSegment(sketch, "E1284", {"start": v(-121.92, 87.35) * mm, "end": v(-120.96, 87.46) * mm});
            skLineSegment(sketch, "E1285", {"start": v(-120.96, 87.46) * mm, "end": v(-120, 87.5) * mm});
            skLineSegment(sketch, "E1286", {"start": v(-120, 87.5) * mm, "end": v(50, 87.5) * mm});
            skLineSegment(sketch, "E1287", {"start": v(50, 87.5) * mm, "end": v(50, 72.5) * mm});
            skLineSegment(sketch, "E1288", {"start": v(50, 72.5) * mm, "end": v(150, 72.5) * mm});
            skLineSegment(sketch, "E1289", {"start": v(150, 72.5) * mm, "end": v(150, -7.5) * mm});
            skLineSegment(sketch, "E1290", {"start": v(150, -7.5) * mm, "end": v(149.96, -8.15) * mm});
            skLineSegment(sketch, "E1291", {"start": v(149.96, -8.15) * mm, "end": v(149.83, -8.8) * mm});
            skLineSegment(sketch, "E1292", {"start": v(149.83, -8.8) * mm, "end": v(149.62, -9.41) * mm});
            skLineSegment(sketch, "E1293", {"start": v(149.62, -9.41) * mm, "end": v(149.33, -10) * mm});
            skLineSegment(sketch, "E1294", {"start": v(149.33, -10) * mm, "end": v(148.97, -10.54) * mm});
            skLineSegment(sketch, "E1295", {"start": v(148.97, -10.54) * mm, "end": v(148.54, -11.04) * mm});
            skLineSegment(sketch, "E1296", {"start": v(148.54, -11.04) * mm, "end": v(148.04, -11.47) * mm});
            skLineSegment(sketch, "E1297", {"start": v(148.04, -11.47) * mm, "end": v(147.5, -11.83) * mm});
            skLineSegment(sketch, "E1298", {"start": v(147.5, -11.83) * mm, "end": v(146.91, -12.12) * mm});
            skLineSegment(sketch, "E1299", {"start": v(146.91, -12.12) * mm, "end": v(146.3, -12.33) * mm});
            skLineSegment(sketch, "E1300", {"start": v(146.3, -12.33) * mm, "end": v(145.65, -12.46) * mm});
            skLineSegment(sketch, "E1301", {"start": v(145.65, -12.46) * mm, "end": v(145, -12.5) * mm});
            skLineSegment(sketch, "E1302", {"start": v(145, -12.5) * mm, "end": v(-90, -12.5) * mm});
            skLineSegment(sketch, "E1303", {"start": v(-90, -12.5) * mm, "end": v(-90, -57.5) * mm});
            skLineSegment(sketch, "E1304", {"start": v(-90, -57.5) * mm, "end": v(-90.16, -58.43) * mm});
            skLineSegment(sketch, "E1305", {"start": v(-90.16, -58.43) * mm, "end": v(-90.37, -59.36) * mm});
            skLineSegment(sketch, "E1306", {"start": v(-90.37, -59.36) * mm, "end": v(-90.63, -60.27) * mm});
            skLineSegment(sketch, "E1307", {"start": v(-90.63, -60.27) * mm, "end": v(-90.93, -61.17) * mm});
            skLineSegment(sketch, "E1308", {"start": v(-90.93, -61.17) * mm, "end": v(-91.29, -62.05) * mm});
            skLineSegment(sketch, "E1309", {"start": v(-91.29, -62.05) * mm, "end": v(-91.69, -62.9) * mm});
            skLineSegment(sketch, "E1310", {"start": v(-91.69, -62.9) * mm, "end": v(-92.14, -63.74) * mm});
            skLineSegment(sketch, "E1311", {"start": v(-92.14, -63.74) * mm, "end": v(-92.63, -64.55) * mm});
            skLineSegment(sketch, "E1312", {"start": v(-92.63, -64.55) * mm, "end": v(-93.16, -65.34) * mm});
            skLineSegment(sketch, "E1313", {"start": v(-93.16, -65.34) * mm, "end": v(-93.73, -66.1) * mm});
            skLineSegment(sketch, "E1314", {"start": v(-93.73, -66.1) * mm, "end": v(-94.35, -66.81) * mm});
            skLineSegment(sketch, "E1315", {"start": v(-94.35, -66.81) * mm, "end": v(-95, -67.5) * mm});
            skLineSegment(sketch, "E1316", {"start": v(-95, -67.5) * mm, "end": v(-110, -82.5) * mm});
            skLineSegment(sketch, "E1317", {"start": v(-110, -82.5) * mm, "end": v(-110.69, -83.15) * mm});
            skLineSegment(sketch, "E1318", {"start": v(-110.69, -83.15) * mm, "end": v(-111.4, -83.77) * mm});
            skLineSegment(sketch, "E1319", {"start": v(-111.4, -83.77) * mm, "end": v(-112.16, -84.34) * mm});
            skLineSegment(sketch, "E1320", {"start": v(-112.16, -84.34) * mm, "end": v(-112.95, -84.87) * mm});
            skLineSegment(sketch, "E1321", {"start": v(-112.95, -84.87) * mm, "end": v(-113.76, -85.36) * mm});
            skLineSegment(sketch, "E1322", {"start": v(-113.76, -85.36) * mm, "end": v(-114.6, -85.81) * mm});
            skLineSegment(sketch, "E1323", {"start": v(-114.6, -85.81) * mm, "end": v(-115.45, -86.21) * mm});
            skLineSegment(sketch, "E1324", {"start": v(-115.45, -86.21) * mm, "end": v(-116.33, -86.57) * mm});
            skLineSegment(sketch, "E1325", {"start": v(-116.33, -86.57) * mm, "end": v(-117.23, -86.87) * mm});
            skLineSegment(sketch, "E1326", {"start": v(-117.23, -86.87) * mm, "end": v(-118.14, -87.13) * mm});
            skLineSegment(sketch, "E1327", {"start": v(-118.14, -87.13) * mm, "end": v(-119.07, -87.34) * mm});
            skLineSegment(sketch, "E1328", {"start": v(-119.07, -87.34) * mm, "end": v(-120, -87.5) * mm});
            skLineSegment(sketch, "E1329", {"start": v(-120, -87.5) * mm, "end": v(-145, -87.5) * mm});
            skLineSegment(sketch, "E1330", {"start": v(-145, -87.5) * mm, "end": v(-145.65, -87.46) * mm});
            skLineSegment(sketch, "E1331", {"start": v(-145.65, -87.46) * mm, "end": v(-146.3, -87.33) * mm});
            skLineSegment(sketch, "E1332", {"start": v(-146.3, -87.33) * mm, "end": v(-146.91, -87.12) * mm});
            skLineSegment(sketch, "E1333", {"start": v(-146.91, -87.12) * mm, "end": v(-147.5, -86.83) * mm});
            skLineSegment(sketch, "E1334", {"start": v(-147.5, -86.83) * mm, "end": v(-148.04, -86.47) * mm});
            skLineSegment(sketch, "E1335", {"start": v(-148.04, -86.47) * mm, "end": v(-148.54, -86.04) * mm});
            skLineSegment(sketch, "E1336", {"start": v(-148.54, -86.04) * mm, "end": v(-148.97, -85.54) * mm});
            skLineSegment(sketch, "E1337", {"start": v(-148.97, -85.54) * mm, "end": v(-149.33, -85) * mm});
            skLineSegment(sketch, "E1338", {"start": v(-149.33, -85) * mm, "end": v(-149.62, -84.41) * mm});
            skLineSegment(sketch, "E1339", {"start": v(-149.62, -84.41) * mm, "end": v(-149.83, -83.8) * mm});
            skLineSegment(sketch, "E1340", {"start": v(-149.83, -83.8) * mm, "end": v(-149.96, -83.15) * mm});
            skLineSegment(sketch, "E1341", {"start": v(-149.96, -83.15) * mm, "end": v(-150, -82.5) * mm});
            skLineSegment(sketch, "E1342", {"start": v(-122.83, -70.33) * mm, "end": v(-122, -70.96) * mm});
            skLineSegment(sketch, "E1343", {"start": v(-122, -70.96) * mm, "end": v(-121.04, -71.36) * mm});
            skLineSegment(sketch, "E1344", {"start": v(-121.04, -71.36) * mm, "end": v(-120, -71.5) * mm});
            skLineSegment(sketch, "E1345", {"start": v(-120, -71.5) * mm, "end": v(-118.96, -71.36) * mm});
            skLineSegment(sketch, "E1346", {"start": v(-118.96, -71.36) * mm, "end": v(-118, -70.96) * mm});
            skLineSegment(sketch, "E1347", {"start": v(-118, -70.96) * mm, "end": v(-117.17, -70.33) * mm});
            skLineSegment(sketch, "E1348", {"start": v(-117.17, -70.33) * mm, "end": v(-116.54, -69.5) * mm});
            skLineSegment(sketch, "E1349", {"start": v(-116.54, -69.5) * mm, "end": v(-116.14, -68.54) * mm});
            skLineSegment(sketch, "E1350", {"start": v(-116.14, -68.54) * mm, "end": v(-116, -67.5) * mm});
            skLineSegment(sketch, "E1351", {"start": v(-116, -67.5) * mm, "end": v(-116.14, -66.46) * mm});
            skLineSegment(sketch, "E1352", {"start": v(-116.14, -66.46) * mm, "end": v(-116.54, -65.5) * mm});
            skLineSegment(sketch, "E1353", {"start": v(-116.54, -65.5) * mm, "end": v(-117.17, -64.67) * mm});
            skLineSegment(sketch, "E1354", {"start": v(-117.17, -64.67) * mm, "end": v(-118, -64.04) * mm});
            skLineSegment(sketch, "E1355", {"start": v(-118, -64.04) * mm, "end": v(-118.96, -63.64) * mm});
            skLineSegment(sketch, "E1356", {"start": v(-118.96, -63.64) * mm, "end": v(-120, -63.5) * mm});
            skLineSegment(sketch, "E1357", {"start": v(-120, -63.5) * mm, "end": v(-121.04, -63.64) * mm});
            skLineSegment(sketch, "E1358", {"start": v(-121.04, -63.64) * mm, "end": v(-122, -64.04) * mm});
            skLineSegment(sketch, "E1359", {"start": v(-122, -64.04) * mm, "end": v(-122.83, -64.67) * mm});
            skLineSegment(sketch, "E1360", {"start": v(-122.83, -64.67) * mm, "end": v(-123.46, -65.5) * mm});
            skLineSegment(sketch, "E1361", {"start": v(-123.46, -65.5) * mm, "end": v(-123.86, -66.46) * mm});
            skLineSegment(sketch, "E1362", {"start": v(-123.86, -66.46) * mm, "end": v(-124, -67.5) * mm});
            skLineSegment(sketch, "E1363", {"start": v(-124, -67.5) * mm, "end": v(-123.86, -68.54) * mm});
            skLineSegment(sketch, "E1364", {"start": v(-123.86, -68.54) * mm, "end": v(-123.46, -69.5) * mm});
            skLineSegment(sketch, "E1365", {"start": v(-123.46, -69.5) * mm, "end": v(-122.83, -70.33) * mm});
            skLineSegment(sketch, "E1366", {"start": v(-117.17, 0.33) * mm, "end": v(-118, 0.96) * mm});
            skLineSegment(sketch, "E1367", {"start": v(-118, 0.96) * mm, "end": v(-118.96, 1.36) * mm});
            skLineSegment(sketch, "E1368", {"start": v(-118.96, 1.36) * mm, "end": v(-120, 1.5) * mm});
            skLineSegment(sketch, "E1369", {"start": v(-120, 1.5) * mm, "end": v(-121.04, 1.36) * mm});
            skLineSegment(sketch, "E1370", {"start": v(-121.04, 1.36) * mm, "end": v(-122, 0.96) * mm});
            skLineSegment(sketch, "E1371", {"start": v(-122, 0.96) * mm, "end": v(-122.83, 0.33) * mm});
            skLineSegment(sketch, "E1372", {"start": v(-122.83, 0.33) * mm, "end": v(-123.46, -0.5) * mm});
            skLineSegment(sketch, "E1373", {"start": v(-123.46, -0.5) * mm, "end": v(-123.86, -1.46) * mm});
            skLineSegment(sketch, "E1374", {"start": v(-123.86, -1.46) * mm, "end": v(-124, -2.5) * mm});
            skLineSegment(sketch, "E1375", {"start": v(-124, -2.5) * mm, "end": v(-123.86, -3.54) * mm});
            skLineSegment(sketch, "E1376", {"start": v(-123.86, -3.54) * mm, "end": v(-123.46, -4.5) * mm});
            skLineSegment(sketch, "E1377", {"start": v(-123.46, -4.5) * mm, "end": v(-122.83, -5.33) * mm});
            skLineSegment(sketch, "E1378", {"start": v(-122.83, -5.33) * mm, "end": v(-122, -5.96) * mm});
            skLineSegment(sketch, "E1379", {"start": v(-122, -5.96) * mm, "end": v(-121.04, -6.36) * mm});
            skLineSegment(sketch, "E1380", {"start": v(-121.04, -6.36) * mm, "end": v(-120, -6.5) * mm});
            skLineSegment(sketch, "E1381", {"start": v(-120, -6.5) * mm, "end": v(-118.96, -6.36) * mm});
            skLineSegment(sketch, "E1382", {"start": v(-118.96, -6.36) * mm, "end": v(-118, -5.96) * mm});
            skLineSegment(sketch, "E1383", {"start": v(-118, -5.96) * mm, "end": v(-117.17, -5.33) * mm});
            skLineSegment(sketch, "E1384", {"start": v(-117.17, -5.33) * mm, "end": v(-116.54, -4.5) * mm});
            skLineSegment(sketch, "E1385", {"start": v(-116.54, -4.5) * mm, "end": v(-116.14, -3.54) * mm});
            skLineSegment(sketch, "E1386", {"start": v(-116.14, -3.54) * mm, "end": v(-116, -2.5) * mm});
            skLineSegment(sketch, "E1387", {"start": v(-116, -2.5) * mm, "end": v(-116.14, -1.46) * mm});
            skLineSegment(sketch, "E1388", {"start": v(-116.14, -1.46) * mm, "end": v(-116.54, -0.5) * mm});
            skLineSegment(sketch, "E1389", {"start": v(-116.54, -0.5) * mm, "end": v(-117.17, 0.33) * mm});
            skLineSegment(sketch, "E1390", {"start": v(-118, 59.04) * mm, "end": v(-117.17, 59.67) * mm});
            skLineSegment(sketch, "E1391", {"start": v(-117.17, 59.67) * mm, "end": v(-116.54, 60.5) * mm});
            skLineSegment(sketch, "E1392", {"start": v(-116.54, 60.5) * mm, "end": v(-116.14, 61.46) * mm});
            skLineSegment(sketch, "E1393", {"start": v(-116.14, 61.46) * mm, "end": v(-116, 62.5) * mm});
            skLineSegment(sketch, "E1394", {"start": v(-116, 62.5) * mm, "end": v(-116.14, 63.54) * mm});
            skLineSegment(sketch, "E1395", {"start": v(-116.14, 63.54) * mm, "end": v(-116.54, 64.5) * mm});
            skLineSegment(sketch, "E1396", {"start": v(-116.54, 64.5) * mm, "end": v(-117.17, 65.33) * mm});
            skLineSegment(sketch, "E1397", {"start": v(-117.17, 65.33) * mm, "end": v(-118, 65.96) * mm});
            skLineSegment(sketch, "E1398", {"start": v(-118, 65.96) * mm, "end": v(-118.96, 66.36) * mm});
            skLineSegment(sketch, "E1399", {"start": v(-118.96, 66.36) * mm, "end": v(-120, 66.5) * mm});
            skLineSegment(sketch, "E1400", {"start": v(-120, 66.5) * mm, "end": v(-121.04, 66.36) * mm});
            skLineSegment(sketch, "E1401", {"start": v(-121.04, 66.36) * mm, "end": v(-122, 65.96) * mm});
            skLineSegment(sketch, "E1402", {"start": v(-122, 65.96) * mm, "end": v(-122.83, 65.33) * mm});
            skLineSegment(sketch, "E1403", {"start": v(-122.83, 65.33) * mm, "end": v(-123.46, 64.5) * mm});
            skLineSegment(sketch, "E1404", {"start": v(-123.46, 64.5) * mm, "end": v(-123.86, 63.54) * mm});
            skLineSegment(sketch, "E1405", {"start": v(-123.86, 63.54) * mm, "end": v(-124, 62.5) * mm});
            skLineSegment(sketch, "E1406", {"start": v(-124, 62.5) * mm, "end": v(-123.86, 61.46) * mm});
            skLineSegment(sketch, "E1407", {"start": v(-123.86, 61.46) * mm, "end": v(-123.46, 60.5) * mm});
            skLineSegment(sketch, "E1408", {"start": v(-123.46, 60.5) * mm, "end": v(-122.83, 59.67) * mm});
            skLineSegment(sketch, "E1409", {"start": v(-122.83, 59.67) * mm, "end": v(-122, 59.04) * mm});
            skLineSegment(sketch, "E1410", {"start": v(-122, 59.04) * mm, "end": v(-121.04, 58.64) * mm});
            skLineSegment(sketch, "E1411", {"start": v(-121.04, 58.64) * mm, "end": v(-120, 58.5) * mm});
            skLineSegment(sketch, "E1412", {"start": v(-120, 58.5) * mm, "end": v(-118.96, 58.64) * mm});
            skLineSegment(sketch, "E1413", {"start": v(-118.96, 58.64) * mm, "end": v(-118, 59.04) * mm});
            skLineSegment(sketch, "E1414", {"start": v(72.15, 48.13) * mm, "end": v(69.5, 47.03) * mm});
            skLineSegment(sketch, "E1415", {"start": v(69.5, 47.03) * mm, "end": v(67.22, 45.28) * mm});
            skLineSegment(sketch, "E1416", {"start": v(67.22, 45.28) * mm, "end": v(65.47, 43) * mm});
            skLineSegment(sketch, "E1417", {"start": v(65.47, 43) * mm, "end": v(64.37, 40.35) * mm});
            skLineSegment(sketch, "E1418", {"start": v(64.37, 40.35) * mm, "end": v(64, 37.5) * mm});
            skLineSegment(sketch, "E1419", {"start": v(64, 37.5) * mm, "end": v(64.37, 34.65) * mm});
            skLineSegment(sketch, "E1420", {"start": v(64.37, 34.65) * mm, "end": v(65.47, 32) * mm});
            skLineSegment(sketch, "E1421", {"start": v(65.47, 32) * mm, "end": v(67.22, 29.72) * mm});
            skLineSegment(sketch, "E1422", {"start": v(67.22, 29.72) * mm, "end": v(69.5, 27.97) * mm});
            skLineSegment(sketch, "E1423", {"start": v(69.5, 27.97) * mm, "end": v(72.15, 26.87) * mm});
            skLineSegment(sketch, "E1424", {"start": v(72.15, 26.87) * mm, "end": v(75, 26.5) * mm});
            skLineSegment(sketch, "E1425", {"start": v(75, 26.5) * mm, "end": v(77.85, 26.87) * mm});
            skLineSegment(sketch, "E1426", {"start": v(77.85, 26.87) * mm, "end": v(80.5, 27.97) * mm});
            skLineSegment(sketch, "E1427", {"start": v(80.5, 27.97) * mm, "end": v(82.78, 29.72) * mm});
            skLineSegment(sketch, "E1428", {"start": v(82.78, 29.72) * mm, "end": v(84.53, 32) * mm});
            skLineSegment(sketch, "E1429", {"start": v(84.53, 32) * mm, "end": v(85.63, 34.65) * mm});
            skLineSegment(sketch, "E1430", {"start": v(85.63, 34.65) * mm, "end": v(86, 37.5) * mm});
            skLineSegment(sketch, "E1431", {"start": v(86, 37.5) * mm, "end": v(85.63, 40.35) * mm});
            skLineSegment(sketch, "E1432", {"start": v(85.63, 40.35) * mm, "end": v(84.53, 43) * mm});
            skLineSegment(sketch, "E1433", {"start": v(84.53, 43) * mm, "end": v(82.78, 45.28) * mm});
            skLineSegment(sketch, "E1434", {"start": v(82.78, 45.28) * mm, "end": v(80.5, 47.03) * mm});
            skLineSegment(sketch, "E1435", {"start": v(80.5, 47.03) * mm, "end": v(77.85, 48.13) * mm});
            skLineSegment(sketch, "E1436", {"start": v(77.85, 48.13) * mm, "end": v(75, 48.5) * mm});
            skLineSegment(sketch, "E1437", {"start": v(75, 48.5) * mm, "end": v(72.15, 48.13) * mm});
            skLineSegment(sketch, "E1438", {"start": v(97.8, 15.25) * mm, "end": v(97.49, 15.01) * mm});
            skLineSegment(sketch, "E1439", {"start": v(97.49, 15.01) * mm, "end": v(97.25, 14.7) * mm});
            skLineSegment(sketch, "E1440", {"start": v(97.25, 14.7) * mm, "end": v(97.1, 14.34) * mm});
            skLineSegment(sketch, "E1441", {"start": v(97.1, 14.34) * mm, "end": v(97.05, 13.95) * mm});
            skLineSegment(sketch, "E1442", {"start": v(97.05, 13.95) * mm, "end": v(97.1, 13.56) * mm});
            skLineSegment(sketch, "E1443", {"start": v(97.1, 13.56) * mm, "end": v(97.25, 13.2) * mm});
            skLineSegment(sketch, "E1444", {"start": v(97.25, 13.2) * mm, "end": v(97.49, 12.89) * mm});
            skLineSegment(sketch, "E1445", {"start": v(97.49, 12.89) * mm, "end": v(97.8, 12.65) * mm});
            skLineSegment(sketch, "E1446", {"start": v(97.8, 12.65) * mm, "end": v(98.16, 12.5) * mm});
            skLineSegment(sketch, "E1447", {"start": v(98.16, 12.5) * mm, "end": v(98.55, 12.45) * mm});
            skLineSegment(sketch, "E1448", {"start": v(98.55, 12.45) * mm, "end": v(98.94, 12.5) * mm});
            skLineSegment(sketch, "E1449", {"start": v(98.94, 12.5) * mm, "end": v(99.3, 12.65) * mm});
            skLineSegment(sketch, "E1450", {"start": v(99.3, 12.65) * mm, "end": v(99.61, 12.89) * mm});
            skLineSegment(sketch, "E1451", {"start": v(99.61, 12.89) * mm, "end": v(99.85, 13.2) * mm});
            skLineSegment(sketch, "E1452", {"start": v(99.85, 13.2) * mm, "end": v(100, 13.56) * mm});
            skLineSegment(sketch, "E1453", {"start": v(100, 13.56) * mm, "end": v(100.05, 13.95) * mm});
            skLineSegment(sketch, "E1454", {"start": v(100.05, 13.95) * mm, "end": v(100, 14.34) * mm});
            skLineSegment(sketch, "E1455", {"start": v(100, 14.34) * mm, "end": v(99.85, 14.7) * mm});
            skLineSegment(sketch, "E1456", {"start": v(99.85, 14.7) * mm, "end": v(99.61, 15.01) * mm});
            skLineSegment(sketch, "E1457", {"start": v(99.61, 15.01) * mm, "end": v(99.3, 15.25) * mm});
            skLineSegment(sketch, "E1458", {"start": v(99.3, 15.25) * mm, "end": v(98.94, 15.4) * mm});
            skLineSegment(sketch, "E1459", {"start": v(98.94, 15.4) * mm, "end": v(98.55, 15.45) * mm});
            skLineSegment(sketch, "E1460", {"start": v(98.55, 15.45) * mm, "end": v(98.16, 15.4) * mm});
            skLineSegment(sketch, "E1461", {"start": v(98.16, 15.4) * mm, "end": v(97.8, 15.25) * mm});
            skLineSegment(sketch, "E1462", {"start": v(51.45, 15.45) * mm, "end": v(51.06, 15.4) * mm});
            skLineSegment(sketch, "E1463", {"start": v(51.06, 15.4) * mm, "end": v(50.7, 15.25) * mm});
            skLineSegment(sketch, "E1464", {"start": v(50.7, 15.25) * mm, "end": v(50.39, 15.01) * mm});
            skLineSegment(sketch, "E1465", {"start": v(50.39, 15.01) * mm, "end": v(50.15, 14.7) * mm});
            skLineSegment(sketch, "E1466", {"start": v(50.15, 14.7) * mm, "end": v(50, 14.34) * mm});
            skLineSegment(sketch, "E1467", {"start": v(50, 14.34) * mm, "end": v(49.95, 13.95) * mm});
            skLineSegment(sketch, "E1468", {"start": v(49.95, 13.95) * mm, "end": v(50, 13.56) * mm});
            skLineSegment(sketch, "E1469", {"start": v(50, 13.56) * mm, "end": v(50.15, 13.2) * mm});
            skLineSegment(sketch, "E1470", {"start": v(50.15, 13.2) * mm, "end": v(50.39, 12.89) * mm});
            skLineSegment(sketch, "E1471", {"start": v(50.39, 12.89) * mm, "end": v(50.7, 12.65) * mm});
            skLineSegment(sketch, "E1472", {"start": v(50.7, 12.65) * mm, "end": v(51.06, 12.5) * mm});
            skLineSegment(sketch, "E1473", {"start": v(51.06, 12.5) * mm, "end": v(51.45, 12.45) * mm});
            skLineSegment(sketch, "E1474", {"start": v(51.45, 12.45) * mm, "end": v(51.84, 12.5) * mm});
            skLineSegment(sketch, "E1475", {"start": v(51.84, 12.5) * mm, "end": v(52.2, 12.65) * mm});
            skLineSegment(sketch, "E1476", {"start": v(52.2, 12.65) * mm, "end": v(52.51, 12.89) * mm});
            skLineSegment(sketch, "E1477", {"start": v(52.51, 12.89) * mm, "end": v(52.75, 13.2) * mm});
            skLineSegment(sketch, "E1478", {"start": v(52.75, 13.2) * mm, "end": v(52.9, 13.56) * mm});
            skLineSegment(sketch, "E1479", {"start": v(52.9, 13.56) * mm, "end": v(52.95, 13.95) * mm});
            skLineSegment(sketch, "E1480", {"start": v(52.95, 13.95) * mm, "end": v(52.9, 14.34) * mm});
            skLineSegment(sketch, "E1481", {"start": v(52.9, 14.34) * mm, "end": v(52.75, 14.7) * mm});
            skLineSegment(sketch, "E1482", {"start": v(52.75, 14.7) * mm, "end": v(52.51, 15.01) * mm});
            skLineSegment(sketch, "E1483", {"start": v(52.51, 15.01) * mm, "end": v(52.2, 15.25) * mm});
            skLineSegment(sketch, "E1484", {"start": v(52.2, 15.25) * mm, "end": v(51.84, 15.4) * mm});
            skLineSegment(sketch, "E1485", {"start": v(51.84, 15.4) * mm, "end": v(51.45, 15.45) * mm});
            skLineSegment(sketch, "E1486", {"start": v(50, 61.44) * mm, "end": v(49.95, 61.05) * mm});
            skLineSegment(sketch, "E1487", {"start": v(49.95, 61.05) * mm, "end": v(50, 60.66) * mm});
            skLineSegment(sketch, "E1488", {"start": v(50, 60.66) * mm, "end": v(50.15, 60.3) * mm});
            skLineSegment(sketch, "E1489", {"start": v(50.15, 60.3) * mm, "end": v(50.39, 59.99) * mm});
            skLineSegment(sketch, "E1490", {"start": v(50.39, 59.99) * mm, "end": v(50.7, 59.75) * mm});
            skLineSegment(sketch, "E1491", {"start": v(50.7, 59.75) * mm, "end": v(51.06, 59.6) * mm});
            skLineSegment(sketch, "E1492", {"start": v(51.06, 59.6) * mm, "end": v(51.45, 59.55) * mm});
            skLineSegment(sketch, "E1493", {"start": v(51.45, 59.55) * mm, "end": v(51.84, 59.6) * mm});
            skLineSegment(sketch, "E1494", {"start": v(51.84, 59.6) * mm, "end": v(52.2, 59.75) * mm});
            skLineSegment(sketch, "E1495", {"start": v(52.2, 59.75) * mm, "end": v(52.51, 59.99) * mm});
            skLineSegment(sketch, "E1496", {"start": v(52.51, 59.99) * mm, "end": v(52.75, 60.3) * mm});
            skLineSegment(sketch, "E1497", {"start": v(52.75, 60.3) * mm, "end": v(52.9, 60.66) * mm});
            skLineSegment(sketch, "E1498", {"start": v(52.9, 60.66) * mm, "end": v(52.95, 61.05) * mm});
            skLineSegment(sketch, "E1499", {"start": v(52.95, 61.05) * mm, "end": v(52.9, 61.44) * mm});
            skLineSegment(sketch, "E1500", {"start": v(52.9, 61.44) * mm, "end": v(52.75, 61.8) * mm});
            skLineSegment(sketch, "E1501", {"start": v(52.75, 61.8) * mm, "end": v(52.51, 62.11) * mm});
            skLineSegment(sketch, "E1502", {"start": v(52.51, 62.11) * mm, "end": v(52.2, 62.35) * mm});
            skLineSegment(sketch, "E1503", {"start": v(52.2, 62.35) * mm, "end": v(51.84, 62.5) * mm});
            skLineSegment(sketch, "E1504", {"start": v(51.84, 62.5) * mm, "end": v(51.45, 62.55) * mm});
            skLineSegment(sketch, "E1505", {"start": v(51.45, 62.55) * mm, "end": v(51.06, 62.5) * mm});
            skLineSegment(sketch, "E1506", {"start": v(51.06, 62.5) * mm, "end": v(50.7, 62.35) * mm});
            skLineSegment(sketch, "E1507", {"start": v(50.7, 62.35) * mm, "end": v(50.39, 62.11) * mm});
            skLineSegment(sketch, "E1508", {"start": v(50.39, 62.11) * mm, "end": v(50.15, 61.8) * mm});
            skLineSegment(sketch, "E1509", {"start": v(50.15, 61.8) * mm, "end": v(50, 61.44) * mm});
            skLineSegment(sketch, "E1510", {"start": v(98.16, 59.6) * mm, "end": v(98.55, 59.55) * mm});
            skLineSegment(sketch, "E1511", {"start": v(98.55, 59.55) * mm, "end": v(98.94, 59.6) * mm});
            skLineSegment(sketch, "E1512", {"start": v(98.94, 59.6) * mm, "end": v(99.3, 59.75) * mm});
            skLineSegment(sketch, "E1513", {"start": v(99.3, 59.75) * mm, "end": v(99.61, 59.99) * mm});
            skLineSegment(sketch, "E1514", {"start": v(99.61, 59.99) * mm, "end": v(99.85, 60.3) * mm});
            skLineSegment(sketch, "E1515", {"start": v(99.85, 60.3) * mm, "end": v(100, 60.66) * mm});
            skLineSegment(sketch, "E1516", {"start": v(100, 60.66) * mm, "end": v(100.05, 61.05) * mm});
            skLineSegment(sketch, "E1517", {"start": v(100.05, 61.05) * mm, "end": v(100, 61.44) * mm});
            skLineSegment(sketch, "E1518", {"start": v(100, 61.44) * mm, "end": v(99.85, 61.8) * mm});
            skLineSegment(sketch, "E1519", {"start": v(99.85, 61.8) * mm, "end": v(99.61, 62.11) * mm});
            skLineSegment(sketch, "E1520", {"start": v(99.61, 62.11) * mm, "end": v(99.3, 62.35) * mm});
            skLineSegment(sketch, "E1521", {"start": v(99.3, 62.35) * mm, "end": v(98.94, 62.5) * mm});
            skLineSegment(sketch, "E1522", {"start": v(98.94, 62.5) * mm, "end": v(98.55, 62.55) * mm});
            skLineSegment(sketch, "E1523", {"start": v(98.55, 62.55) * mm, "end": v(98.16, 62.5) * mm});
            skLineSegment(sketch, "E1524", {"start": v(98.16, 62.5) * mm, "end": v(97.8, 62.35) * mm});
            skLineSegment(sketch, "E1525", {"start": v(97.8, 62.35) * mm, "end": v(97.49, 62.11) * mm});
            skLineSegment(sketch, "E1526", {"start": v(97.49, 62.11) * mm, "end": v(97.25, 61.8) * mm});
            skLineSegment(sketch, "E1527", {"start": v(97.25, 61.8) * mm, "end": v(97.1, 61.44) * mm});
            skLineSegment(sketch, "E1528", {"start": v(97.1, 61.44) * mm, "end": v(97.05, 61.05) * mm});
            skLineSegment(sketch, "E1529", {"start": v(97.05, 61.05) * mm, "end": v(97.1, 60.66) * mm});
            skLineSegment(sketch, "E1530", {"start": v(97.1, 60.66) * mm, "end": v(97.25, 60.3) * mm});
            skLineSegment(sketch, "E1531", {"start": v(97.25, 60.3) * mm, "end": v(97.49, 59.99) * mm});
            skLineSegment(sketch, "E1532", {"start": v(97.49, 59.99) * mm, "end": v(97.8, 59.75) * mm});
            skLineSegment(sketch, "E1533", {"start": v(97.8, 59.75) * mm, "end": v(98.16, 59.6) * mm});
            skLineSegment(sketch, "E1534", {"start": v(51.63, 37.89) * mm, "end": v(51.58, 37.5) * mm});
            skLineSegment(sketch, "E1535", {"start": v(51.58, 37.5) * mm, "end": v(51.63, 37.11) * mm});
            skLineSegment(sketch, "E1536", {"start": v(51.63, 37.11) * mm, "end": v(51.78, 36.75) * mm});
            skLineSegment(sketch, "E1537", {"start": v(51.78, 36.75) * mm, "end": v(52.02, 36.44) * mm});
            skLineSegment(sketch, "E1538", {"start": v(52.02, 36.44) * mm, "end": v(52.33, 36.2) * mm});
            skLineSegment(sketch, "E1539", {"start": v(52.33, 36.2) * mm, "end": v(52.7, 36.05) * mm});
            skLineSegment(sketch, "E1540", {"start": v(52.7, 36.05) * mm, "end": v(53.08, 36) * mm});
            skLineSegment(sketch, "E1541", {"start": v(53.08, 36) * mm, "end": v(53.47, 36.05) * mm});
            skLineSegment(sketch, "E1542", {"start": v(53.47, 36.05) * mm, "end": v(53.83, 36.2) * mm});
            skLineSegment(sketch, "E1543", {"start": v(53.83, 36.2) * mm, "end": v(54.14, 36.44) * mm});
            skLineSegment(sketch, "E1544", {"start": v(54.14, 36.44) * mm, "end": v(54.38, 36.75) * mm});
            skLineSegment(sketch, "E1545", {"start": v(54.38, 36.75) * mm, "end": v(54.53, 37.11) * mm});
            skLineSegment(sketch, "E1546", {"start": v(54.53, 37.11) * mm, "end": v(54.58, 37.5) * mm});
            skLineSegment(sketch, "E1547", {"start": v(54.58, 37.5) * mm, "end": v(54.53, 37.89) * mm});
            skLineSegment(sketch, "E1548", {"start": v(54.53, 37.89) * mm, "end": v(54.38, 38.25) * mm});
            skLineSegment(sketch, "E1549", {"start": v(54.38, 38.25) * mm, "end": v(54.14, 38.56) * mm});
            skLineSegment(sketch, "E1550", {"start": v(54.14, 38.56) * mm, "end": v(53.83, 38.8) * mm});
            skLineSegment(sketch, "E1551", {"start": v(53.83, 38.8) * mm, "end": v(53.47, 38.95) * mm});
            skLineSegment(sketch, "E1552", {"start": v(53.47, 38.95) * mm, "end": v(53.08, 39) * mm});
            skLineSegment(sketch, "E1553", {"start": v(53.08, 39) * mm, "end": v(52.7, 38.95) * mm});
            skLineSegment(sketch, "E1554", {"start": v(52.7, 38.95) * mm, "end": v(52.33, 38.8) * mm});
            skLineSegment(sketch, "E1555", {"start": v(52.33, 38.8) * mm, "end": v(52.02, 38.56) * mm});
            skLineSegment(sketch, "E1556", {"start": v(52.02, 38.56) * mm, "end": v(51.78, 38.25) * mm});
            skLineSegment(sketch, "E1557", {"start": v(51.78, 38.25) * mm, "end": v(51.63, 37.89) * mm});
            skLineSegment(sketch, "E1558", {"start": v(73.94, 14.52) * mm, "end": v(74.25, 14.28) * mm});
            skLineSegment(sketch, "E1559", {"start": v(74.25, 14.28) * mm, "end": v(74.61, 14.13) * mm});
            skLineSegment(sketch, "E1560", {"start": v(74.61, 14.13) * mm, "end": v(75, 14.08) * mm});
            skLineSegment(sketch, "E1561", {"start": v(75, 14.08) * mm, "end": v(75.39, 14.13) * mm});
            skLineSegment(sketch, "E1562", {"start": v(75.39, 14.13) * mm, "end": v(75.75, 14.28) * mm});
            skLineSegment(sketch, "E1563", {"start": v(75.75, 14.28) * mm, "end": v(76.06, 14.52) * mm});
            skLineSegment(sketch, "E1564", {"start": v(76.06, 14.52) * mm, "end": v(76.3, 14.83) * mm});
            skLineSegment(sketch, "E1565", {"start": v(76.3, 14.83) * mm, "end": v(76.45, 15.2) * mm});
            skLineSegment(sketch, "E1566", {"start": v(76.45, 15.2) * mm, "end": v(76.5, 15.58) * mm});
            skLineSegment(sketch, "E1567", {"start": v(76.5, 15.58) * mm, "end": v(76.45, 15.97) * mm});
            skLineSegment(sketch, "E1568", {"start": v(76.45, 15.97) * mm, "end": v(76.3, 16.33) * mm});
            skLineSegment(sketch, "E1569", {"start": v(76.3, 16.33) * mm, "end": v(76.06, 16.64) * mm});
            skLineSegment(sketch, "E1570", {"start": v(76.06, 16.64) * mm, "end": v(75.75, 16.88) * mm});
            skLineSegment(sketch, "E1571", {"start": v(75.75, 16.88) * mm, "end": v(75.39, 17.03) * mm});
            skLineSegment(sketch, "E1572", {"start": v(75.39, 17.03) * mm, "end": v(75, 17.08) * mm});
            skLineSegment(sketch, "E1573", {"start": v(75, 17.08) * mm, "end": v(74.61, 17.03) * mm});
            skLineSegment(sketch, "E1574", {"start": v(74.61, 17.03) * mm, "end": v(74.25, 16.88) * mm});
            skLineSegment(sketch, "E1575", {"start": v(74.25, 16.88) * mm, "end": v(73.94, 16.64) * mm});
            skLineSegment(sketch, "E1576", {"start": v(73.94, 16.64) * mm, "end": v(73.7, 16.33) * mm});
            skLineSegment(sketch, "E1577", {"start": v(73.7, 16.33) * mm, "end": v(73.55, 15.97) * mm});
            skLineSegment(sketch, "E1578", {"start": v(73.55, 15.97) * mm, "end": v(73.5, 15.58) * mm});
            skLineSegment(sketch, "E1579", {"start": v(73.5, 15.58) * mm, "end": v(73.55, 15.2) * mm});
            skLineSegment(sketch, "E1580", {"start": v(73.55, 15.2) * mm, "end": v(73.7, 14.83) * mm});
            skLineSegment(sketch, "E1581", {"start": v(73.7, 14.83) * mm, "end": v(73.94, 14.52) * mm});
            skLineSegment(sketch, "E1582", {"start": v(96.53, 38.95) * mm, "end": v(96.17, 38.8) * mm});
            skLineSegment(sketch, "E1583", {"start": v(96.17, 38.8) * mm, "end": v(95.86, 38.56) * mm});
            skLineSegment(sketch, "E1584", {"start": v(95.86, 38.56) * mm, "end": v(95.62, 38.25) * mm});
            skLineSegment(sketch, "E1585", {"start": v(95.62, 38.25) * mm, "end": v(95.47, 37.89) * mm});
            skLineSegment(sketch, "E1586", {"start": v(95.47, 37.89) * mm, "end": v(95.42, 37.5) * mm});
            skLineSegment(sketch, "E1587", {"start": v(95.42, 37.5) * mm, "end": v(95.47, 37.11) * mm});
            skLineSegment(sketch, "E1588", {"start": v(95.47, 37.11) * mm, "end": v(95.62, 36.75) * mm});
            skLineSegment(sketch, "E1589", {"start": v(95.62, 36.75) * mm, "end": v(95.86, 36.44) * mm});
            skLineSegment(sketch, "E1590", {"start": v(95.86, 36.44) * mm, "end": v(96.17, 36.2) * mm});
            skLineSegment(sketch, "E1591", {"start": v(96.17, 36.2) * mm, "end": v(96.53, 36.05) * mm});
            skLineSegment(sketch, "E1592", {"start": v(96.53, 36.05) * mm, "end": v(96.92, 36) * mm});
            skLineSegment(sketch, "E1593", {"start": v(96.92, 36) * mm, "end": v(97.3, 36.05) * mm});
            skLineSegment(sketch, "E1594", {"start": v(97.3, 36.05) * mm, "end": v(97.67, 36.2) * mm});
            skLineSegment(sketch, "E1595", {"start": v(97.67, 36.2) * mm, "end": v(97.98, 36.44) * mm});
            skLineSegment(sketch, "E1596", {"start": v(97.98, 36.44) * mm, "end": v(98.22, 36.75) * mm});
            skLineSegment(sketch, "E1597", {"start": v(98.22, 36.75) * mm, "end": v(98.37, 37.11) * mm});
            skLineSegment(sketch, "E1598", {"start": v(98.37, 37.11) * mm, "end": v(98.42, 37.5) * mm});
            skLineSegment(sketch, "E1599", {"start": v(98.42, 37.5) * mm, "end": v(98.37, 37.89) * mm});
            skLineSegment(sketch, "E1600", {"start": v(98.37, 37.89) * mm, "end": v(98.22, 38.25) * mm});
            skLineSegment(sketch, "E1601", {"start": v(98.22, 38.25) * mm, "end": v(97.98, 38.56) * mm});
            skLineSegment(sketch, "E1602", {"start": v(97.98, 38.56) * mm, "end": v(97.67, 38.8) * mm});
            skLineSegment(sketch, "E1603", {"start": v(97.67, 38.8) * mm, "end": v(97.3, 38.95) * mm});
            skLineSegment(sketch, "E1604", {"start": v(97.3, 38.95) * mm, "end": v(96.92, 39) * mm});
            skLineSegment(sketch, "E1605", {"start": v(96.92, 39) * mm, "end": v(96.53, 38.95) * mm});
            skLineSegment(sketch, "E1606", {"start": v(74.61, 60.87) * mm, "end": v(74.25, 60.72) * mm});
            skLineSegment(sketch, "E1607", {"start": v(74.25, 60.72) * mm, "end": v(73.94, 60.48) * mm});
            skLineSegment(sketch, "E1608", {"start": v(73.94, 60.48) * mm, "end": v(73.7, 60.17) * mm});
            skLineSegment(sketch, "E1609", {"start": v(73.7, 60.17) * mm, "end": v(73.55, 59.8) * mm});
            skLineSegment(sketch, "E1610", {"start": v(73.55, 59.8) * mm, "end": v(73.5, 59.42) * mm});
            skLineSegment(sketch, "E1611", {"start": v(73.5, 59.42) * mm, "end": v(73.55, 59.03) * mm});
            skLineSegment(sketch, "E1612", {"start": v(73.55, 59.03) * mm, "end": v(73.7, 58.67) * mm});
            skLineSegment(sketch, "E1613", {"start": v(73.7, 58.67) * mm, "end": v(73.94, 58.36) * mm});
            skLineSegment(sketch, "E1614", {"start": v(73.94, 58.36) * mm, "end": v(74.25, 58.12) * mm});
            skLineSegment(sketch, "E1615", {"start": v(74.25, 58.12) * mm, "end": v(74.61, 57.97) * mm});
            skLineSegment(sketch, "E1616", {"start": v(74.61, 57.97) * mm, "end": v(75, 57.92) * mm});
            skLineSegment(sketch, "E1617", {"start": v(75, 57.92) * mm, "end": v(75.39, 57.97) * mm});
            skLineSegment(sketch, "E1618", {"start": v(75.39, 57.97) * mm, "end": v(75.75, 58.12) * mm});
            skLineSegment(sketch, "E1619", {"start": v(75.75, 58.12) * mm, "end": v(76.06, 58.36) * mm});
            skLineSegment(sketch, "E1620", {"start": v(76.06, 58.36) * mm, "end": v(76.3, 58.67) * mm});
            skLineSegment(sketch, "E1621", {"start": v(76.3, 58.67) * mm, "end": v(76.45, 59.03) * mm});
            skLineSegment(sketch, "E1622", {"start": v(76.45, 59.03) * mm, "end": v(76.5, 59.42) * mm});
            skLineSegment(sketch, "E1623", {"start": v(76.5, 59.42) * mm, "end": v(76.45, 59.8) * mm});
            skLineSegment(sketch, "E1624", {"start": v(76.45, 59.8) * mm, "end": v(76.3, 60.17) * mm});
            skLineSegment(sketch, "E1625", {"start": v(76.3, 60.17) * mm, "end": v(76.06, 60.48) * mm});
            skLineSegment(sketch, "E1626", {"start": v(76.06, 60.48) * mm, "end": v(75.75, 60.72) * mm});
            skLineSegment(sketch, "E1627", {"start": v(75.75, 60.72) * mm, "end": v(75.39, 60.87) * mm});
            skLineSegment(sketch, "E1628", {"start": v(75.39, 60.87) * mm, "end": v(75, 60.92) * mm});
            skLineSegment(sketch, "E1629", {"start": v(75, 60.92) * mm, "end": v(74.61, 60.87) * mm});
            skLineSegment(sketch, "E1630", {"start": v(127, 40.96) * mm, "end": v(126.04, 41.36) * mm});
            skLineSegment(sketch, "E1631", {"start": v(126.04, 41.36) * mm, "end": v(125, 41.5) * mm});
            skLineSegment(sketch, "E1632", {"start": v(125, 41.5) * mm, "end": v(123.96, 41.36) * mm});
            skLineSegment(sketch, "E1633", {"start": v(123.96, 41.36) * mm, "end": v(123, 40.96) * mm});
            skLineSegment(sketch, "E1634", {"start": v(123, 40.96) * mm, "end": v(122.17, 40.33) * mm});
            skLineSegment(sketch, "E1635", {"start": v(122.17, 40.33) * mm, "end": v(121.54, 39.5) * mm});
            skLineSegment(sketch, "E1636", {"start": v(121.54, 39.5) * mm, "end": v(121.14, 38.54) * mm});
            skLineSegment(sketch, "E1637", {"start": v(121.14, 38.54) * mm, "end": v(121, 37.5) * mm});
            skLineSegment(sketch, "E1638", {"start": v(121, 37.5) * mm, "end": v(121.14, 36.46) * mm});
            skLineSegment(sketch, "E1639", {"start": v(121.14, 36.46) * mm, "end": v(121.54, 35.5) * mm});
            skLineSegment(sketch, "E1640", {"start": v(121.54, 35.5) * mm, "end": v(122.17, 34.67) * mm});
            skLineSegment(sketch, "E1641", {"start": v(122.17, 34.67) * mm, "end": v(123, 34.04) * mm});
            skLineSegment(sketch, "E1642", {"start": v(123, 34.04) * mm, "end": v(123.96, 33.64) * mm});
            skLineSegment(sketch, "E1643", {"start": v(123.96, 33.64) * mm, "end": v(125, 33.5) * mm});
            skLineSegment(sketch, "E1644", {"start": v(125, 33.5) * mm, "end": v(126.04, 33.64) * mm});
            skLineSegment(sketch, "E1645", {"start": v(126.04, 33.64) * mm, "end": v(127, 34.04) * mm});
            skLineSegment(sketch, "E1646", {"start": v(127, 34.04) * mm, "end": v(127.83, 34.67) * mm});
            skLineSegment(sketch, "E1647", {"start": v(127.83, 34.67) * mm, "end": v(128.46, 35.5) * mm});
            skLineSegment(sketch, "E1648", {"start": v(128.46, 35.5) * mm, "end": v(128.86, 36.46) * mm});
            skLineSegment(sketch, "E1649", {"start": v(128.86, 36.46) * mm, "end": v(129, 37.5) * mm});
            skLineSegment(sketch, "E1650", {"start": v(129, 37.5) * mm, "end": v(128.86, 38.54) * mm});
            skLineSegment(sketch, "E1651", {"start": v(128.86, 38.54) * mm, "end": v(128.46, 39.5) * mm});
            skLineSegment(sketch, "E1652", {"start": v(128.46, 39.5) * mm, "end": v(127.83, 40.33) * mm});
            skLineSegment(sketch, "E1653", {"start": v(127.83, 40.33) * mm, "end": v(127, 40.96) * mm});
            skLineSegment(sketch, "E1654", {"start": v(28.86, 38.54) * mm, "end": v(28.46, 39.5) * mm});
            skLineSegment(sketch, "E1655", {"start": v(28.46, 39.5) * mm, "end": v(27.83, 40.33) * mm});
            skLineSegment(sketch, "E1656", {"start": v(27.83, 40.33) * mm, "end": v(27, 40.96) * mm});
            skLineSegment(sketch, "E1657", {"start": v(27, 40.96) * mm, "end": v(26.04, 41.36) * mm});
            skLineSegment(sketch, "E1658", {"start": v(26.04, 41.36) * mm, "end": v(25, 41.5) * mm});
            skLineSegment(sketch, "E1659", {"start": v(25, 41.5) * mm, "end": v(23.96, 41.36) * mm});
            skLineSegment(sketch, "E1660", {"start": v(23.96, 41.36) * mm, "end": v(23, 40.96) * mm});
            skLineSegment(sketch, "E1661", {"start": v(23, 40.96) * mm, "end": v(22.17, 40.33) * mm});
            skLineSegment(sketch, "E1662", {"start": v(22.17, 40.33) * mm, "end": v(21.54, 39.5) * mm});
            skLineSegment(sketch, "E1663", {"start": v(21.54, 39.5) * mm, "end": v(21.14, 38.54) * mm});
            skLineSegment(sketch, "E1664", {"start": v(21.14, 38.54) * mm, "end": v(21, 37.5) * mm});
            skLineSegment(sketch, "E1665", {"start": v(21, 37.5) * mm, "end": v(21.14, 36.46) * mm});
            skLineSegment(sketch, "E1666", {"start": v(21.14, 36.46) * mm, "end": v(21.54, 35.5) * mm});
            skLineSegment(sketch, "E1667", {"start": v(21.54, 35.5) * mm, "end": v(22.17, 34.67) * mm});
            skLineSegment(sketch, "E1668", {"start": v(22.17, 34.67) * mm, "end": v(23, 34.04) * mm});
            skLineSegment(sketch, "E1669", {"start": v(23, 34.04) * mm, "end": v(23.96, 33.64) * mm});
            skLineSegment(sketch, "E1670", {"start": v(23.96, 33.64) * mm, "end": v(25, 33.5) * mm});
            skLineSegment(sketch, "E1671", {"start": v(25, 33.5) * mm, "end": v(26.04, 33.64) * mm});
            skLineSegment(sketch, "E1672", {"start": v(26.04, 33.64) * mm, "end": v(27, 34.04) * mm});
            skLineSegment(sketch, "E1673", {"start": v(27, 34.04) * mm, "end": v(27.83, 34.67) * mm});
            skLineSegment(sketch, "E1674", {"start": v(27.83, 34.67) * mm, "end": v(28.46, 35.5) * mm});
            skLineSegment(sketch, "E1675", {"start": v(28.46, 35.5) * mm, "end": v(28.86, 36.46) * mm});
            skLineSegment(sketch, "E1676", {"start": v(28.86, 36.46) * mm, "end": v(29, 37.5) * mm});
            skLineSegment(sketch, "E1677", {"start": v(29, 37.5) * mm, "end": v(28.86, 38.54) * mm});
            skSolve(sketch);
        }
        {
            var Q0;
            Q0=makeQuery(id+"F12.imprint","IMPRINT",FACE,{"disambiguationData":[TD([[makeQuery(id+"F12.imprint","IMPRINT",EDGE,{"derivedFrom":sQuery(id+"F12.wireOp",EDGE,"E1260")}),-1.0]])]});
            extrude(context, id + "F13", {"entities" : qUnion([Q0]), "depth" : 15 * mm});
        }
        {
            var Q0;
            Q0=makeQuery(id+"F5.opExtrude","SWEPT_BODY",BODY,{"disambiguationData":[OSD([sQuery(id+"F0.wireOp",EDGE,"E0"),sQuery(id+"F0.wireOp",EDGE,"E1"),sQuery(id+"F0.wireOp",EDGE,"E2"),sQuery(id+"F0.wireOp",EDGE,"E3"),sQuery(id+"F0.wireOp",EDGE,"E4"),sQuery(id+"F0.wireOp",EDGE,"E5"),sQuery(id+"F0.wireOp",EDGE,"E6"),sQuery(id+"F0.wireOp",EDGE,"E7"),sQuery(id+"F0.wireOp",EDGE,"E8"),sQuery(id+"F0.wireOp",EDGE,"E9"),sQuery(id+"F0.wireOp",EDGE,"E10"),sQuery(id+"F0.wireOp",EDGE,"E11"),sQuery(id+"F0.wireOp",EDGE,"E12"),sQuery(id+"F0.wireOp",EDGE,"E13"),sQuery(id+"F0.wireOp",EDGE,"E14"),sQuery(id+"F0.wireOp",EDGE,"E15"),sQuery(id+"F0.wireOp",EDGE,"E16"),sQuery(id+"F0.wireOp",EDGE,"E17"),sQuery(id+"F0.wireOp",EDGE,"E18"),sQuery(id+"F0.wireOp",EDGE,"E19"),sQuery(id+"F0.wireOp",EDGE,"E20"),sQuery(id+"F0.wireOp",EDGE,"E21"),sQuery(id+"F0.wireOp",EDGE,"E22"),sQuery(id+"F0.wireOp",EDGE,"E23"),sQuery(id+"F0.wireOp",EDGE,"E24"),sQuery(id+"F0.wireOp",EDGE,"E25"),sQuery(id+"F0.wireOp",EDGE,"E26"),sQuery(id+"F0.wireOp",EDGE,"E27"),sQuery(id+"F0.wireOp",EDGE,"E28"),sQuery(id+"F0.wireOp",EDGE,"E29"),sQuery(id+"F0.wireOp",EDGE,"E30"),sQuery(id+"F0.wireOp",EDGE,"E31"),sQuery(id+"F0.wireOp",EDGE,"E32"),sQuery(id+"F0.wireOp",EDGE,"E33"),sQuery(id+"F0.wireOp",EDGE,"E34"),sQuery(id+"F0.wireOp",EDGE,"E35"),sQuery(id+"F0.wireOp",EDGE,"E36"),sQuery(id+"F0.wireOp",EDGE,"E37"),sQuery(id+"F0.wireOp",EDGE,"E38"),sQuery(id+"F0.wireOp",EDGE,"E39"),sQuery(id+"F0.wireOp",EDGE,"E40"),sQuery(id+"F0.wireOp",EDGE,"E41"),sQuery(id+"F0.wireOp",EDGE,"E42"),sQuery(id+"F0.wireOp",EDGE,"E43"),sQuery(id+"F0.wireOp",EDGE,"E44"),sQuery(id+"F0.wireOp",EDGE,"E45"),sQuery(id+"F0.wireOp",EDGE,"E46"),sQuery(id+"F0.wireOp",EDGE,"E47"),sQuery(id+"F0.wireOp",EDGE,"E48"),sQuery(id+"F0.wireOp",EDGE,"E49"),sQuery(id+"F0.wireOp",EDGE,"E50"),sQuery(id+"F0.wireOp",EDGE,"E51"),sQuery(id+"F0.wireOp",EDGE,"E52"),sQuery(id+"F0.wireOp",EDGE,"E53"),sQuery(id+"F0.wireOp",EDGE,"E54"),sQuery(id+"F0.wireOp",EDGE,"E55"),sQuery(id+"F0.wireOp",EDGE,"E56"),sQuery(id+"F0.wireOp",EDGE,"E57"),sQuery(id+"F0.wireOp",EDGE,"E58"),sQuery(id+"F0.wireOp",EDGE,"E59"),sQuery(id+"F0.wireOp",EDGE,"E60"),sQuery(id+"F0.wireOp",EDGE,"E61"),sQuery(id+"F0.wireOp",EDGE,"E62"),sQuery(id+"F0.wireOp",EDGE,"E63"),sQuery(id+"F0.wireOp",EDGE,"E64"),sQuery(id+"F0.wireOp",EDGE,"E65"),sQuery(id+"F0.wireOp",EDGE,"E66"),sQuery(id+"F0.wireOp",EDGE,"E67"),sQuery(id+"F0.wireOp",EDGE,"E68"),sQuery(id+"F0.wireOp",EDGE,"E69"),sQuery(id+"F0.wireOp",EDGE,"E70"),sQuery(id+"F0.wireOp",EDGE,"E71"),sQuery(id+"F0.wireOp",EDGE,"E72"),sQuery(id+"F0.wireOp",EDGE,"E73"),sQuery(id+"F0.wireOp",EDGE,"E74"),sQuery(id+"F0.wireOp",EDGE,"E75"),sQuery(id+"F0.wireOp",EDGE,"E76"),sQuery(id+"F0.wireOp",EDGE,"E77"),sQuery(id+"F0.wireOp",EDGE,"E78"),sQuery(id+"F0.wireOp",EDGE,"E79"),sQuery(id+"F0.wireOp",EDGE,"E80"),sQuery(id+"F0.wireOp",EDGE,"E81"),sQuery(id+"F0.wireOp",EDGE,"E82"),sQuery(id+"F0.wireOp",EDGE,"E83"),sQuery(id+"F0.wireOp",EDGE,"E84"),sQuery(id+"F0.wireOp",EDGE,"E85"),sQuery(id+"F0.wireOp",EDGE,"E86"),sQuery(id+"F0.wireOp",EDGE,"E87"),sQuery(id+"F0.wireOp",EDGE,"E88"),sQuery(id+"F0.wireOp",EDGE,"E89"),sQuery(id+"F0.wireOp",EDGE,"E90"),sQuery(id+"F0.wireOp",EDGE,"E91"),sQuery(id+"F0.wireOp",EDGE,"E92"),sQuery(id+"F0.wireOp",EDGE,"E93"),sQuery(id+"F0.wireOp",EDGE,"E94"),sQuery(id+"F0.wireOp",EDGE,"E95"),sQuery(id+"F0.wireOp",EDGE,"E96"),sQuery(id+"F0.wireOp",EDGE,"E97"),sQuery(id+"F0.wireOp",EDGE,"E98"),sQuery(id+"F0.wireOp",EDGE,"E99"),sQuery(id+"F0.wireOp",EDGE,"E100"),sQuery(id+"F0.wireOp",EDGE,"E101"),sQuery(id+"F0.wireOp",EDGE,"E102"),sQuery(id+"F0.wireOp",EDGE,"E103"),sQuery(id+"F0.wireOp",EDGE,"E104"),sQuery(id+"F0.wireOp",EDGE,"E105"),sQuery(id+"F0.wireOp",EDGE,"E106"),sQuery(id+"F0.wireOp",EDGE,"E107"),sQuery(id+"F0.wireOp",EDGE,"E108"),sQuery(id+"F0.wireOp",EDGE,"E109"),sQuery(id+"F0.wireOp",EDGE,"E110"),sQuery(id+"F0.wireOp",EDGE,"E111"),sQuery(id+"F0.wireOp",EDGE,"E112"),sQuery(id+"F0.wireOp",EDGE,"E113"),sQuery(id+"F0.wireOp",EDGE,"E114"),sQuery(id+"F0.wireOp",EDGE,"E115"),sQuery(id+"F0.wireOp",EDGE,"E116"),sQuery(id+"F0.wireOp",EDGE,"E117"),sQuery(id+"F0.wireOp",EDGE,"E118"),sQuery(id+"F0.wireOp",EDGE,"E119"),sQuery(id+"F0.wireOp",EDGE,"E120"),sQuery(id+"F0.wireOp",EDGE,"E121"),sQuery(id+"F0.wireOp",EDGE,"E122"),sQuery(id+"F0.wireOp",EDGE,"E123"),sQuery(id+"F0.wireOp",EDGE,"E124"),sQuery(id+"F0.wireOp",EDGE,"E125"),sQuery(id+"F0.wireOp",EDGE,"E126"),sQuery(id+"F0.wireOp",EDGE,"E127"),sQuery(id+"F0.wireOp",EDGE,"E128"),sQuery(id+"F0.wireOp",EDGE,"E129"),sQuery(id+"F0.wireOp",EDGE,"E130"),sQuery(id+"F0.wireOp",EDGE,"E131"),sQuery(id+"F0.wireOp",EDGE,"E132"),sQuery(id+"F0.wireOp",EDGE,"E133"),sQuery(id+"F0.wireOp",EDGE,"E134"),sQuery(id+"F0.wireOp",EDGE,"E135"),sQuery(id+"F0.wireOp",EDGE,"E136"),sQuery(id+"F0.wireOp",EDGE,"E137"),sQuery(id+"F0.wireOp",EDGE,"E138"),sQuery(id+"F0.wireOp",EDGE,"E139"),sQuery(id+"F0.wireOp",EDGE,"E140"),sQuery(id+"F0.wireOp",EDGE,"E141"),sQuery(id+"F0.wireOp",EDGE,"E142"),sQuery(id+"F0.wireOp",EDGE,"E143"),sQuery(id+"F0.wireOp",EDGE,"E144"),sQuery(id+"F0.wireOp",EDGE,"E145"),sQuery(id+"F0.wireOp",EDGE,"E146"),sQuery(id+"F0.wireOp",EDGE,"E147"),sQuery(id+"F0.wireOp",EDGE,"E148"),sQuery(id+"F0.wireOp",EDGE,"E149"),sQuery(id+"F0.wireOp",EDGE,"E150"),sQuery(id+"F0.wireOp",EDGE,"E151"),sQuery(id+"F0.wireOp",EDGE,"E152"),sQuery(id+"F0.wireOp",EDGE,"E153"),sQuery(id+"F0.wireOp",EDGE,"E154"),sQuery(id+"F0.wireOp",EDGE,"E155"),sQuery(id+"F0.wireOp",EDGE,"E156"),sQuery(id+"F0.wireOp",EDGE,"E157"),sQuery(id+"F0.wireOp",EDGE,"E158"),sQuery(id+"F0.wireOp",EDGE,"E159"),sQuery(id+"F0.wireOp",EDGE,"E160"),sQuery(id+"F0.wireOp",EDGE,"E161"),sQuery(id+"F0.wireOp",EDGE,"E162"),sQuery(id+"F0.wireOp",EDGE,"E163"),sQuery(id+"F0.wireOp",EDGE,"E164"),sQuery(id+"F0.wireOp",EDGE,"E165"),sQuery(id+"F0.wireOp",EDGE,"E166"),sQuery(id+"F0.wireOp",EDGE,"E167"),sQuery(id+"F0.wireOp",EDGE,"E168"),sQuery(id+"F0.wireOp",EDGE,"E169"),sQuery(id+"F0.wireOp",EDGE,"E170"),sQuery(id+"F0.wireOp",EDGE,"E171"),sQuery(id+"F0.wireOp",EDGE,"E172"),sQuery(id+"F0.wireOp",EDGE,"E173"),sQuery(id+"F0.wireOp",EDGE,"E174"),sQuery(id+"F0.wireOp",EDGE,"E175"),sQuery(id+"F0.wireOp",EDGE,"E176"),sQuery(id+"F0.wireOp",EDGE,"E177"),sQuery(id+"F0.wireOp",EDGE,"E178"),sQuery(id+"F0.wireOp",EDGE,"E179"),sQuery(id+"F0.wireOp",EDGE,"E180"),sQuery(id+"F0.wireOp",EDGE,"E181"),sQuery(id+"F0.wireOp",EDGE,"E182"),sQuery(id+"F0.wireOp",EDGE,"E183"),sQuery(id+"F0.wireOp",EDGE,"E184"),sQuery(id+"F0.wireOp",EDGE,"E185"),sQuery(id+"F0.wireOp",EDGE,"E186"),sQuery(id+"F0.wireOp",EDGE,"E187"),sQuery(id+"F0.wireOp",EDGE,"E188"),sQuery(id+"F0.wireOp",EDGE,"E189"),sQuery(id+"F0.wireOp",EDGE,"E190"),sQuery(id+"F0.wireOp",EDGE,"E191"),sQuery(id+"F0.wireOp",EDGE,"E192"),sQuery(id+"F0.wireOp",EDGE,"E193"),sQuery(id+"F0.wireOp",EDGE,"E194"),sQuery(id+"F0.wireOp",EDGE,"E195"),sQuery(id+"F0.wireOp",EDGE,"E196"),sQuery(id+"F0.wireOp",EDGE,"E197"),sQuery(id+"F0.wireOp",EDGE,"E198"),sQuery(id+"F0.wireOp",EDGE,"E199"),sQuery(id+"F0.wireOp",EDGE,"E200"),sQuery(id+"F0.wireOp",EDGE,"E201"),sQuery(id+"F0.wireOp",EDGE,"E202"),sQuery(id+"F0.wireOp",EDGE,"E203"),sQuery(id+"F0.wireOp",EDGE,"E204"),sQuery(id+"F0.wireOp",EDGE,"E205"),sQuery(id+"F0.wireOp",EDGE,"E206"),sQuery(id+"F0.wireOp",EDGE,"E207"),sQuery(id+"F0.wireOp",EDGE,"E208"),sQuery(id+"F0.wireOp",EDGE,"E209"),sQuery(id+"F0.wireOp",EDGE,"E210"),sQuery(id+"F0.wireOp",EDGE,"E211"),sQuery(id+"F0.wireOp",EDGE,"E212"),sQuery(id+"F0.wireOp",EDGE,"E213"),sQuery(id+"F0.wireOp",EDGE,"E214"),sQuery(id+"F0.wireOp",EDGE,"E215"),sQuery(id+"F0.wireOp",EDGE,"E216"),sQuery(id+"F0.wireOp",EDGE,"E217"),sQuery(id+"F0.wireOp",EDGE,"E218"),sQuery(id+"F0.wireOp",EDGE,"E219"),sQuery(id+"F0.wireOp",EDGE,"E220"),sQuery(id+"F0.wireOp",EDGE,"E221"),sQuery(id+"F0.wireOp",EDGE,"E222"),sQuery(id+"F0.wireOp",EDGE,"E223"),sQuery(id+"F0.wireOp",EDGE,"E224"),sQuery(id+"F0.wireOp",EDGE,"E225"),sQuery(id+"F0.wireOp",EDGE,"E226"),sQuery(id+"F0.wireOp",EDGE,"E227"),sQuery(id+"F0.wireOp",EDGE,"E228"),sQuery(id+"F0.wireOp",EDGE,"E229"),sQuery(id+"F0.wireOp",EDGE,"E230"),sQuery(id+"F0.wireOp",EDGE,"E231"),sQuery(id+"F0.wireOp",EDGE,"E232"),sQuery(id+"F0.wireOp",EDGE,"E233"),sQuery(id+"F0.wireOp",EDGE,"E234"),sQuery(id+"F0.wireOp",EDGE,"E235"),sQuery(id+"F0.wireOp",EDGE,"E236"),sQuery(id+"F0.wireOp",EDGE,"E237"),sQuery(id+"F0.wireOp",EDGE,"E238"),sQuery(id+"F0.wireOp",EDGE,"E239"),sQuery(id+"F0.wireOp",EDGE,"E240"),sQuery(id+"F0.wireOp",EDGE,"E241"),sQuery(id+"F0.wireOp",EDGE,"E242"),sQuery(id+"F0.wireOp",EDGE,"E243"),sQuery(id+"F0.wireOp",EDGE,"E244"),sQuery(id+"F0.wireOp",EDGE,"E245"),sQuery(id+"F0.wireOp",EDGE,"E246"),sQuery(id+"F0.wireOp",EDGE,"E247"),sQuery(id+"F0.wireOp",EDGE,"E248"),sQuery(id+"F0.wireOp",EDGE,"E249"),sQuery(id+"F0.wireOp",EDGE,"E250"),sQuery(id+"F0.wireOp",EDGE,"E251"),sQuery(id+"F0.wireOp",EDGE,"E252"),sQuery(id+"F0.wireOp",EDGE,"E253"),sQuery(id+"F0.wireOp",EDGE,"E254"),sQuery(id+"F0.wireOp",EDGE,"E255"),sQuery(id+"F0.wireOp",EDGE,"E256"),sQuery(id+"F0.wireOp",EDGE,"E257"),sQuery(id+"F0.wireOp",EDGE,"E258"),sQuery(id+"F0.wireOp",EDGE,"E259"),sQuery(id+"F0.wireOp",EDGE,"E260"),sQuery(id+"F0.wireOp",EDGE,"E261"),sQuery(id+"F0.wireOp",EDGE,"E262"),sQuery(id+"F0.wireOp",EDGE,"E263"),sQuery(id+"F0.wireOp",EDGE,"E264"),sQuery(id+"F0.wireOp",EDGE,"E265"),sQuery(id+"F0.wireOp",EDGE,"E266"),sQuery(id+"F0.wireOp",EDGE,"E267"),sQuery(id+"F0.wireOp",EDGE,"E268"),sQuery(id+"F0.wireOp",EDGE,"E269"),sQuery(id+"F0.wireOp",EDGE,"E270"),sQuery(id+"F0.wireOp",EDGE,"E271"),sQuery(id+"F0.wireOp",EDGE,"E272"),sQuery(id+"F0.wireOp",EDGE,"E273"),sQuery(id+"F0.wireOp",EDGE,"E274"),sQuery(id+"F0.wireOp",EDGE,"E275"),sQuery(id+"F0.wireOp",EDGE,"E276"),sQuery(id+"F0.wireOp",EDGE,"E277"),sQuery(id+"F0.wireOp",EDGE,"E278"),sQuery(id+"F0.wireOp",EDGE,"E279"),sQuery(id+"F0.wireOp",EDGE,"E280"),sQuery(id+"F0.wireOp",EDGE,"E281"),sQuery(id+"F0.wireOp",EDGE,"E282"),sQuery(id+"F0.wireOp",EDGE,"E283"),sQuery(id+"F0.wireOp",EDGE,"E284"),sQuery(id+"F0.wireOp",EDGE,"E285"),sQuery(id+"F0.wireOp",EDGE,"E286"),sQuery(id+"F0.wireOp",EDGE,"E287"),sQuery(id+"F0.wireOp",EDGE,"E288"),sQuery(id+"F0.wireOp",EDGE,"E289"),sQuery(id+"F0.wireOp",EDGE,"E290"),sQuery(id+"F0.wireOp",EDGE,"E291"),sQuery(id+"F0.wireOp",EDGE,"E292"),sQuery(id+"F0.wireOp",EDGE,"E293"),sQuery(id+"F0.wireOp",EDGE,"E294"),sQuery(id+"F0.wireOp",EDGE,"E295"),sQuery(id+"F0.wireOp",EDGE,"E296"),sQuery(id+"F0.wireOp",EDGE,"E297"),sQuery(id+"F0.wireOp",EDGE,"E298"),sQuery(id+"F0.wireOp",EDGE,"E299"),sQuery(id+"F0.wireOp",EDGE,"E300"),sQuery(id+"F0.wireOp",EDGE,"E301"),sQuery(id+"F0.wireOp",EDGE,"E302"),sQuery(id+"F0.wireOp",EDGE,"E303"),sQuery(id+"F0.wireOp",EDGE,"E304"),sQuery(id+"F0.wireOp",EDGE,"E305"),sQuery(id+"F0.wireOp",EDGE,"E306"),sQuery(id+"F0.wireOp",EDGE,"E307"),sQuery(id+"F0.wireOp",EDGE,"E308"),sQuery(id+"F0.wireOp",EDGE,"E309"),sQuery(id+"F0.wireOp",EDGE,"E310"),sQuery(id+"F0.wireOp",EDGE,"E311"),sQuery(id+"F0.wireOp",EDGE,"E312"),sQuery(id+"F0.wireOp",EDGE,"E313"),sQuery(id+"F0.wireOp",EDGE,"E314"),sQuery(id+"F0.wireOp",EDGE,"E315"),sQuery(id+"F0.wireOp",EDGE,"E316"),sQuery(id+"F0.wireOp",EDGE,"E317"),sQuery(id+"F0.wireOp",EDGE,"E318"),sQuery(id+"F0.wireOp",EDGE,"E319"),sQuery(id+"F0.wireOp",EDGE,"E320"),sQuery(id+"F0.wireOp",EDGE,"E321"),sQuery(id+"F0.wireOp",EDGE,"E322"),sQuery(id+"F0.wireOp",EDGE,"E323"),sQuery(id+"F0.wireOp",EDGE,"E324"),sQuery(id+"F0.wireOp",EDGE,"E325"),sQuery(id+"F0.wireOp",EDGE,"E326"),sQuery(id+"F0.wireOp",EDGE,"E327"),sQuery(id+"F0.wireOp",EDGE,"E328"),sQuery(id+"F0.wireOp",EDGE,"E329"),sQuery(id+"F0.wireOp",EDGE,"E330"),sQuery(id+"F0.wireOp",EDGE,"E331"),sQuery(id+"F0.wireOp",EDGE,"E332"),sQuery(id+"F0.wireOp",EDGE,"E333"),sQuery(id+"F0.wireOp",EDGE,"E334"),sQuery(id+"F0.wireOp",EDGE,"E335"),sQuery(id+"F0.wireOp",EDGE,"E336"),sQuery(id+"F0.wireOp",EDGE,"E337"),sQuery(id+"F0.wireOp",EDGE,"E338"),sQuery(id+"F0.wireOp",EDGE,"E339"),sQuery(id+"F0.wireOp",EDGE,"E340"),sQuery(id+"F0.wireOp",EDGE,"E341"),sQuery(id+"F0.wireOp",EDGE,"E342"),sQuery(id+"F0.wireOp",EDGE,"E343"),sQuery(id+"F0.wireOp",EDGE,"E344"),sQuery(id+"F0.wireOp",EDGE,"E345"),sQuery(id+"F0.wireOp",EDGE,"E346"),sQuery(id+"F0.wireOp",EDGE,"E347"),sQuery(id+"F0.wireOp",EDGE,"E348"),sQuery(id+"F0.wireOp",EDGE,"E349"),sQuery(id+"F0.wireOp",EDGE,"E350"),sQuery(id+"F0.wireOp",EDGE,"E351"),sQuery(id+"F0.wireOp",EDGE,"E352"),sQuery(id+"F0.wireOp",EDGE,"E353"),sQuery(id+"F0.wireOp",EDGE,"E354"),sQuery(id+"F0.wireOp",EDGE,"E355"),sQuery(id+"F0.wireOp",EDGE,"E356"),sQuery(id+"F0.wireOp",EDGE,"E357"),sQuery(id+"F0.wireOp",EDGE,"E358"),sQuery(id+"F0.wireOp",EDGE,"E359"),sQuery(id+"F0.wireOp",EDGE,"E360"),sQuery(id+"F0.wireOp",EDGE,"E361"),sQuery(id+"F0.wireOp",EDGE,"E362"),sQuery(id+"F0.wireOp",EDGE,"E363"),sQuery(id+"F0.wireOp",EDGE,"E364"),sQuery(id+"F0.wireOp",EDGE,"E365"),sQuery(id+"F0.wireOp",EDGE,"E366"),sQuery(id+"F0.wireOp",EDGE,"E367"),sQuery(id+"F0.wireOp",EDGE,"E368"),sQuery(id+"F0.wireOp",EDGE,"E369"),sQuery(id+"F0.wireOp",EDGE,"E370"),sQuery(id+"F0.wireOp",EDGE,"E371"),sQuery(id+"F0.wireOp",EDGE,"E372"),sQuery(id+"F0.wireOp",EDGE,"E373"),sQuery(id+"F0.wireOp",EDGE,"E374"),sQuery(id+"F0.wireOp",EDGE,"E375"),sQuery(id+"F0.wireOp",EDGE,"E376"),sQuery(id+"F0.wireOp",EDGE,"E377"),sQuery(id+"F0.wireOp",EDGE,"E378"),sQuery(id+"F0.wireOp",EDGE,"E379"),sQuery(id+"F0.wireOp",EDGE,"E380"),sQuery(id+"F0.wireOp",EDGE,"E381"),sQuery(id+"F0.wireOp",EDGE,"E382"),sQuery(id+"F0.wireOp",EDGE,"E383"),sQuery(id+"F0.wireOp",EDGE,"E384"),sQuery(id+"F0.wireOp",EDGE,"E385"),sQuery(id+"F0.wireOp",EDGE,"E386"),sQuery(id+"F0.wireOp",EDGE,"E387"),sQuery(id+"F0.wireOp",EDGE,"E388"),sQuery(id+"F0.wireOp",EDGE,"E389"),sQuery(id+"F0.wireOp",EDGE,"E390"),sQuery(id+"F0.wireOp",EDGE,"E391"),sQuery(id+"F0.wireOp",EDGE,"E392"),sQuery(id+"F0.wireOp",EDGE,"E393"),sQuery(id+"F0.wireOp",EDGE,"E394"),sQuery(id+"F0.wireOp",EDGE,"E395"),sQuery(id+"F0.wireOp",EDGE,"E396"),sQuery(id+"F0.wireOp",EDGE,"E397"),sQuery(id+"F0.wireOp",EDGE,"E398"),sQuery(id+"F0.wireOp",EDGE,"E399"),sQuery(id+"F0.wireOp",EDGE,"E400"),sQuery(id+"F0.wireOp",EDGE,"E401"),sQuery(id+"F0.wireOp",EDGE,"E402"),sQuery(id+"F0.wireOp",EDGE,"E403"),sQuery(id+"F0.wireOp",EDGE,"E404"),sQuery(id+"F0.wireOp",EDGE,"E405"),sQuery(id+"F0.wireOp",EDGE,"E406"),sQuery(id+"F0.wireOp",EDGE,"E407"),sQuery(id+"F0.wireOp",EDGE,"E408"),sQuery(id+"F0.wireOp",EDGE,"E409"),sQuery(id+"F0.wireOp",EDGE,"E410"),sQuery(id+"F0.wireOp",EDGE,"E411"),sQuery(id+"F0.wireOp",EDGE,"E412"),sQuery(id+"F0.wireOp",EDGE,"E413"),sQuery(id+"F0.wireOp",EDGE,"E414"),sQuery(id+"F0.wireOp",EDGE,"E415"),sQuery(id+"F0.wireOp",EDGE,"E416"),sQuery(id+"F0.wireOp",EDGE,"E417"),sQuery(id+"F0.wireOp",EDGE,"E418")])]});
            deleteBodies(context, id + "F14", {"entities" : qUnion([Q0])});
        }
        {
            var Q0;
            Q0=makeQuery(id+"F5.opExtrude","SWEPT_BODY",BODY,{"disambiguationData":[OSD([sQuery(id+"F4.wireOp",EDGE,"E576"),sQuery(id+"F4.wireOp",EDGE,"E577"),sQuery(id+"F4.wireOp",EDGE,"E578"),sQuery(id+"F4.wireOp",EDGE,"E579"),sQuery(id+"F4.wireOp",EDGE,"E580"),sQuery(id+"F4.wireOp",EDGE,"E581"),sQuery(id+"F4.wireOp",EDGE,"E582"),sQuery(id+"F4.wireOp",EDGE,"E583"),sQuery(id+"F4.wireOp",EDGE,"E584"),sQuery(id+"F4.wireOp",EDGE,"E585"),sQuery(id+"F4.wireOp",EDGE,"E586"),sQuery(id+"F4.wireOp",EDGE,"E587"),sQuery(id+"F4.wireOp",EDGE,"E588"),sQuery(id+"F4.wireOp",EDGE,"E589"),sQuery(id+"F4.wireOp",EDGE,"E590"),sQuery(id+"F4.wireOp",EDGE,"E591"),sQuery(id+"F4.wireOp",EDGE,"E592"),sQuery(id+"F4.wireOp",EDGE,"E593"),sQuery(id+"F4.wireOp",EDGE,"E594"),sQuery(id+"F4.wireOp",EDGE,"E595"),sQuery(id+"F4.wireOp",EDGE,"E596"),sQuery(id+"F4.wireOp",EDGE,"E597"),sQuery(id+"F4.wireOp",EDGE,"E598"),sQuery(id+"F4.wireOp",EDGE,"E599"),sQuery(id+"F4.wireOp",EDGE,"E600"),sQuery(id+"F4.wireOp",EDGE,"E601"),sQuery(id+"F4.wireOp",EDGE,"E602"),sQuery(id+"F4.wireOp",EDGE,"E603"),sQuery(id+"F4.wireOp",EDGE,"E604"),sQuery(id+"F4.wireOp",EDGE,"E605"),sQuery(id+"F4.wireOp",EDGE,"E606"),sQuery(id+"F4.wireOp",EDGE,"E607"),sQuery(id+"F4.wireOp",EDGE,"E608"),sQuery(id+"F4.wireOp",EDGE,"E609"),sQuery(id+"F4.wireOp",EDGE,"E610"),sQuery(id+"F4.wireOp",EDGE,"E611"),sQuery(id+"F4.wireOp",EDGE,"E612"),sQuery(id+"F4.wireOp",EDGE,"E613"),sQuery(id+"F4.wireOp",EDGE,"E614"),sQuery(id+"F4.wireOp",EDGE,"E615"),sQuery(id+"F4.wireOp",EDGE,"E616"),sQuery(id+"F4.wireOp",EDGE,"E617"),sQuery(id+"F4.wireOp",EDGE,"E618"),sQuery(id+"F4.wireOp",EDGE,"E619"),sQuery(id+"F4.wireOp",EDGE,"E620"),sQuery(id+"F4.wireOp",EDGE,"E621"),sQuery(id+"F4.wireOp",EDGE,"E622"),sQuery(id+"F4.wireOp",EDGE,"E623"),sQuery(id+"F4.wireOp",EDGE,"E624"),sQuery(id+"F4.wireOp",EDGE,"E625"),sQuery(id+"F4.wireOp",EDGE,"E626"),sQuery(id+"F4.wireOp",EDGE,"E627"),sQuery(id+"F4.wireOp",EDGE,"E628"),sQuery(id+"F4.wireOp",EDGE,"E629"),sQuery(id+"F4.wireOp",EDGE,"E630"),sQuery(id+"F4.wireOp",EDGE,"E631"),sQuery(id+"F4.wireOp",EDGE,"E632"),sQuery(id+"F4.wireOp",EDGE,"E633"),sQuery(id+"F4.wireOp",EDGE,"E634"),sQuery(id+"F4.wireOp",EDGE,"E635"),sQuery(id+"F4.wireOp",EDGE,"E636"),sQuery(id+"F4.wireOp",EDGE,"E637"),sQuery(id+"F4.wireOp",EDGE,"E638"),sQuery(id+"F4.wireOp",EDGE,"E639"),sQuery(id+"F4.wireOp",EDGE,"E640"),sQuery(id+"F4.wireOp",EDGE,"E641"),sQuery(id+"F4.wireOp",EDGE,"E642"),sQuery(id+"F4.wireOp",EDGE,"E643"),sQuery(id+"F4.wireOp",EDGE,"E644"),sQuery(id+"F4.wireOp",EDGE,"E645"),sQuery(id+"F4.wireOp",EDGE,"E646"),sQuery(id+"F4.wireOp",EDGE,"E647"),sQuery(id+"F4.wireOp",EDGE,"E648"),sQuery(id+"F4.wireOp",EDGE,"E649"),sQuery(id+"F4.wireOp",EDGE,"E650"),sQuery(id+"F4.wireOp",EDGE,"E651"),sQuery(id+"F4.wireOp",EDGE,"E652"),sQuery(id+"F4.wireOp",EDGE,"E653"),sQuery(id+"F4.wireOp",EDGE,"E654"),sQuery(id+"F4.wireOp",EDGE,"E655"),sQuery(id+"F4.wireOp",EDGE,"E656"),sQuery(id+"F4.wireOp",EDGE,"E657"),sQuery(id+"F4.wireOp",EDGE,"E658"),sQuery(id+"F4.wireOp",EDGE,"E659"),sQuery(id+"F4.wireOp",EDGE,"E660"),sQuery(id+"F4.wireOp",EDGE,"E661"),sQuery(id+"F4.wireOp",EDGE,"E662"),sQuery(id+"F4.wireOp",EDGE,"E663"),sQuery(id+"F4.wireOp",EDGE,"E664"),sQuery(id+"F4.wireOp",EDGE,"E665"),sQuery(id+"F4.wireOp",EDGE,"E666"),sQuery(id+"F4.wireOp",EDGE,"E667"),sQuery(id+"F4.wireOp",EDGE,"E668"),sQuery(id+"F4.wireOp",EDGE,"E669"),sQuery(id+"F4.wireOp",EDGE,"E670"),sQuery(id+"F4.wireOp",EDGE,"E671"),sQuery(id+"F4.wireOp",EDGE,"E672"),sQuery(id+"F4.wireOp",EDGE,"E673"),sQuery(id+"F4.wireOp",EDGE,"E674"),sQuery(id+"F4.wireOp",EDGE,"E675"),sQuery(id+"F4.wireOp",EDGE,"E676"),sQuery(id+"F4.wireOp",EDGE,"E677"),sQuery(id+"F4.wireOp",EDGE,"E678"),sQuery(id+"F4.wireOp",EDGE,"E679"),sQuery(id+"F4.wireOp",EDGE,"E680"),sQuery(id+"F4.wireOp",EDGE,"E681"),sQuery(id+"F4.wireOp",EDGE,"E682"),sQuery(id+"F4.wireOp",EDGE,"E683"),sQuery(id+"F4.wireOp",EDGE,"E684"),sQuery(id+"F4.wireOp",EDGE,"E685"),sQuery(id+"F4.wireOp",EDGE,"E686"),sQuery(id+"F4.wireOp",EDGE,"E687"),sQuery(id+"F4.wireOp",EDGE,"E688"),sQuery(id+"F4.wireOp",EDGE,"E689"),sQuery(id+"F4.wireOp",EDGE,"E690"),sQuery(id+"F4.wireOp",EDGE,"E691"),sQuery(id+"F4.wireOp",EDGE,"E692"),sQuery(id+"F4.wireOp",EDGE,"E693"),sQuery(id+"F4.wireOp",EDGE,"E694"),sQuery(id+"F4.wireOp",EDGE,"E695"),sQuery(id+"F4.wireOp",EDGE,"E696"),sQuery(id+"F4.wireOp",EDGE,"E697"),sQuery(id+"F4.wireOp",EDGE,"E698"),sQuery(id+"F4.wireOp",EDGE,"E699"),sQuery(id+"F4.wireOp",EDGE,"E700"),sQuery(id+"F4.wireOp",EDGE,"E701"),sQuery(id+"F4.wireOp",EDGE,"E702"),sQuery(id+"F4.wireOp",EDGE,"E703"),sQuery(id+"F4.wireOp",EDGE,"E704"),sQuery(id+"F4.wireOp",EDGE,"E705"),sQuery(id+"F4.wireOp",EDGE,"E706"),sQuery(id+"F4.wireOp",EDGE,"E707"),sQuery(id+"F4.wireOp",EDGE,"E708"),sQuery(id+"F4.wireOp",EDGE,"E709"),sQuery(id+"F4.wireOp",EDGE,"E710"),sQuery(id+"F4.wireOp",EDGE,"E711"),sQuery(id+"F4.wireOp",EDGE,"E712"),sQuery(id+"F4.wireOp",EDGE,"E713"),sQuery(id+"F4.wireOp",EDGE,"E714"),sQuery(id+"F4.wireOp",EDGE,"E715"),sQuery(id+"F4.wireOp",EDGE,"E716"),sQuery(id+"F4.wireOp",EDGE,"E717"),sQuery(id+"F4.wireOp",EDGE,"E718"),sQuery(id+"F4.wireOp",EDGE,"E719"),sQuery(id+"F4.wireOp",EDGE,"E720"),sQuery(id+"F4.wireOp",EDGE,"E721"),sQuery(id+"F4.wireOp",EDGE,"E722"),sQuery(id+"F4.wireOp",EDGE,"E723"),sQuery(id+"F4.wireOp",EDGE,"E724"),sQuery(id+"F4.wireOp",EDGE,"E725"),sQuery(id+"F4.wireOp",EDGE,"E726"),sQuery(id+"F4.wireOp",EDGE,"E727"),sQuery(id+"F4.wireOp",EDGE,"E728"),sQuery(id+"F4.wireOp",EDGE,"E729"),sQuery(id+"F4.wireOp",EDGE,"E730"),sQuery(id+"F4.wireOp",EDGE,"E731"),sQuery(id+"F4.wireOp",EDGE,"E732"),sQuery(id+"F4.wireOp",EDGE,"E733"),sQuery(id+"F4.wireOp",EDGE,"E734"),sQuery(id+"F4.wireOp",EDGE,"E735"),sQuery(id+"F4.wireOp",EDGE,"E736"),sQuery(id+"F4.wireOp",EDGE,"E737"),sQuery(id+"F4.wireOp",EDGE,"E738"),sQuery(id+"F4.wireOp",EDGE,"E739"),sQuery(id+"F4.wireOp",EDGE,"E740"),sQuery(id+"F4.wireOp",EDGE,"E741"),sQuery(id+"F4.wireOp",EDGE,"E742"),sQuery(id+"F4.wireOp",EDGE,"E743"),sQuery(id+"F4.wireOp",EDGE,"E744"),sQuery(id+"F4.wireOp",EDGE,"E745"),sQuery(id+"F4.wireOp",EDGE,"E746"),sQuery(id+"F4.wireOp",EDGE,"E747"),sQuery(id+"F4.wireOp",EDGE,"E748"),sQuery(id+"F4.wireOp",EDGE,"E749"),sQuery(id+"F4.wireOp",EDGE,"E750"),sQuery(id+"F4.wireOp",EDGE,"E751"),sQuery(id+"F4.wireOp",EDGE,"E752"),sQuery(id+"F4.wireOp",EDGE,"E753"),sQuery(id+"F4.wireOp",EDGE,"E754"),sQuery(id+"F4.wireOp",EDGE,"E755"),sQuery(id+"F4.wireOp",EDGE,"E756"),sQuery(id+"F4.wireOp",EDGE,"E757"),sQuery(id+"F4.wireOp",EDGE,"E758"),sQuery(id+"F4.wireOp",EDGE,"E759"),sQuery(id+"F4.wireOp",EDGE,"E760"),sQuery(id+"F4.wireOp",EDGE,"E761"),sQuery(id+"F4.wireOp",EDGE,"E762"),sQuery(id+"F4.wireOp",EDGE,"E763"),sQuery(id+"F4.wireOp",EDGE,"E764"),sQuery(id+"F4.wireOp",EDGE,"E765"),sQuery(id+"F4.wireOp",EDGE,"E766"),sQuery(id+"F4.wireOp",EDGE,"E767"),sQuery(id+"F4.wireOp",EDGE,"E768"),sQuery(id+"F4.wireOp",EDGE,"E769"),sQuery(id+"F4.wireOp",EDGE,"E770"),sQuery(id+"F4.wireOp",EDGE,"E771"),sQuery(id+"F4.wireOp",EDGE,"E772"),sQuery(id+"F4.wireOp",EDGE,"E773"),sQuery(id+"F4.wireOp",EDGE,"E774"),sQuery(id+"F4.wireOp",EDGE,"E775"),sQuery(id+"F4.wireOp",EDGE,"E776"),sQuery(id+"F4.wireOp",EDGE,"E777"),sQuery(id+"F4.wireOp",EDGE,"E778"),sQuery(id+"F4.wireOp",EDGE,"E779"),sQuery(id+"F4.wireOp",EDGE,"E780"),sQuery(id+"F4.wireOp",EDGE,"E781"),sQuery(id+"F4.wireOp",EDGE,"E782"),sQuery(id+"F4.wireOp",EDGE,"E783"),sQuery(id+"F4.wireOp",EDGE,"E784"),sQuery(id+"F4.wireOp",EDGE,"E785"),sQuery(id+"F4.wireOp",EDGE,"E786"),sQuery(id+"F4.wireOp",EDGE,"E787"),sQuery(id+"F4.wireOp",EDGE,"E788"),sQuery(id+"F4.wireOp",EDGE,"E789"),sQuery(id+"F4.wireOp",EDGE,"E790"),sQuery(id+"F4.wireOp",EDGE,"E791"),sQuery(id+"F4.wireOp",EDGE,"E792"),sQuery(id+"F4.wireOp",EDGE,"E793"),sQuery(id+"F4.wireOp",EDGE,"E794"),sQuery(id+"F4.wireOp",EDGE,"E795"),sQuery(id+"F4.wireOp",EDGE,"E796"),sQuery(id+"F4.wireOp",EDGE,"E797"),sQuery(id+"F4.wireOp",EDGE,"E798"),sQuery(id+"F4.wireOp",EDGE,"E799"),sQuery(id+"F4.wireOp",EDGE,"E800"),sQuery(id+"F4.wireOp",EDGE,"E801"),sQuery(id+"F4.wireOp",EDGE,"E802"),sQuery(id+"F4.wireOp",EDGE,"E803"),sQuery(id+"F4.wireOp",EDGE,"E804"),sQuery(id+"F4.wireOp",EDGE,"E805"),sQuery(id+"F4.wireOp",EDGE,"E806"),sQuery(id+"F4.wireOp",EDGE,"E807"),sQuery(id+"F4.wireOp",EDGE,"E808"),sQuery(id+"F4.wireOp",EDGE,"E809"),sQuery(id+"F4.wireOp",EDGE,"E810"),sQuery(id+"F4.wireOp",EDGE,"E811"),sQuery(id+"F4.wireOp",EDGE,"E812"),sQuery(id+"F4.wireOp",EDGE,"E813"),sQuery(id+"F4.wireOp",EDGE,"E814"),sQuery(id+"F4.wireOp",EDGE,"E815"),sQuery(id+"F4.wireOp",EDGE,"E816"),sQuery(id+"F4.wireOp",EDGE,"E817"),sQuery(id+"F4.wireOp",EDGE,"E818"),sQuery(id+"F4.wireOp",EDGE,"E819"),sQuery(id+"F4.wireOp",EDGE,"E820"),sQuery(id+"F4.wireOp",EDGE,"E821"),sQuery(id+"F4.wireOp",EDGE,"E822"),sQuery(id+"F4.wireOp",EDGE,"E823"),sQuery(id+"F4.wireOp",EDGE,"E824"),sQuery(id+"F4.wireOp",EDGE,"E825"),sQuery(id+"F4.wireOp",EDGE,"E826"),sQuery(id+"F4.wireOp",EDGE,"E827"),sQuery(id+"F4.wireOp",EDGE,"E828"),sQuery(id+"F4.wireOp",EDGE,"E829"),sQuery(id+"F4.wireOp",EDGE,"E830"),sQuery(id+"F4.wireOp",EDGE,"E831"),sQuery(id+"F4.wireOp",EDGE,"E832"),sQuery(id+"F4.wireOp",EDGE,"E833"),sQuery(id+"F4.wireOp",EDGE,"E834"),sQuery(id+"F4.wireOp",EDGE,"E835"),sQuery(id+"F4.wireOp",EDGE,"E836"),sQuery(id+"F4.wireOp",EDGE,"E837"),sQuery(id+"F4.wireOp",EDGE,"E838"),sQuery(id+"F4.wireOp",EDGE,"E839"),sQuery(id+"F4.wireOp",EDGE,"E840"),sQuery(id+"F4.wireOp",EDGE,"E841"),sQuery(id+"F4.wireOp",EDGE,"E842"),sQuery(id+"F4.wireOp",EDGE,"E843"),sQuery(id+"F4.wireOp",EDGE,"E844"),sQuery(id+"F4.wireOp",EDGE,"E845"),sQuery(id+"F4.wireOp",EDGE,"E846"),sQuery(id+"F4.wireOp",EDGE,"E847"),sQuery(id+"F4.wireOp",EDGE,"E848"),sQuery(id+"F4.wireOp",EDGE,"E849"),sQuery(id+"F4.wireOp",EDGE,"E850"),sQuery(id+"F4.wireOp",EDGE,"E851"),sQuery(id+"F4.wireOp",EDGE,"E852"),sQuery(id+"F4.wireOp",EDGE,"E853"),sQuery(id+"F4.wireOp",EDGE,"E854"),sQuery(id+"F4.wireOp",EDGE,"E855"),sQuery(id+"F4.wireOp",EDGE,"E856"),sQuery(id+"F4.wireOp",EDGE,"E857"),sQuery(id+"F4.wireOp",EDGE,"E858"),sQuery(id+"F4.wireOp",EDGE,"E859"),sQuery(id+"F4.wireOp",EDGE,"E860"),sQuery(id+"F4.wireOp",EDGE,"E861"),sQuery(id+"F4.wireOp",EDGE,"E862"),sQuery(id+"F4.wireOp",EDGE,"E863"),sQuery(id+"F4.wireOp",EDGE,"E864"),sQuery(id+"F4.wireOp",EDGE,"E865"),sQuery(id+"F4.wireOp",EDGE,"E866"),sQuery(id+"F4.wireOp",EDGE,"E867"),sQuery(id+"F4.wireOp",EDGE,"E868"),sQuery(id+"F4.wireOp",EDGE,"E869"),sQuery(id+"F4.wireOp",EDGE,"E870"),sQuery(id+"F4.wireOp",EDGE,"E871"),sQuery(id+"F4.wireOp",EDGE,"E872"),sQuery(id+"F4.wireOp",EDGE,"E873"),sQuery(id+"F4.wireOp",EDGE,"E874"),sQuery(id+"F4.wireOp",EDGE,"E875"),sQuery(id+"F4.wireOp",EDGE,"E876"),sQuery(id+"F4.wireOp",EDGE,"E877"),sQuery(id+"F4.wireOp",EDGE,"E878"),sQuery(id+"F4.wireOp",EDGE,"E879"),sQuery(id+"F4.wireOp",EDGE,"E880"),sQuery(id+"F4.wireOp",EDGE,"E881"),sQuery(id+"F4.wireOp",EDGE,"E882"),sQuery(id+"F4.wireOp",EDGE,"E883"),sQuery(id+"F4.wireOp",EDGE,"E884"),sQuery(id+"F4.wireOp",EDGE,"E885"),sQuery(id+"F4.wireOp",EDGE,"E886"),sQuery(id+"F4.wireOp",EDGE,"E887"),sQuery(id+"F4.wireOp",EDGE,"E888"),sQuery(id+"F4.wireOp",EDGE,"E889"),sQuery(id+"F4.wireOp",EDGE,"E890"),sQuery(id+"F4.wireOp",EDGE,"E891"),sQuery(id+"F4.wireOp",EDGE,"E892"),sQuery(id+"F4.wireOp",EDGE,"E893"),sQuery(id+"F4.wireOp",EDGE,"E894"),sQuery(id+"F4.wireOp",EDGE,"E895"),sQuery(id+"F4.wireOp",EDGE,"E896"),sQuery(id+"F4.wireOp",EDGE,"E897"),sQuery(id+"F4.wireOp",EDGE,"E898"),sQuery(id+"F4.wireOp",EDGE,"E899"),sQuery(id+"F4.wireOp",EDGE,"E900"),sQuery(id+"F4.wireOp",EDGE,"E901"),sQuery(id+"F4.wireOp",EDGE,"E902"),sQuery(id+"F4.wireOp",EDGE,"E903"),sQuery(id+"F4.wireOp",EDGE,"E904"),sQuery(id+"F4.wireOp",EDGE,"E905"),sQuery(id+"F4.wireOp",EDGE,"E906"),sQuery(id+"F4.wireOp",EDGE,"E907"),sQuery(id+"F4.wireOp",EDGE,"E908"),sQuery(id+"F4.wireOp",EDGE,"E909"),sQuery(id+"F4.wireOp",EDGE,"E910"),sQuery(id+"F4.wireOp",EDGE,"E911"),sQuery(id+"F4.wireOp",EDGE,"E912"),sQuery(id+"F4.wireOp",EDGE,"E913"),sQuery(id+"F4.wireOp",EDGE,"E914"),sQuery(id+"F4.wireOp",EDGE,"E915"),sQuery(id+"F4.wireOp",EDGE,"E916"),sQuery(id+"F4.wireOp",EDGE,"E917"),sQuery(id+"F4.wireOp",EDGE,"E918"),sQuery(id+"F4.wireOp",EDGE,"E919"),sQuery(id+"F4.wireOp",EDGE,"E920"),sQuery(id+"F4.wireOp",EDGE,"E921"),sQuery(id+"F4.wireOp",EDGE,"E922"),sQuery(id+"F4.wireOp",EDGE,"E923"),sQuery(id+"F4.wireOp",EDGE,"E924"),sQuery(id+"F4.wireOp",EDGE,"E925"),sQuery(id+"F4.wireOp",EDGE,"E926"),sQuery(id+"F4.wireOp",EDGE,"E927"),sQuery(id+"F4.wireOp",EDGE,"E928"),sQuery(id+"F4.wireOp",EDGE,"E929"),sQuery(id+"F4.wireOp",EDGE,"E930"),sQuery(id+"F4.wireOp",EDGE,"E931"),sQuery(id+"F4.wireOp",EDGE,"E932"),sQuery(id+"F4.wireOp",EDGE,"E933"),sQuery(id+"F4.wireOp",EDGE,"E934"),sQuery(id+"F4.wireOp",EDGE,"E935"),sQuery(id+"F4.wireOp",EDGE,"E936"),sQuery(id+"F4.wireOp",EDGE,"E937"),sQuery(id+"F4.wireOp",EDGE,"E938"),sQuery(id+"F4.wireOp",EDGE,"E939"),sQuery(id+"F4.wireOp",EDGE,"E940"),sQuery(id+"F4.wireOp",EDGE,"E941"),sQuery(id+"F4.wireOp",EDGE,"E942"),sQuery(id+"F4.wireOp",EDGE,"E943"),sQuery(id+"F4.wireOp",EDGE,"E944"),sQuery(id+"F4.wireOp",EDGE,"E945"),sQuery(id+"F4.wireOp",EDGE,"E946"),sQuery(id+"F4.wireOp",EDGE,"E947"),sQuery(id+"F4.wireOp",EDGE,"E948"),sQuery(id+"F4.wireOp",EDGE,"E949"),sQuery(id+"F4.wireOp",EDGE,"E950"),sQuery(id+"F4.wireOp",EDGE,"E951"),sQuery(id+"F4.wireOp",EDGE,"E952"),sQuery(id+"F4.wireOp",EDGE,"E953"),sQuery(id+"F4.wireOp",EDGE,"E954"),sQuery(id+"F4.wireOp",EDGE,"E955"),sQuery(id+"F4.wireOp",EDGE,"E956"),sQuery(id+"F4.wireOp",EDGE,"E957"),sQuery(id+"F4.wireOp",EDGE,"E958"),sQuery(id+"F4.wireOp",EDGE,"E959"),sQuery(id+"F4.wireOp",EDGE,"E960"),sQuery(id+"F4.wireOp",EDGE,"E961"),sQuery(id+"F4.wireOp",EDGE,"E962"),sQuery(id+"F4.wireOp",EDGE,"E963"),sQuery(id+"F4.wireOp",EDGE,"E964"),sQuery(id+"F4.wireOp",EDGE,"E965"),sQuery(id+"F4.wireOp",EDGE,"E966"),sQuery(id+"F4.wireOp",EDGE,"E967"),sQuery(id+"F4.wireOp",EDGE,"E968"),sQuery(id+"F4.wireOp",EDGE,"E969"),sQuery(id+"F4.wireOp",EDGE,"E970"),sQuery(id+"F4.wireOp",EDGE,"E971"),sQuery(id+"F4.wireOp",EDGE,"E972"),sQuery(id+"F4.wireOp",EDGE,"E973"),sQuery(id+"F4.wireOp",EDGE,"E974"),sQuery(id+"F4.wireOp",EDGE,"E975"),sQuery(id+"F4.wireOp",EDGE,"E976"),sQuery(id+"F4.wireOp",EDGE,"E977"),sQuery(id+"F4.wireOp",EDGE,"E978"),sQuery(id+"F4.wireOp",EDGE,"E979"),sQuery(id+"F4.wireOp",EDGE,"E980"),sQuery(id+"F4.wireOp",EDGE,"E981"),sQuery(id+"F4.wireOp",EDGE,"E982"),sQuery(id+"F4.wireOp",EDGE,"E983"),sQuery(id+"F4.wireOp",EDGE,"E984"),sQuery(id+"F4.wireOp",EDGE,"E985"),sQuery(id+"F4.wireOp",EDGE,"E986"),sQuery(id+"F4.wireOp",EDGE,"E987"),sQuery(id+"F4.wireOp",EDGE,"E988"),sQuery(id+"F4.wireOp",EDGE,"E989"),sQuery(id+"F4.wireOp",EDGE,"E990"),sQuery(id+"F4.wireOp",EDGE,"E991"),sQuery(id+"F4.wireOp",EDGE,"E992"),sQuery(id+"F4.wireOp",EDGE,"E993"),sQuery(id+"F4.wireOp",EDGE,"E994"),sQuery(id+"F4.wireOp",EDGE,"E995"),sQuery(id+"F4.wireOp",EDGE,"E996"),sQuery(id+"F4.wireOp",EDGE,"E997"),sQuery(id+"F4.wireOp",EDGE,"E998"),sQuery(id+"F4.wireOp",EDGE,"E999"),sQuery(id+"F4.wireOp",EDGE,"E1000"),sQuery(id+"F4.wireOp",EDGE,"E1001"),sQuery(id+"F4.wireOp",EDGE,"E1002"),sQuery(id+"F4.wireOp",EDGE,"E1003"),sQuery(id+"F4.wireOp",EDGE,"E1004"),sQuery(id+"F4.wireOp",EDGE,"E1005"),sQuery(id+"F4.wireOp",EDGE,"E1006"),sQuery(id+"F4.wireOp",EDGE,"E1007"),sQuery(id+"F4.wireOp",EDGE,"E1008"),sQuery(id+"F4.wireOp",EDGE,"E1009"),sQuery(id+"F4.wireOp",EDGE,"E1010"),sQuery(id+"F4.wireOp",EDGE,"E1011"),sQuery(id+"F4.wireOp",EDGE,"E1012"),sQuery(id+"F4.wireOp",EDGE,"E1013"),sQuery(id+"F4.wireOp",EDGE,"E1014"),sQuery(id+"F4.wireOp",EDGE,"E1015"),sQuery(id+"F4.wireOp",EDGE,"E1016"),sQuery(id+"F4.wireOp",EDGE,"E1017"),sQuery(id+"F4.wireOp",EDGE,"E1018"),sQuery(id+"F4.wireOp",EDGE,"E1019"),sQuery(id+"F4.wireOp",EDGE,"E1020"),sQuery(id+"F4.wireOp",EDGE,"E1021"),sQuery(id+"F4.wireOp",EDGE,"E1022"),sQuery(id+"F4.wireOp",EDGE,"E1023"),sQuery(id+"F4.wireOp",EDGE,"E1024"),sQuery(id+"F4.wireOp",EDGE,"E1025"),sQuery(id+"F4.wireOp",EDGE,"E1026"),sQuery(id+"F4.wireOp",EDGE,"E1027"),sQuery(id+"F4.wireOp",EDGE,"E1028"),sQuery(id+"F4.wireOp",EDGE,"E1029"),sQuery(id+"F4.wireOp",EDGE,"E1030"),sQuery(id+"F4.wireOp",EDGE,"E1031"),sQuery(id+"F4.wireOp",EDGE,"E1032"),sQuery(id+"F4.wireOp",EDGE,"E1033"),sQuery(id+"F4.wireOp",EDGE,"E1034"),sQuery(id+"F4.wireOp",EDGE,"E1035"),sQuery(id+"F4.wireOp",EDGE,"E1036"),sQuery(id+"F4.wireOp",EDGE,"E1037"),sQuery(id+"F4.wireOp",EDGE,"E1038"),sQuery(id+"F4.wireOp",EDGE,"E1039"),sQuery(id+"F4.wireOp",EDGE,"E1040"),sQuery(id+"F4.wireOp",EDGE,"E1041"),sQuery(id+"F4.wireOp",EDGE,"E1042"),sQuery(id+"F4.wireOp",EDGE,"E1043"),sQuery(id+"F4.wireOp",EDGE,"E1044"),sQuery(id+"F4.wireOp",EDGE,"E1045"),sQuery(id+"F4.wireOp",EDGE,"E1046"),sQuery(id+"F4.wireOp",EDGE,"E1047"),sQuery(id+"F4.wireOp",EDGE,"E1048"),sQuery(id+"F4.wireOp",EDGE,"E1049"),sQuery(id+"F4.wireOp",EDGE,"E1050"),sQuery(id+"F4.wireOp",EDGE,"E1051"),sQuery(id+"F4.wireOp",EDGE,"E1052"),sQuery(id+"F4.wireOp",EDGE,"E1053"),sQuery(id+"F4.wireOp",EDGE,"E1054"),sQuery(id+"F4.wireOp",EDGE,"E1055"),sQuery(id+"F4.wireOp",EDGE,"E1056"),sQuery(id+"F4.wireOp",EDGE,"E1057"),sQuery(id+"F4.wireOp",EDGE,"E1058"),sQuery(id+"F4.wireOp",EDGE,"E1059"),sQuery(id+"F4.wireOp",EDGE,"E1060"),sQuery(id+"F4.wireOp",EDGE,"E1061"),sQuery(id+"F4.wireOp",EDGE,"E1062"),sQuery(id+"F4.wireOp",EDGE,"E1063"),sQuery(id+"F4.wireOp",EDGE,"E1064"),sQuery(id+"F4.wireOp",EDGE,"E1065"),sQuery(id+"F4.wireOp",EDGE,"E1066"),sQuery(id+"F4.wireOp",EDGE,"E1067"),sQuery(id+"F4.wireOp",EDGE,"E1068"),sQuery(id+"F4.wireOp",EDGE,"E1069"),sQuery(id+"F4.wireOp",EDGE,"E1070"),sQuery(id+"F4.wireOp",EDGE,"E1071"),sQuery(id+"F4.wireOp",EDGE,"E1072"),sQuery(id+"F4.wireOp",EDGE,"E1073"),sQuery(id+"F4.wireOp",EDGE,"E1074"),sQuery(id+"F4.wireOp",EDGE,"E1075"),sQuery(id+"F4.wireOp",EDGE,"E1076"),sQuery(id+"F4.wireOp",EDGE,"E1077"),sQuery(id+"F4.wireOp",EDGE,"E1078"),sQuery(id+"F4.wireOp",EDGE,"E1079"),sQuery(id+"F4.wireOp",EDGE,"E1080"),sQuery(id+"F4.wireOp",EDGE,"E1081"),sQuery(id+"F4.wireOp",EDGE,"E1082"),sQuery(id+"F4.wireOp",EDGE,"E1083"),sQuery(id+"F4.wireOp",EDGE,"E1084"),sQuery(id+"F4.wireOp",EDGE,"E1085"),sQuery(id+"F4.wireOp",EDGE,"E1086"),sQuery(id+"F4.wireOp",EDGE,"E1087"),sQuery(id+"F4.wireOp",EDGE,"E1088"),sQuery(id+"F4.wireOp",EDGE,"E1089"),sQuery(id+"F4.wireOp",EDGE,"E1090"),sQuery(id+"F4.wireOp",EDGE,"E1091"),sQuery(id+"F4.wireOp",EDGE,"E1092"),sQuery(id+"F4.wireOp",EDGE,"E1093"),sQuery(id+"F4.wireOp",EDGE,"E1094"),sQuery(id+"F4.wireOp",EDGE,"E1095"),sQuery(id+"F4.wireOp",EDGE,"E1096"),sQuery(id+"F4.wireOp",EDGE,"E1097"),sQuery(id+"F4.wireOp",EDGE,"E1098"),sQuery(id+"F4.wireOp",EDGE,"E1099"),sQuery(id+"F4.wireOp",EDGE,"E1100"),sQuery(id+"F4.wireOp",EDGE,"E1101"),sQuery(id+"F4.wireOp",EDGE,"E1102"),sQuery(id+"F4.wireOp",EDGE,"E1103"),sQuery(id+"F4.wireOp",EDGE,"E1104"),sQuery(id+"F4.wireOp",EDGE,"E1105"),sQuery(id+"F4.wireOp",EDGE,"E1106"),sQuery(id+"F4.wireOp",EDGE,"E1107"),sQuery(id+"F4.wireOp",EDGE,"E1108"),sQuery(id+"F4.wireOp",EDGE,"E1109"),sQuery(id+"F4.wireOp",EDGE,"E1110"),sQuery(id+"F4.wireOp",EDGE,"E1111")])]});
            deleteBodies(context, id + "F15", {"entities" : qUnion([Q0])});
        }
        {
            var Q0;
            Q0=qCreatedBy(makeId("Front.planeOp"),FACE);
            cPlane(context, id + "F16", {"entities" : qUnion([Q0]), "cplaneType" : CPlaneType.OFFSET, "offset" : 50 * mm, "width" : 150 * mm, "height" : 150 * mm});
        }
        {
            var Q0;
            Q0=qCreatedBy(id+"F16.planeOp",FACE);
            var sketch = newSketch(context, id + "F17", { "sketchPlane" : qUnion([Q0])});
            skCircle(sketch, "E1678", {"center": v(-35.84, -33.86) * mm, "radius": 4 * mm});
            skSolve(sketch);
        }
        {
            var Q0;
            Q0=makeQuery(id+"F17.imprint","IMPRINT",FACE,{"disambiguationData":[TD([[makeQuery(id+"F17.imprint","IMPRINT",EDGE,{"derivedFrom":sQuery(id+"F17.wireOp",EDGE,"E1678")}),1.0]])]});
            extrude(context, id + "F18", {"entities" : qUnion([Q0]), "endBound" : BoundingType.SYMMETRIC, "depth" : 430 * mm});
        }
        {
            var Q0;
            Q0=makeQuery(id+"F18.opExtrude","SWEPT_BODY",BODY,{"disambiguationData":[OSD([sQuery(id+"F17.wireOp",EDGE,"E1678")])]});
            var Q1;
            Q1=qCreatedBy(makeId("Right.planeOp"),FACE);
            mirror(context, id + "F19", {"entities" : qUnion([Q0]), "mirrorPlane" : qUnion([Q1])});
        }
        {
            var Q0;
            Q0=makeQuery(id+"F10.opExtrude","CAP_FACE",FACE,{"disambiguationData":[OSD([sQuery(id+"F9.wireOp",EDGE,"E1112"),sQuery(id+"F9.wireOp",EDGE,"E1113"),sQuery(id+"F9.wireOp",EDGE,"E1114"),sQuery(id+"F9.wireOp",EDGE,"E1115"),sQuery(id+"F9.wireOp",EDGE,"E1116"),sQuery(id+"F9.wireOp",EDGE,"E1117"),sQuery(id+"F9.wireOp",EDGE,"E1118"),sQuery(id+"F9.wireOp",EDGE,"E1119"),sQuery(id+"F9.wireOp",EDGE,"E1120"),sQuery(id+"F9.wireOp",EDGE,"E1121"),sQuery(id+"F9.wireOp",EDGE,"E1122"),sQuery(id+"F9.wireOp",EDGE,"E1123"),sQuery(id+"F9.wireOp",EDGE,"E1124"),sQuery(id+"F9.wireOp",EDGE,"E1125"),sQuery(id+"F9.wireOp",EDGE,"E1126"),sQuery(id+"F9.wireOp",EDGE,"E1127"),sQuery(id+"F9.wireOp",EDGE,"E1128"),sQuery(id+"F9.wireOp",EDGE,"E1129"),sQuery(id+"F9.wireOp",EDGE,"E1130"),sQuery(id+"F9.wireOp",EDGE,"E1131"),sQuery(id+"F9.wireOp",EDGE,"E1132"),sQuery(id+"F9.wireOp",EDGE,"E1133"),sQuery(id+"F9.wireOp",EDGE,"E1134"),sQuery(id+"F9.wireOp",EDGE,"E1135"),sQuery(id+"F9.wireOp",EDGE,"E1136"),sQuery(id+"F9.wireOp",EDGE,"E1137"),sQuery(id+"F9.wireOp",EDGE,"E1138"),sQuery(id+"F9.wireOp",EDGE,"E1139"),sQuery(id+"F9.wireOp",EDGE,"E1140"),sQuery(id+"F9.wireOp",EDGE,"E1141"),sQuery(id+"F9.wireOp",EDGE,"E1142"),sQuery(id+"F9.wireOp",EDGE,"E1143"),sQuery(id+"F9.wireOp",EDGE,"E1144"),sQuery(id+"F9.wireOp",EDGE,"E1145"),sQuery(id+"F9.wireOp",EDGE,"E1146"),sQuery(id+"F9.wireOp",EDGE,"E1147"),sQuery(id+"F9.wireOp",EDGE,"E1148"),sQuery(id+"F9.wireOp",EDGE,"E1149"),sQuery(id+"F9.wireOp",EDGE,"E1150"),sQuery(id+"F9.wireOp",EDGE,"E1151"),sQuery(id+"F9.wireOp",EDGE,"E1152"),sQuery(id+"F9.wireOp",EDGE,"E1153"),sQuery(id+"F9.wireOp",EDGE,"E1154"),sQuery(id+"F9.wireOp",EDGE,"E1155"),sQuery(id+"F9.wireOp",EDGE,"E1156"),sQuery(id+"F9.wireOp",EDGE,"E1157"),sQuery(id+"F9.wireOp",EDGE,"E1158"),sQuery(id+"F9.wireOp",EDGE,"E1159"),sQuery(id+"F9.wireOp",EDGE,"E1160"),sQuery(id+"F9.wireOp",EDGE,"E1161"),sQuery(id+"F9.wireOp",EDGE,"E1162"),sQuery(id+"F9.wireOp",EDGE,"E1163"),sQuery(id+"F9.wireOp",EDGE,"E1164"),sQuery(id+"F9.wireOp",EDGE,"E1165"),sQuery(id+"F9.wireOp",EDGE,"E1166"),sQuery(id+"F9.wireOp",EDGE,"E1167"),sQuery(id+"F9.wireOp",EDGE,"E1168"),sQuery(id+"F9.wireOp",EDGE,"E1169"),sQuery(id+"F9.wireOp",EDGE,"E1170"),sQuery(id+"F9.wireOp",EDGE,"E1171"),sQuery(id+"F9.wireOp",EDGE,"E1172"),sQuery(id+"F9.wireOp",EDGE,"E1173"),sQuery(id+"F9.wireOp",EDGE,"E1174"),sQuery(id+"F9.wireOp",EDGE,"E1175"),sQuery(id+"F9.wireOp",EDGE,"E1176"),sQuery(id+"F9.wireOp",EDGE,"E1177"),sQuery(id+"F9.wireOp",EDGE,"E1178"),sQuery(id+"F9.wireOp",EDGE,"E1179"),sQuery(id+"F9.wireOp",EDGE,"E1180"),sQuery(id+"F9.wireOp",EDGE,"E1181"),sQuery(id+"F9.wireOp",EDGE,"E1182"),sQuery(id+"F9.wireOp",EDGE,"E1183"),sQuery(id+"F9.wireOp",EDGE,"E1184"),sQuery(id+"F9.wireOp",EDGE,"E1185"),sQuery(id+"F9.wireOp",EDGE,"E1186"),sQuery(id+"F9.wireOp",EDGE,"E1187"),sQuery(id+"F9.wireOp",EDGE,"E1188"),sQuery(id+"F9.wireOp",EDGE,"E1189"),sQuery(id+"F9.wireOp",EDGE,"E1190"),sQuery(id+"F9.wireOp",EDGE,"E1191"),sQuery(id+"F9.wireOp",EDGE,"E1192"),sQuery(id+"F9.wireOp",EDGE,"E1193"),sQuery(id+"F9.wireOp",EDGE,"E1194"),sQuery(id+"F9.wireOp",EDGE,"E1195"),sQuery(id+"F9.wireOp",EDGE,"E1196"),sQuery(id+"F9.wireOp",EDGE,"E1197"),sQuery(id+"F9.wireOp",EDGE,"E1198"),sQuery(id+"F9.wireOp",EDGE,"E1199"),sQuery(id+"F9.wireOp",EDGE,"E1200"),sQuery(id+"F9.wireOp",EDGE,"E1201"),sQuery(id+"F9.wireOp",EDGE,"E1202"),sQuery(id+"F9.wireOp",EDGE,"E1203"),sQuery(id+"F9.wireOp",EDGE,"E1204"),sQuery(id+"F9.wireOp",EDGE,"E1205"),sQuery(id+"F9.wireOp",EDGE,"E1206"),sQuery(id+"F9.wireOp",EDGE,"E1207"),sQuery(id+"F9.wireOp",EDGE,"E1208"),sQuery(id+"F9.wireOp",EDGE,"E1209"),sQuery(id+"F9.wireOp",EDGE,"E1210"),sQuery(id+"F9.wireOp",EDGE,"E1211"),sQuery(id+"F9.wireOp",EDGE,"E1212"),sQuery(id+"F9.wireOp",EDGE,"E1213"),sQuery(id+"F9.wireOp",EDGE,"E1214"),sQuery(id+"F9.wireOp",EDGE,"E1215"),sQuery(id+"F9.wireOp",EDGE,"E1216"),sQuery(id+"F9.wireOp",EDGE,"E1217"),sQuery(id+"F9.wireOp",EDGE,"E1218"),sQuery(id+"F9.wireOp",EDGE,"E1219"),sQuery(id+"F9.wireOp",EDGE,"E1220"),sQuery(id+"F9.wireOp",EDGE,"E1221"),sQuery(id+"F9.wireOp",EDGE,"E1222"),sQuery(id+"F9.wireOp",EDGE,"E1223"),sQuery(id+"F9.wireOp",EDGE,"E1224"),sQuery(id+"F9.wireOp",EDGE,"E1225"),sQuery(id+"F9.wireOp",EDGE,"E1226"),sQuery(id+"F9.wireOp",EDGE,"E1227"),sQuery(id+"F9.wireOp",EDGE,"E1228"),sQuery(id+"F9.wireOp",EDGE,"E1229"),sQuery(id+"F9.wireOp",EDGE,"E1230"),sQuery(id+"F9.wireOp",EDGE,"E1231"),sQuery(id+"F9.wireOp",EDGE,"E1232"),sQuery(id+"F9.wireOp",EDGE,"E1233"),sQuery(id+"F9.wireOp",EDGE,"E1234"),sQuery(id+"F9.wireOp",EDGE,"E1235"),sQuery(id+"F9.wireOp",EDGE,"E1236"),sQuery(id+"F9.wireOp",EDGE,"E1237"),sQuery(id+"F9.wireOp",EDGE,"E1238"),sQuery(id+"F9.wireOp",EDGE,"E1239"),sQuery(id+"F9.wireOp",EDGE,"E1240"),sQuery(id+"F9.wireOp",EDGE,"E1241"),sQuery(id+"F9.wireOp",EDGE,"E1242"),sQuery(id+"F9.wireOp",EDGE,"E1243"),sQuery(id+"F9.wireOp",EDGE,"E1244"),sQuery(id+"F9.wireOp",EDGE,"E1245"),sQuery(id+"F9.wireOp",EDGE,"E1246"),sQuery(id+"F9.wireOp",EDGE,"E1247"),sQuery(id+"F9.wireOp",EDGE,"E1248"),sQuery(id+"F9.wireOp",EDGE,"E1249"),sQuery(id+"F9.wireOp",EDGE,"E1250"),sQuery(id+"F9.wireOp",EDGE,"E1251"),sQuery(id+"F9.wireOp",EDGE,"E1252"),sQuery(id+"F9.wireOp",EDGE,"E1253"),sQuery(id+"F9.wireOp",EDGE,"E1254"),sQuery(id+"F9.wireOp",EDGE,"E1255"),sQuery(id+"F9.wireOp",EDGE,"E1256"),sQuery(id+"F9.wireOp",EDGE,"E1257"),sQuery(id+"F9.wireOp",EDGE,"E1258"),sQuery(id+"F9.wireOp",EDGE,"E1259")])],"isStart":true});
            cPlane(context, id + "F20", {"entities" : qUnion([Q0]), "cplaneType" : CPlaneType.OFFSET, "offset" : 50 * mm, "width" : 150 * mm, "height" : 150 * mm});
        }
        {
            var Q0;
            Q0=qCreatedBy(id+"F20.planeOp",FACE);
            var sketch = newSketch(context, id + "F21", { "sketchPlane" : qUnion([Q0])});
            skLineSegment(sketch, "E1679.bottom", {"start": v(-211.49, 33.12) * mm, "end": v(218.51, 33.12) * mm});
            skLineSegment(sketch, "E1679.top", {"start": v(-211.49, -66.88) * mm, "end": v(218.51, -66.88) * mm});
            skLineSegment(sketch, "E1679.left", {"start": v(-211.49, 33.12) * mm, "end": v(-211.49, -66.88) * mm});
            skLineSegment(sketch, "E1679.right", {"start": v(218.51, 33.12) * mm, "end": v(218.51, -66.88) * mm});
            skCircle(sketch, "E1680", {"center": v(-202.39, 23.92) * mm, "radius": 1.6 * mm});
            skLineSegment(sketch, "E1681", {"start": v(-202.39, 23.92) * mm, "end": v(-202.39, -66.88) * mm, "construction": true});
            skLineSegment(sketch, "E1682.direction2", {"start": v(-202.39, 23.92) * mm, "end": v(-202.39, -45.08) * mm, "construction": true});
            skCircle(sketch, "E1683.0.1.0", {"center": v(-202.39, -59.38) * mm, "radius": 1.6 * mm});
            skCircle(sketch, "E1683.1.0.0", {"center": v(-165.39, 23.92) * mm, "radius": 1.6 * mm});
            skCircle(sketch, "E1683.1.1.0", {"center": v(-165.39, -59.38) * mm, "radius": 1.6 * mm});
            skCircle(sketch, "E1683.2.0.0", {"center": v(-128.39, 23.92) * mm, "radius": 1.6 * mm});
            skCircle(sketch, "E1683.2.1.0", {"center": v(-128.39, -59.38) * mm, "radius": 1.6 * mm});
            skCircle(sketch, "E1683.3.0.0", {"center": v(-91.39, 23.92) * mm, "radius": 1.6 * mm});
            skCircle(sketch, "E1683.3.1.0", {"center": v(-91.39, -59.38) * mm, "radius": 1.6 * mm});
            skCircle(sketch, "E1683.4.0.0", {"center": v(-54.39, 23.92) * mm, "radius": 1.6 * mm});
            skCircle(sketch, "E1683.4.1.0", {"center": v(-54.39, -59.38) * mm, "radius": 1.6 * mm});
            skCircle(sketch, "E1683.5.0.0", {"center": v(-17.39, 23.92) * mm, "radius": 1.6 * mm});
            skCircle(sketch, "E1683.5.1.0", {"center": v(-17.39, -59.38) * mm, "radius": 1.6 * mm});
            skCircle(sketch, "E1683.6.0.0", {"center": v(19.61, 23.92) * mm, "radius": 1.6 * mm});
            skCircle(sketch, "E1683.6.1.0", {"center": v(19.61, -59.38) * mm, "radius": 1.6 * mm});
            skCircle(sketch, "E1683.7.0.0", {"center": v(56.61, 23.92) * mm, "radius": 1.6 * mm});
            skCircle(sketch, "E1683.7.1.0", {"center": v(56.61, -59.38) * mm, "radius": 1.6 * mm});
            skCircle(sketch, "E1683.8.0.0", {"center": v(93.61, 23.92) * mm, "radius": 1.6 * mm});
            skCircle(sketch, "E1683.8.1.0", {"center": v(93.61, -59.38) * mm, "radius": 1.6 * mm});
            skCircle(sketch, "E1683.9.0.0", {"center": v(130.61, 23.92) * mm, "radius": 1.6 * mm});
            skCircle(sketch, "E1683.9.1.0", {"center": v(130.61, -59.38) * mm, "radius": 1.6 * mm});
            skCircle(sketch, "E1683.10.0.0", {"center": v(167.61, 23.92) * mm, "radius": 1.6 * mm});
            skCircle(sketch, "E1683.10.1.0", {"center": v(167.61, -59.38) * mm, "radius": 1.6 * mm});
            skCircle(sketch, "E1683.11.0.0", {"center": v(204.61, 23.92) * mm, "radius": 1.6 * mm});
            skCircle(sketch, "E1683.11.1.0", {"center": v(204.61, -59.38) * mm, "radius": 1.6 * mm});
            skLineSegment(sketch, "E1683.direction1", {"start": v(-202.39, 23.92) * mm, "end": v(-165.39, 23.92) * mm, "construction": true});
            skLineSegment(sketch, "E1683.direction2", {"start": v(-202.39, 23.92) * mm, "end": v(-202.39, -59.38) * mm, "construction": true});
            skSolve(sketch);
        }
        {
            var Q0;
            Q0 = qSketchRegion(id + "F21", true);
            extrude(context, id + "F22", {"entities" : qUnion([Q0]), "depth" : 15 * mm});
        }
    });
